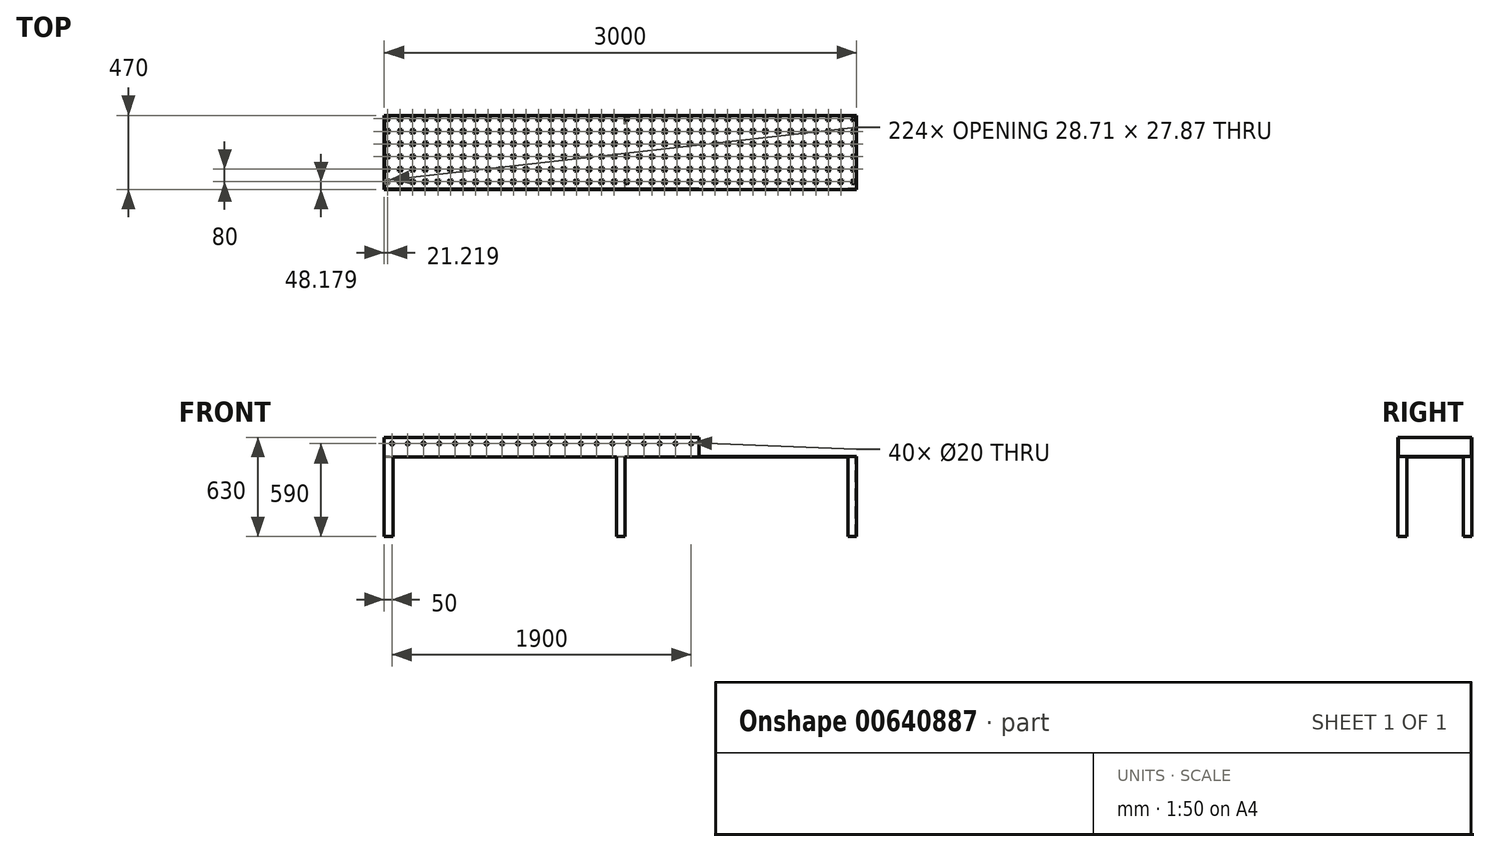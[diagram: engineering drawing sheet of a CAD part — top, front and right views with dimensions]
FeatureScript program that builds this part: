
annotation { "Feature Type Name" : "Feature", "Feature Type Description" : "" }
export const myFeature = defineFeature(function(context is Context, id is Id, definition is map)
    precondition{}
    {
        {
            var Q0;
            Q0=qCreatedBy(makeId("Top.planeOp"),FACE);
            var sketch = newSketch(context, id + "F0", { "sketchPlane" : qUnion([Q0])});
            skLineSegment(sketch, "E0", {"start": v(0, 849.7) * mm, "end": v(0, -834.12) * mm, "construction": true});
            skLineSegment(sketch, "E1", {"start": v(-852.3, 0) * mm, "end": v(888.69, 0) * mm, "construction": true});
            skLineSegment(sketch, "E2.bottom", {"start": v(-1500, 235) * mm, "end": v(1500, 235) * mm});
            skLineSegment(sketch, "E2.top", {"start": v(-1500, -235) * mm, "end": v(1500, -235) * mm});
            skLineSegment(sketch, "E2.left", {"start": v(-1500, 235) * mm, "end": v(-1500, -235) * mm});
            skLineSegment(sketch, "E2.right", {"start": v(1500, 235) * mm, "end": v(1500, -235) * mm});
            skSolve(sketch);
        }
        {
            var Q0;
            Q0 = qSketchRegion(id + "F0", true);
            extrude(context, id + "F1", {"entities" : qUnion([Q0]), "depth" : 125 * mm, "offsetDistance" : 25.4 * mm});
        }
        {
            var Q0;
            Q0=makeQuery(id+"F1.opExtrude","CAP_FACE",FACE,{"disambiguationData":[OSD([sQuery(id+"F0.wireOp",EDGE,"E2.bottom"),sQuery(id+"F0.wireOp",EDGE,"E2.top"),sQuery(id+"F0.wireOp",EDGE,"E2.left"),sQuery(id+"F0.wireOp",EDGE,"E2.right")])],"isStart":false});
            shell(context, id + "F2", {"entities" : qUnion([Q0]), "thickness" : 2.54 * mm});
        }
        {
            var Q0;
            Q0=makeQuery(id+"F1.opExtrude","SWEPT_FACE",FACE,{"disambiguationData":[OSD([sQuery(id+"F0.wireOp",EDGE,"E2.top")])]});
            var sketch = newSketch(context, id + "F3", { "sketchPlane" : qUnion([Q0])});
            skLineSegment(sketch, "E3", {"start": v(-1500, 85) * mm, "end": v(1500, 85) * mm, "construction": true});
            skCircle(sketch, "E4", {"center": v(-1450, 85) * mm, "radius": 10 * mm});
            skCircle(sketch, "E5.1.0.0", {"center": v(-1350, 85) * mm, "radius": 10 * mm});
            skCircle(sketch, "E5.2.0.0", {"center": v(-1250, 85) * mm, "radius": 10 * mm});
            skCircle(sketch, "E5.3.0.0", {"center": v(-1150, 85) * mm, "radius": 10 * mm});
            skCircle(sketch, "E5.4.0.0", {"center": v(-1050, 85) * mm, "radius": 10 * mm});
            skCircle(sketch, "E5.5.0.0", {"center": v(-950, 85) * mm, "radius": 10 * mm});
            skCircle(sketch, "E5.6.0.0", {"center": v(-850, 85) * mm, "radius": 10 * mm});
            skCircle(sketch, "E5.7.0.0", {"center": v(-750, 85) * mm, "radius": 10 * mm});
            skCircle(sketch, "E5.8.0.0", {"center": v(-650, 85) * mm, "radius": 10 * mm});
            skCircle(sketch, "E5.9.0.0", {"center": v(-550, 85) * mm, "radius": 10 * mm});
            skCircle(sketch, "E5.10.0.0", {"center": v(-450, 85) * mm, "radius": 10 * mm});
            skCircle(sketch, "E5.11.0.0", {"center": v(-350, 85) * mm, "radius": 10 * mm});
            skCircle(sketch, "E5.12.0.0", {"center": v(-250, 85) * mm, "radius": 10 * mm});
            skCircle(sketch, "E5.13.0.0", {"center": v(-150, 85) * mm, "radius": 10 * mm});
            skCircle(sketch, "E5.14.0.0", {"center": v(-50, 85) * mm, "radius": 10 * mm});
            skCircle(sketch, "E5.15.0.0", {"center": v(50, 85) * mm, "radius": 10 * mm});
            skCircle(sketch, "E5.16.0.0", {"center": v(150, 85) * mm, "radius": 10 * mm});
            skCircle(sketch, "E5.17.0.0", {"center": v(250, 85) * mm, "radius": 10 * mm});
            skCircle(sketch, "E5.18.0.0", {"center": v(350, 85) * mm, "radius": 10 * mm});
            skCircle(sketch, "E5.19.0.0", {"center": v(450, 85) * mm, "radius": 10 * mm});
            skLineSegment(sketch, "E5.direction1", {"start": v(-1450, 85) * mm, "end": v(-1350, 85) * mm, "construction": true});
            skSolve(sketch);
        }
        {
            var Q0;
            Q0 = qSketchRegion(id + "F3", true);
            var Q1;
            Q1=makeQuery(id+"F1.opExtrude","SWEPT_FACE",FACE,{"disambiguationData":[OSD([sQuery(id+"F0.wireOp",EDGE,"E2.bottom")])]});
            extrude(context, id + "F4", {"entities" : qUnion([Q0]), "operationType" : NewBodyOperationType.REMOVE, "endBound" : BoundingType.UP_TO_SURFACE, "oppositeDirection" : true, "depth" : 25.4 * mm, "endBoundEntityFace" : qUnion([Q1]), "offsetDistance" : 25.4 * mm});
        }
        {
            var Q0;
            Q0=makeQuery(id+"F1.opExtrude","CAP_FACE",FACE,{"disambiguationData":[OSD([sQuery(id+"F0.wireOp",EDGE,"E2.bottom"),sQuery(id+"F0.wireOp",EDGE,"E2.top"),sQuery(id+"F0.wireOp",EDGE,"E2.left"),sQuery(id+"F0.wireOp",EDGE,"E2.right")])],"isStart":true});
            var sketch = newSketch(context, id + "F5", { "sketchPlane" : qUnion([Q0])});
            skLineSegment(sketch, "E6", {"start": v(-1500, 235) * mm, "end": v(-1500, 180) * mm});
            skLineSegment(sketch, "E7", {"start": v(-1500, 180) * mm, "end": v(-1495, 180) * mm});
            skLineSegment(sketch, "E8", {"start": v(-1495, 180) * mm, "end": v(-1495, 230) * mm});
            skLineSegment(sketch, "E9", {"start": v(-1495, 230) * mm, "end": v(-1445, 230) * mm});
            skLineSegment(sketch, "E10", {"start": v(-1445, 230) * mm, "end": v(-1445, 235) * mm});
            skLineSegment(sketch, "E11", {"start": v(-1445, 235) * mm, "end": v(-1500, 235) * mm});
            skLineSegment(sketch, "E12", {"start": v(-1500, -235) * mm, "end": v(-1500, -180) * mm});
            skLineSegment(sketch, "E13", {"start": v(-1500, -180) * mm, "end": v(-1495, -180) * mm});
            skLineSegment(sketch, "E14", {"start": v(-1495, -180) * mm, "end": v(-1495, -230) * mm});
            skLineSegment(sketch, "E15", {"start": v(-1495, -230) * mm, "end": v(-1445, -230) * mm});
            skLineSegment(sketch, "E16", {"start": v(-1445, -230) * mm, "end": v(-1445, -235) * mm});
            skLineSegment(sketch, "E17", {"start": v(-1445, -235) * mm, "end": v(-1500, -235) * mm});
            skLineSegment(sketch, "E18", {"start": v(0, 235) * mm, "end": v(0, -263.12) * mm, "construction": true});
            skLineSegment(sketch, "E19", {"start": v(-25, 235) * mm, "end": v(30, 235) * mm});
            skLineSegment(sketch, "E20", {"start": v(30, 235) * mm, "end": v(30, 180) * mm});
            skLineSegment(sketch, "E21", {"start": v(30, 180) * mm, "end": v(25, 180) * mm});
            skLineSegment(sketch, "E22", {"start": v(25, 180) * mm, "end": v(25, 230) * mm});
            skLineSegment(sketch, "E23", {"start": v(25, 230) * mm, "end": v(-25, 230) * mm});
            skLineSegment(sketch, "E24", {"start": v(-25, 230) * mm, "end": v(-25, 235) * mm});
            skLineSegment(sketch, "E25", {"start": v(-25, -235) * mm, "end": v(30, -235) * mm});
            skLineSegment(sketch, "E26", {"start": v(30, -235) * mm, "end": v(30, -180) * mm});
            skLineSegment(sketch, "E27", {"start": v(30, -180) * mm, "end": v(25, -180) * mm});
            skLineSegment(sketch, "E28", {"start": v(25, -180) * mm, "end": v(25, -230) * mm});
            skLineSegment(sketch, "E29", {"start": v(25, -230) * mm, "end": v(-25, -230) * mm});
            skLineSegment(sketch, "E30", {"start": v(-25, -230) * mm, "end": v(-25, -235) * mm});
            skLineSegment(sketch, "E31", {"start": v(1445, 235) * mm, "end": v(1500, 235) * mm});
            skLineSegment(sketch, "E32", {"start": v(1500, 235) * mm, "end": v(1500, 180) * mm});
            skLineSegment(sketch, "E33", {"start": v(1500, 180) * mm, "end": v(1495, 180) * mm});
            skLineSegment(sketch, "E34", {"start": v(1495, 180) * mm, "end": v(1495, 230) * mm});
            skLineSegment(sketch, "E35", {"start": v(1495, 230) * mm, "end": v(1445, 230) * mm});
            skLineSegment(sketch, "E36", {"start": v(1445, 230) * mm, "end": v(1445, 235) * mm});
            skLineSegment(sketch, "E37", {"start": v(1500, -180) * mm, "end": v(1500, -235) * mm});
            skLineSegment(sketch, "E38", {"start": v(1500, -235) * mm, "end": v(1445, -235) * mm});
            skLineSegment(sketch, "E39", {"start": v(1445, -235) * mm, "end": v(1445, -230) * mm});
            skLineSegment(sketch, "E40", {"start": v(1445, -230) * mm, "end": v(1495, -230) * mm});
            skLineSegment(sketch, "E41", {"start": v(1495, -230) * mm, "end": v(1495, -180) * mm});
            skLineSegment(sketch, "E42", {"start": v(1495, -180) * mm, "end": v(1500, -180) * mm});
            skSolve(sketch);
        }
        {
            var Q0;
            Q0 = qSketchRegion(id + "F5", true);
            extrude(context, id + "F6", {"entities" : qUnion([Q0]), "operationType" : NewBodyOperationType.ADD, "depth" : 505 * mm, "offsetDistance" : 25.4 * mm});
        }
        {
            var Q0;
            Q0=makeQuery(id+"F6.boolean.opBoolean","MERGE",FACE,{"derivedFrom":[makeQuery(id+"F1.opExtrude","SWEPT_FACE",FACE,{"disambiguationData":[OSD([sQuery(id+"F0.wireOp",EDGE,"E2.right")])]}),makeQuery(id+"F6.opExtrude","SWEPT_FACE",FACE,{"disambiguationData":[OSD([sQuery(id+"F5.wireOp",EDGE,"E32")])]}),makeQuery(id+"F6.opExtrude","SWEPT_FACE",FACE,{"disambiguationData":[OSD([sQuery(id+"F5.wireOp",EDGE,"E37")])]})]});
            var sketch = newSketch(context, id + "F7", { "sketchPlane" : qUnion([Q0])});
            skLineSegment(sketch, "E43.bottom", {"start": v(-235, 125) * mm, "end": v(235, 125) * mm});
            skLineSegment(sketch, "E43.left", {"start": v(-235, 125) * mm, "end": v(-235, 2.54) * mm});
            skLineSegment(sketch, "E43.right", {"start": v(235, 125) * mm, "end": v(235, 2.54) * mm});
            skLineSegment(sketch, "E44", {"start": v(-235, 2.54) * mm, "end": v(235, 2.54) * mm});
            skSolve(sketch);
        }
        {
            var Q0;
            Q0 = qSketchRegion(id + "F7", true);
            extrude(context, id + "F8", {"entities" : qUnion([Q0]), "operationType" : NewBodyOperationType.REMOVE, "oppositeDirection" : true, "depth" : 1000 * mm, "offsetDistance" : 25.4 * mm});
        }
        {
            var Q0;
            Q0=makeQuery(id+"F8.boolean.opBoolean","MERGE",FACE,{"derivedFrom":[makeQuery(id+"F2.opShell","OFFSET_FACE",FACE,{"disambiguationData":[OSD([sQuery(id+"F0.wireOp",EDGE,"E2.bottom"),sQuery(id+"F0.wireOp",EDGE,"E2.top"),sQuery(id+"F0.wireOp",EDGE,"E2.left"),sQuery(id+"F0.wireOp",EDGE,"E2.right")])]}),makeQuery(id+"F8.opExtrude","SWEPT_FACE",FACE,{"disambiguationData":[OSD([sQuery(id+"F7.wireOp",EDGE,"E44")])]})]});
            var sketch = newSketch(context, id + "F9", { "sketchPlane" : qUnion([Q0])});
            skCircle(sketch, "E45.cCircle", {"center": v(-1478.78, 213.18) * mm, "radius": 12.7 * mm, "construction": true});
            skLineSegment(sketch, "E45.0", {"start": v(-1464.43, 210.17) * mm, "end": v(-1474.2, 199.25) * mm});
            skLineSegment(sketch, "E45.1", {"start": v(-1474.2, 199.25) * mm, "end": v(-1488.56, 202.25) * mm});
            skLineSegment(sketch, "E45.2", {"start": v(-1488.56, 202.25) * mm, "end": v(-1493.14, 216.18) * mm});
            skLineSegment(sketch, "E45.3", {"start": v(-1493.14, 216.18) * mm, "end": v(-1483.36, 227.11) * mm});
            skLineSegment(sketch, "E45.4", {"start": v(-1483.36, 227.11) * mm, "end": v(-1469, 224.1) * mm});
            skLineSegment(sketch, "E45.5", {"start": v(-1469, 224.1) * mm, "end": v(-1464.43, 210.17) * mm});
            skPoint(sketch, "E45.0.midPoint", {"position": v(-1469.32, 204.71) * mm});
            skLineSegment(sketch, "E46.0.1.0", {"start": v(-1474.2, 119.25) * mm, "end": v(-1488.56, 122.25) * mm});
            skLineSegment(sketch, "E46.0.1.1", {"start": v(-1464.43, 130.17) * mm, "end": v(-1474.2, 119.25) * mm});
            skLineSegment(sketch, "E46.0.1.2", {"start": v(-1469, 144.1) * mm, "end": v(-1464.43, 130.17) * mm});
            skLineSegment(sketch, "E46.0.1.3", {"start": v(-1483.36, 147.11) * mm, "end": v(-1469, 144.1) * mm});
            skLineSegment(sketch, "E46.0.1.4", {"start": v(-1493.14, 136.18) * mm, "end": v(-1483.36, 147.11) * mm});
            skLineSegment(sketch, "E46.0.1.5", {"start": v(-1488.56, 122.25) * mm, "end": v(-1493.14, 136.18) * mm});
            skLineSegment(sketch, "E46.0.2.0", {"start": v(-1474.2, 39.25) * mm, "end": v(-1488.56, 42.25) * mm});
            skLineSegment(sketch, "E46.0.2.1", {"start": v(-1464.43, 50.17) * mm, "end": v(-1474.2, 39.25) * mm});
            skLineSegment(sketch, "E46.0.2.2", {"start": v(-1469, 64.1) * mm, "end": v(-1464.43, 50.17) * mm});
            skLineSegment(sketch, "E46.0.2.3", {"start": v(-1483.36, 67.11) * mm, "end": v(-1469, 64.1) * mm});
            skLineSegment(sketch, "E46.0.2.4", {"start": v(-1493.14, 56.18) * mm, "end": v(-1483.36, 67.11) * mm});
            skLineSegment(sketch, "E46.0.2.5", {"start": v(-1488.56, 42.25) * mm, "end": v(-1493.14, 56.18) * mm});
            skLineSegment(sketch, "E46.0.3.0", {"start": v(-1474.2, -40.75) * mm, "end": v(-1488.56, -37.75) * mm});
            skLineSegment(sketch, "E46.0.3.1", {"start": v(-1464.43, -29.83) * mm, "end": v(-1474.2, -40.75) * mm});
            skLineSegment(sketch, "E46.0.3.2", {"start": v(-1469, -15.9) * mm, "end": v(-1464.43, -29.83) * mm});
            skLineSegment(sketch, "E46.0.3.3", {"start": v(-1483.36, -12.89) * mm, "end": v(-1469, -15.9) * mm});
            skLineSegment(sketch, "E46.0.3.4", {"start": v(-1493.14, -23.82) * mm, "end": v(-1483.36, -12.89) * mm});
            skLineSegment(sketch, "E46.0.3.5", {"start": v(-1488.56, -37.75) * mm, "end": v(-1493.14, -23.82) * mm});
            skLineSegment(sketch, "E46.0.4.0", {"start": v(-1474.2, -120.75) * mm, "end": v(-1488.56, -117.75) * mm});
            skLineSegment(sketch, "E46.0.4.1", {"start": v(-1464.43, -109.83) * mm, "end": v(-1474.2, -120.75) * mm});
            skLineSegment(sketch, "E46.0.4.2", {"start": v(-1469, -95.9) * mm, "end": v(-1464.43, -109.83) * mm});
            skLineSegment(sketch, "E46.0.4.3", {"start": v(-1483.36, -92.89) * mm, "end": v(-1469, -95.9) * mm});
            skLineSegment(sketch, "E46.0.4.4", {"start": v(-1493.14, -103.82) * mm, "end": v(-1483.36, -92.89) * mm});
            skLineSegment(sketch, "E46.0.4.5", {"start": v(-1488.56, -117.75) * mm, "end": v(-1493.14, -103.82) * mm});
            skLineSegment(sketch, "E46.0.5.0", {"start": v(-1474.2, -200.75) * mm, "end": v(-1488.56, -197.75) * mm});
            skLineSegment(sketch, "E46.0.5.1", {"start": v(-1464.43, -189.83) * mm, "end": v(-1474.2, -200.75) * mm});
            skLineSegment(sketch, "E46.0.5.2", {"start": v(-1469, -175.9) * mm, "end": v(-1464.43, -189.83) * mm});
            skLineSegment(sketch, "E46.0.5.3", {"start": v(-1483.36, -172.89) * mm, "end": v(-1469, -175.9) * mm});
            skLineSegment(sketch, "E46.0.5.4", {"start": v(-1493.14, -183.82) * mm, "end": v(-1483.36, -172.89) * mm});
            skLineSegment(sketch, "E46.0.5.5", {"start": v(-1488.56, -197.75) * mm, "end": v(-1493.14, -183.82) * mm});
            skLineSegment(sketch, "E46.1.0.0", {"start": v(-1394.2, 199.25) * mm, "end": v(-1408.56, 202.25) * mm});
            skLineSegment(sketch, "E46.1.0.1", {"start": v(-1384.43, 210.17) * mm, "end": v(-1394.2, 199.25) * mm});
            skLineSegment(sketch, "E46.1.0.2", {"start": v(-1389, 224.1) * mm, "end": v(-1384.43, 210.17) * mm});
            skLineSegment(sketch, "E46.1.0.3", {"start": v(-1403.36, 227.11) * mm, "end": v(-1389, 224.1) * mm});
            skLineSegment(sketch, "E46.1.0.4", {"start": v(-1413.14, 216.18) * mm, "end": v(-1403.36, 227.11) * mm});
            skLineSegment(sketch, "E46.1.0.5", {"start": v(-1408.56, 202.25) * mm, "end": v(-1413.14, 216.18) * mm});
            skLineSegment(sketch, "E46.1.1.0", {"start": v(-1394.2, 119.25) * mm, "end": v(-1408.56, 122.25) * mm});
            skLineSegment(sketch, "E46.1.1.1", {"start": v(-1384.43, 130.17) * mm, "end": v(-1394.2, 119.25) * mm});
            skLineSegment(sketch, "E46.1.1.2", {"start": v(-1389, 144.1) * mm, "end": v(-1384.43, 130.17) * mm});
            skLineSegment(sketch, "E46.1.1.3", {"start": v(-1403.36, 147.11) * mm, "end": v(-1389, 144.1) * mm});
            skLineSegment(sketch, "E46.1.1.4", {"start": v(-1413.14, 136.18) * mm, "end": v(-1403.36, 147.11) * mm});
            skLineSegment(sketch, "E46.1.1.5", {"start": v(-1408.56, 122.25) * mm, "end": v(-1413.14, 136.18) * mm});
            skLineSegment(sketch, "E46.1.2.0", {"start": v(-1394.2, 39.25) * mm, "end": v(-1408.56, 42.25) * mm});
            skLineSegment(sketch, "E46.1.2.1", {"start": v(-1384.43, 50.17) * mm, "end": v(-1394.2, 39.25) * mm});
            skLineSegment(sketch, "E46.1.2.2", {"start": v(-1389, 64.1) * mm, "end": v(-1384.43, 50.17) * mm});
            skLineSegment(sketch, "E46.1.2.3", {"start": v(-1403.36, 67.11) * mm, "end": v(-1389, 64.1) * mm});
            skLineSegment(sketch, "E46.1.2.4", {"start": v(-1413.14, 56.18) * mm, "end": v(-1403.36, 67.11) * mm});
            skLineSegment(sketch, "E46.1.2.5", {"start": v(-1408.56, 42.25) * mm, "end": v(-1413.14, 56.18) * mm});
            skLineSegment(sketch, "E46.1.3.0", {"start": v(-1394.2, -40.75) * mm, "end": v(-1408.56, -37.75) * mm});
            skLineSegment(sketch, "E46.1.3.1", {"start": v(-1384.43, -29.83) * mm, "end": v(-1394.2, -40.75) * mm});
            skLineSegment(sketch, "E46.1.3.2", {"start": v(-1389, -15.9) * mm, "end": v(-1384.43, -29.83) * mm});
            skLineSegment(sketch, "E46.1.3.3", {"start": v(-1403.36, -12.89) * mm, "end": v(-1389, -15.9) * mm});
            skLineSegment(sketch, "E46.1.3.4", {"start": v(-1413.14, -23.82) * mm, "end": v(-1403.36, -12.89) * mm});
            skLineSegment(sketch, "E46.1.3.5", {"start": v(-1408.56, -37.75) * mm, "end": v(-1413.14, -23.82) * mm});
            skLineSegment(sketch, "E46.1.4.0", {"start": v(-1394.2, -120.75) * mm, "end": v(-1408.56, -117.75) * mm});
            skLineSegment(sketch, "E46.1.4.1", {"start": v(-1384.43, -109.83) * mm, "end": v(-1394.2, -120.75) * mm});
            skLineSegment(sketch, "E46.1.4.2", {"start": v(-1389, -95.9) * mm, "end": v(-1384.43, -109.83) * mm});
            skLineSegment(sketch, "E46.1.4.3", {"start": v(-1403.36, -92.89) * mm, "end": v(-1389, -95.9) * mm});
            skLineSegment(sketch, "E46.1.4.4", {"start": v(-1413.14, -103.82) * mm, "end": v(-1403.36, -92.89) * mm});
            skLineSegment(sketch, "E46.1.4.5", {"start": v(-1408.56, -117.75) * mm, "end": v(-1413.14, -103.82) * mm});
            skLineSegment(sketch, "E46.1.5.0", {"start": v(-1394.2, -200.75) * mm, "end": v(-1408.56, -197.75) * mm});
            skLineSegment(sketch, "E46.1.5.1", {"start": v(-1384.43, -189.83) * mm, "end": v(-1394.2, -200.75) * mm});
            skLineSegment(sketch, "E46.1.5.2", {"start": v(-1389, -175.9) * mm, "end": v(-1384.43, -189.83) * mm});
            skLineSegment(sketch, "E46.1.5.3", {"start": v(-1403.36, -172.89) * mm, "end": v(-1389, -175.9) * mm});
            skLineSegment(sketch, "E46.1.5.4", {"start": v(-1413.14, -183.82) * mm, "end": v(-1403.36, -172.89) * mm});
            skLineSegment(sketch, "E46.1.5.5", {"start": v(-1408.56, -197.75) * mm, "end": v(-1413.14, -183.82) * mm});
            skLineSegment(sketch, "E46.2.0.0", {"start": v(-1314.2, 199.25) * mm, "end": v(-1328.56, 202.25) * mm});
            skLineSegment(sketch, "E46.2.0.1", {"start": v(-1304.43, 210.17) * mm, "end": v(-1314.2, 199.25) * mm});
            skLineSegment(sketch, "E46.2.0.2", {"start": v(-1309, 224.1) * mm, "end": v(-1304.43, 210.17) * mm});
            skLineSegment(sketch, "E46.2.0.3", {"start": v(-1323.36, 227.11) * mm, "end": v(-1309, 224.1) * mm});
            skLineSegment(sketch, "E46.2.0.4", {"start": v(-1333.14, 216.18) * mm, "end": v(-1323.36, 227.11) * mm});
            skLineSegment(sketch, "E46.2.0.5", {"start": v(-1328.56, 202.25) * mm, "end": v(-1333.14, 216.18) * mm});
            skLineSegment(sketch, "E46.2.1.0", {"start": v(-1314.2, 119.25) * mm, "end": v(-1328.56, 122.25) * mm});
            skLineSegment(sketch, "E46.2.1.1", {"start": v(-1304.43, 130.17) * mm, "end": v(-1314.2, 119.25) * mm});
            skLineSegment(sketch, "E46.2.1.2", {"start": v(-1309, 144.1) * mm, "end": v(-1304.43, 130.17) * mm});
            skLineSegment(sketch, "E46.2.1.3", {"start": v(-1323.36, 147.11) * mm, "end": v(-1309, 144.1) * mm});
            skLineSegment(sketch, "E46.2.1.4", {"start": v(-1333.14, 136.18) * mm, "end": v(-1323.36, 147.11) * mm});
            skLineSegment(sketch, "E46.2.1.5", {"start": v(-1328.56, 122.25) * mm, "end": v(-1333.14, 136.18) * mm});
            skLineSegment(sketch, "E46.2.2.0", {"start": v(-1314.2, 39.25) * mm, "end": v(-1328.56, 42.25) * mm});
            skLineSegment(sketch, "E46.2.2.1", {"start": v(-1304.43, 50.17) * mm, "end": v(-1314.2, 39.25) * mm});
            skLineSegment(sketch, "E46.2.2.2", {"start": v(-1309, 64.1) * mm, "end": v(-1304.43, 50.17) * mm});
            skLineSegment(sketch, "E46.2.2.3", {"start": v(-1323.36, 67.11) * mm, "end": v(-1309, 64.1) * mm});
            skLineSegment(sketch, "E46.2.2.4", {"start": v(-1333.14, 56.18) * mm, "end": v(-1323.36, 67.11) * mm});
            skLineSegment(sketch, "E46.2.2.5", {"start": v(-1328.56, 42.25) * mm, "end": v(-1333.14, 56.18) * mm});
            skLineSegment(sketch, "E46.2.3.0", {"start": v(-1314.2, -40.75) * mm, "end": v(-1328.56, -37.75) * mm});
            skLineSegment(sketch, "E46.2.3.1", {"start": v(-1304.43, -29.83) * mm, "end": v(-1314.2, -40.75) * mm});
            skLineSegment(sketch, "E46.2.3.2", {"start": v(-1309, -15.9) * mm, "end": v(-1304.43, -29.83) * mm});
            skLineSegment(sketch, "E46.2.3.3", {"start": v(-1323.36, -12.89) * mm, "end": v(-1309, -15.9) * mm});
            skLineSegment(sketch, "E46.2.3.4", {"start": v(-1333.14, -23.82) * mm, "end": v(-1323.36, -12.89) * mm});
            skLineSegment(sketch, "E46.2.3.5", {"start": v(-1328.56, -37.75) * mm, "end": v(-1333.14, -23.82) * mm});
            skLineSegment(sketch, "E46.2.4.0", {"start": v(-1314.2, -120.75) * mm, "end": v(-1328.56, -117.75) * mm});
            skLineSegment(sketch, "E46.2.4.1", {"start": v(-1304.43, -109.83) * mm, "end": v(-1314.2, -120.75) * mm});
            skLineSegment(sketch, "E46.2.4.2", {"start": v(-1309, -95.9) * mm, "end": v(-1304.43, -109.83) * mm});
            skLineSegment(sketch, "E46.2.4.3", {"start": v(-1323.36, -92.89) * mm, "end": v(-1309, -95.9) * mm});
            skLineSegment(sketch, "E46.2.4.4", {"start": v(-1333.14, -103.82) * mm, "end": v(-1323.36, -92.89) * mm});
            skLineSegment(sketch, "E46.2.4.5", {"start": v(-1328.56, -117.75) * mm, "end": v(-1333.14, -103.82) * mm});
            skLineSegment(sketch, "E46.2.5.0", {"start": v(-1314.2, -200.75) * mm, "end": v(-1328.56, -197.75) * mm});
            skLineSegment(sketch, "E46.2.5.1", {"start": v(-1304.43, -189.83) * mm, "end": v(-1314.2, -200.75) * mm});
            skLineSegment(sketch, "E46.2.5.2", {"start": v(-1309, -175.9) * mm, "end": v(-1304.43, -189.83) * mm});
            skLineSegment(sketch, "E46.2.5.3", {"start": v(-1323.36, -172.89) * mm, "end": v(-1309, -175.9) * mm});
            skLineSegment(sketch, "E46.2.5.4", {"start": v(-1333.14, -183.82) * mm, "end": v(-1323.36, -172.89) * mm});
            skLineSegment(sketch, "E46.2.5.5", {"start": v(-1328.56, -197.75) * mm, "end": v(-1333.14, -183.82) * mm});
            skLineSegment(sketch, "E46.3.0.0", {"start": v(-1234.2, 199.25) * mm, "end": v(-1248.56, 202.25) * mm});
            skLineSegment(sketch, "E46.3.0.1", {"start": v(-1224.43, 210.17) * mm, "end": v(-1234.2, 199.25) * mm});
            skLineSegment(sketch, "E46.3.0.2", {"start": v(-1229, 224.1) * mm, "end": v(-1224.43, 210.17) * mm});
            skLineSegment(sketch, "E46.3.0.3", {"start": v(-1243.36, 227.11) * mm, "end": v(-1229, 224.1) * mm});
            skLineSegment(sketch, "E46.3.0.4", {"start": v(-1253.14, 216.18) * mm, "end": v(-1243.36, 227.11) * mm});
            skLineSegment(sketch, "E46.3.0.5", {"start": v(-1248.56, 202.25) * mm, "end": v(-1253.14, 216.18) * mm});
            skLineSegment(sketch, "E46.3.1.0", {"start": v(-1234.2, 119.25) * mm, "end": v(-1248.56, 122.25) * mm});
            skLineSegment(sketch, "E46.3.1.1", {"start": v(-1224.43, 130.17) * mm, "end": v(-1234.2, 119.25) * mm});
            skLineSegment(sketch, "E46.3.1.2", {"start": v(-1229, 144.1) * mm, "end": v(-1224.43, 130.17) * mm});
            skLineSegment(sketch, "E46.3.1.3", {"start": v(-1243.36, 147.11) * mm, "end": v(-1229, 144.1) * mm});
            skLineSegment(sketch, "E46.3.1.4", {"start": v(-1253.14, 136.18) * mm, "end": v(-1243.36, 147.11) * mm});
            skLineSegment(sketch, "E46.3.1.5", {"start": v(-1248.56, 122.25) * mm, "end": v(-1253.14, 136.18) * mm});
            skLineSegment(sketch, "E46.3.2.0", {"start": v(-1234.2, 39.25) * mm, "end": v(-1248.56, 42.25) * mm});
            skLineSegment(sketch, "E46.3.2.1", {"start": v(-1224.43, 50.17) * mm, "end": v(-1234.2, 39.25) * mm});
            skLineSegment(sketch, "E46.3.2.2", {"start": v(-1229, 64.1) * mm, "end": v(-1224.43, 50.17) * mm});
            skLineSegment(sketch, "E46.3.2.3", {"start": v(-1243.36, 67.11) * mm, "end": v(-1229, 64.1) * mm});
            skLineSegment(sketch, "E46.3.2.4", {"start": v(-1253.14, 56.18) * mm, "end": v(-1243.36, 67.11) * mm});
            skLineSegment(sketch, "E46.3.2.5", {"start": v(-1248.56, 42.25) * mm, "end": v(-1253.14, 56.18) * mm});
            skLineSegment(sketch, "E46.3.3.0", {"start": v(-1234.2, -40.75) * mm, "end": v(-1248.56, -37.75) * mm});
            skLineSegment(sketch, "E46.3.3.1", {"start": v(-1224.43, -29.83) * mm, "end": v(-1234.2, -40.75) * mm});
            skLineSegment(sketch, "E46.3.3.2", {"start": v(-1229, -15.9) * mm, "end": v(-1224.43, -29.83) * mm});
            skLineSegment(sketch, "E46.3.3.3", {"start": v(-1243.36, -12.89) * mm, "end": v(-1229, -15.9) * mm});
            skLineSegment(sketch, "E46.3.3.4", {"start": v(-1253.14, -23.82) * mm, "end": v(-1243.36, -12.89) * mm});
            skLineSegment(sketch, "E46.3.3.5", {"start": v(-1248.56, -37.75) * mm, "end": v(-1253.14, -23.82) * mm});
            skLineSegment(sketch, "E46.3.4.0", {"start": v(-1234.2, -120.75) * mm, "end": v(-1248.56, -117.75) * mm});
            skLineSegment(sketch, "E46.3.4.1", {"start": v(-1224.43, -109.83) * mm, "end": v(-1234.2, -120.75) * mm});
            skLineSegment(sketch, "E46.3.4.2", {"start": v(-1229, -95.9) * mm, "end": v(-1224.43, -109.83) * mm});
            skLineSegment(sketch, "E46.3.4.3", {"start": v(-1243.36, -92.89) * mm, "end": v(-1229, -95.9) * mm});
            skLineSegment(sketch, "E46.3.4.4", {"start": v(-1253.14, -103.82) * mm, "end": v(-1243.36, -92.89) * mm});
            skLineSegment(sketch, "E46.3.4.5", {"start": v(-1248.56, -117.75) * mm, "end": v(-1253.14, -103.82) * mm});
            skLineSegment(sketch, "E46.3.5.0", {"start": v(-1234.2, -200.75) * mm, "end": v(-1248.56, -197.75) * mm});
            skLineSegment(sketch, "E46.3.5.1", {"start": v(-1224.43, -189.83) * mm, "end": v(-1234.2, -200.75) * mm});
            skLineSegment(sketch, "E46.3.5.2", {"start": v(-1229, -175.9) * mm, "end": v(-1224.43, -189.83) * mm});
            skLineSegment(sketch, "E46.3.5.3", {"start": v(-1243.36, -172.89) * mm, "end": v(-1229, -175.9) * mm});
            skLineSegment(sketch, "E46.3.5.4", {"start": v(-1253.14, -183.82) * mm, "end": v(-1243.36, -172.89) * mm});
            skLineSegment(sketch, "E46.3.5.5", {"start": v(-1248.56, -197.75) * mm, "end": v(-1253.14, -183.82) * mm});
            skLineSegment(sketch, "E46.4.0.0", {"start": v(-1154.2, 199.25) * mm, "end": v(-1168.56, 202.25) * mm});
            skLineSegment(sketch, "E46.4.0.1", {"start": v(-1144.43, 210.17) * mm, "end": v(-1154.2, 199.25) * mm});
            skLineSegment(sketch, "E46.4.0.2", {"start": v(-1149, 224.1) * mm, "end": v(-1144.43, 210.17) * mm});
            skLineSegment(sketch, "E46.4.0.3", {"start": v(-1163.36, 227.11) * mm, "end": v(-1149, 224.1) * mm});
            skLineSegment(sketch, "E46.4.0.4", {"start": v(-1173.14, 216.18) * mm, "end": v(-1163.36, 227.11) * mm});
            skLineSegment(sketch, "E46.4.0.5", {"start": v(-1168.56, 202.25) * mm, "end": v(-1173.14, 216.18) * mm});
            skLineSegment(sketch, "E46.4.1.0", {"start": v(-1154.2, 119.25) * mm, "end": v(-1168.56, 122.25) * mm});
            skLineSegment(sketch, "E46.4.1.1", {"start": v(-1144.43, 130.17) * mm, "end": v(-1154.2, 119.25) * mm});
            skLineSegment(sketch, "E46.4.1.2", {"start": v(-1149, 144.1) * mm, "end": v(-1144.43, 130.17) * mm});
            skLineSegment(sketch, "E46.4.1.3", {"start": v(-1163.36, 147.11) * mm, "end": v(-1149, 144.1) * mm});
            skLineSegment(sketch, "E46.4.1.4", {"start": v(-1173.14, 136.18) * mm, "end": v(-1163.36, 147.11) * mm});
            skLineSegment(sketch, "E46.4.1.5", {"start": v(-1168.56, 122.25) * mm, "end": v(-1173.14, 136.18) * mm});
            skLineSegment(sketch, "E46.4.2.0", {"start": v(-1154.2, 39.25) * mm, "end": v(-1168.56, 42.25) * mm});
            skLineSegment(sketch, "E46.4.2.1", {"start": v(-1144.43, 50.17) * mm, "end": v(-1154.2, 39.25) * mm});
            skLineSegment(sketch, "E46.4.2.2", {"start": v(-1149, 64.1) * mm, "end": v(-1144.43, 50.17) * mm});
            skLineSegment(sketch, "E46.4.2.3", {"start": v(-1163.36, 67.11) * mm, "end": v(-1149, 64.1) * mm});
            skLineSegment(sketch, "E46.4.2.4", {"start": v(-1173.14, 56.18) * mm, "end": v(-1163.36, 67.11) * mm});
            skLineSegment(sketch, "E46.4.2.5", {"start": v(-1168.56, 42.25) * mm, "end": v(-1173.14, 56.18) * mm});
            skLineSegment(sketch, "E46.4.3.0", {"start": v(-1154.2, -40.75) * mm, "end": v(-1168.56, -37.75) * mm});
            skLineSegment(sketch, "E46.4.3.1", {"start": v(-1144.43, -29.83) * mm, "end": v(-1154.2, -40.75) * mm});
            skLineSegment(sketch, "E46.4.3.2", {"start": v(-1149, -15.9) * mm, "end": v(-1144.43, -29.83) * mm});
            skLineSegment(sketch, "E46.4.3.3", {"start": v(-1163.36, -12.89) * mm, "end": v(-1149, -15.9) * mm});
            skLineSegment(sketch, "E46.4.3.4", {"start": v(-1173.14, -23.82) * mm, "end": v(-1163.36, -12.89) * mm});
            skLineSegment(sketch, "E46.4.3.5", {"start": v(-1168.56, -37.75) * mm, "end": v(-1173.14, -23.82) * mm});
            skLineSegment(sketch, "E46.4.4.0", {"start": v(-1154.2, -120.75) * mm, "end": v(-1168.56, -117.75) * mm});
            skLineSegment(sketch, "E46.4.4.1", {"start": v(-1144.43, -109.83) * mm, "end": v(-1154.2, -120.75) * mm});
            skLineSegment(sketch, "E46.4.4.2", {"start": v(-1149, -95.9) * mm, "end": v(-1144.43, -109.83) * mm});
            skLineSegment(sketch, "E46.4.4.3", {"start": v(-1163.36, -92.89) * mm, "end": v(-1149, -95.9) * mm});
            skLineSegment(sketch, "E46.4.4.4", {"start": v(-1173.14, -103.82) * mm, "end": v(-1163.36, -92.89) * mm});
            skLineSegment(sketch, "E46.4.4.5", {"start": v(-1168.56, -117.75) * mm, "end": v(-1173.14, -103.82) * mm});
            skLineSegment(sketch, "E46.4.5.0", {"start": v(-1154.2, -200.75) * mm, "end": v(-1168.56, -197.75) * mm});
            skLineSegment(sketch, "E46.4.5.1", {"start": v(-1144.43, -189.83) * mm, "end": v(-1154.2, -200.75) * mm});
            skLineSegment(sketch, "E46.4.5.2", {"start": v(-1149, -175.9) * mm, "end": v(-1144.43, -189.83) * mm});
            skLineSegment(sketch, "E46.4.5.3", {"start": v(-1163.36, -172.89) * mm, "end": v(-1149, -175.9) * mm});
            skLineSegment(sketch, "E46.4.5.4", {"start": v(-1173.14, -183.82) * mm, "end": v(-1163.36, -172.89) * mm});
            skLineSegment(sketch, "E46.4.5.5", {"start": v(-1168.56, -197.75) * mm, "end": v(-1173.14, -183.82) * mm});
            skLineSegment(sketch, "E46.5.0.0", {"start": v(-1074.2, 199.25) * mm, "end": v(-1088.56, 202.25) * mm});
            skLineSegment(sketch, "E46.5.0.1", {"start": v(-1064.43, 210.17) * mm, "end": v(-1074.2, 199.25) * mm});
            skLineSegment(sketch, "E46.5.0.2", {"start": v(-1069, 224.1) * mm, "end": v(-1064.43, 210.17) * mm});
            skLineSegment(sketch, "E46.5.0.3", {"start": v(-1083.36, 227.11) * mm, "end": v(-1069, 224.1) * mm});
            skLineSegment(sketch, "E46.5.0.4", {"start": v(-1093.14, 216.18) * mm, "end": v(-1083.36, 227.11) * mm});
            skLineSegment(sketch, "E46.5.0.5", {"start": v(-1088.56, 202.25) * mm, "end": v(-1093.14, 216.18) * mm});
            skLineSegment(sketch, "E46.5.1.0", {"start": v(-1074.2, 119.25) * mm, "end": v(-1088.56, 122.25) * mm});
            skLineSegment(sketch, "E46.5.1.1", {"start": v(-1064.43, 130.17) * mm, "end": v(-1074.2, 119.25) * mm});
            skLineSegment(sketch, "E46.5.1.2", {"start": v(-1069, 144.1) * mm, "end": v(-1064.43, 130.17) * mm});
            skLineSegment(sketch, "E46.5.1.3", {"start": v(-1083.36, 147.11) * mm, "end": v(-1069, 144.1) * mm});
            skLineSegment(sketch, "E46.5.1.4", {"start": v(-1093.14, 136.18) * mm, "end": v(-1083.36, 147.11) * mm});
            skLineSegment(sketch, "E46.5.1.5", {"start": v(-1088.56, 122.25) * mm, "end": v(-1093.14, 136.18) * mm});
            skLineSegment(sketch, "E46.5.2.0", {"start": v(-1074.2, 39.25) * mm, "end": v(-1088.56, 42.25) * mm});
            skLineSegment(sketch, "E46.5.2.1", {"start": v(-1064.43, 50.17) * mm, "end": v(-1074.2, 39.25) * mm});
            skLineSegment(sketch, "E46.5.2.2", {"start": v(-1069, 64.1) * mm, "end": v(-1064.43, 50.17) * mm});
            skLineSegment(sketch, "E46.5.2.3", {"start": v(-1083.36, 67.11) * mm, "end": v(-1069, 64.1) * mm});
            skLineSegment(sketch, "E46.5.2.4", {"start": v(-1093.14, 56.18) * mm, "end": v(-1083.36, 67.11) * mm});
            skLineSegment(sketch, "E46.5.2.5", {"start": v(-1088.56, 42.25) * mm, "end": v(-1093.14, 56.18) * mm});
            skLineSegment(sketch, "E46.5.3.0", {"start": v(-1074.2, -40.75) * mm, "end": v(-1088.56, -37.75) * mm});
            skLineSegment(sketch, "E46.5.3.1", {"start": v(-1064.43, -29.83) * mm, "end": v(-1074.2, -40.75) * mm});
            skLineSegment(sketch, "E46.5.3.2", {"start": v(-1069, -15.9) * mm, "end": v(-1064.43, -29.83) * mm});
            skLineSegment(sketch, "E46.5.3.3", {"start": v(-1083.36, -12.89) * mm, "end": v(-1069, -15.9) * mm});
            skLineSegment(sketch, "E46.5.3.4", {"start": v(-1093.14, -23.82) * mm, "end": v(-1083.36, -12.89) * mm});
            skLineSegment(sketch, "E46.5.3.5", {"start": v(-1088.56, -37.75) * mm, "end": v(-1093.14, -23.82) * mm});
            skLineSegment(sketch, "E46.5.4.0", {"start": v(-1074.2, -120.75) * mm, "end": v(-1088.56, -117.75) * mm});
            skLineSegment(sketch, "E46.5.4.1", {"start": v(-1064.43, -109.83) * mm, "end": v(-1074.2, -120.75) * mm});
            skLineSegment(sketch, "E46.5.4.2", {"start": v(-1069, -95.9) * mm, "end": v(-1064.43, -109.83) * mm});
            skLineSegment(sketch, "E46.5.4.3", {"start": v(-1083.36, -92.89) * mm, "end": v(-1069, -95.9) * mm});
            skLineSegment(sketch, "E46.5.4.4", {"start": v(-1093.14, -103.82) * mm, "end": v(-1083.36, -92.89) * mm});
            skLineSegment(sketch, "E46.5.4.5", {"start": v(-1088.56, -117.75) * mm, "end": v(-1093.14, -103.82) * mm});
            skLineSegment(sketch, "E46.5.5.0", {"start": v(-1074.2, -200.75) * mm, "end": v(-1088.56, -197.75) * mm});
            skLineSegment(sketch, "E46.5.5.1", {"start": v(-1064.43, -189.83) * mm, "end": v(-1074.2, -200.75) * mm});
            skLineSegment(sketch, "E46.5.5.2", {"start": v(-1069, -175.9) * mm, "end": v(-1064.43, -189.83) * mm});
            skLineSegment(sketch, "E46.5.5.3", {"start": v(-1083.36, -172.89) * mm, "end": v(-1069, -175.9) * mm});
            skLineSegment(sketch, "E46.5.5.4", {"start": v(-1093.14, -183.82) * mm, "end": v(-1083.36, -172.89) * mm});
            skLineSegment(sketch, "E46.5.5.5", {"start": v(-1088.56, -197.75) * mm, "end": v(-1093.14, -183.82) * mm});
            skLineSegment(sketch, "E46.6.0.0", {"start": v(-994.2, 199.25) * mm, "end": v(-1008.56, 202.25) * mm});
            skLineSegment(sketch, "E46.6.0.1", {"start": v(-984.43, 210.17) * mm, "end": v(-994.2, 199.25) * mm});
            skLineSegment(sketch, "E46.6.0.2", {"start": v(-989, 224.1) * mm, "end": v(-984.43, 210.17) * mm});
            skLineSegment(sketch, "E46.6.0.3", {"start": v(-1003.36, 227.11) * mm, "end": v(-989, 224.1) * mm});
            skLineSegment(sketch, "E46.6.0.4", {"start": v(-1013.14, 216.18) * mm, "end": v(-1003.36, 227.11) * mm});
            skLineSegment(sketch, "E46.6.0.5", {"start": v(-1008.56, 202.25) * mm, "end": v(-1013.14, 216.18) * mm});
            skLineSegment(sketch, "E46.6.1.0", {"start": v(-994.2, 119.25) * mm, "end": v(-1008.56, 122.25) * mm});
            skLineSegment(sketch, "E46.6.1.1", {"start": v(-984.43, 130.17) * mm, "end": v(-994.2, 119.25) * mm});
            skLineSegment(sketch, "E46.6.1.2", {"start": v(-989, 144.1) * mm, "end": v(-984.43, 130.17) * mm});
            skLineSegment(sketch, "E46.6.1.3", {"start": v(-1003.36, 147.11) * mm, "end": v(-989, 144.1) * mm});
            skLineSegment(sketch, "E46.6.1.4", {"start": v(-1013.14, 136.18) * mm, "end": v(-1003.36, 147.11) * mm});
            skLineSegment(sketch, "E46.6.1.5", {"start": v(-1008.56, 122.25) * mm, "end": v(-1013.14, 136.18) * mm});
            skLineSegment(sketch, "E46.6.2.0", {"start": v(-994.2, 39.25) * mm, "end": v(-1008.56, 42.25) * mm});
            skLineSegment(sketch, "E46.6.2.1", {"start": v(-984.43, 50.17) * mm, "end": v(-994.2, 39.25) * mm});
            skLineSegment(sketch, "E46.6.2.2", {"start": v(-989, 64.1) * mm, "end": v(-984.43, 50.17) * mm});
            skLineSegment(sketch, "E46.6.2.3", {"start": v(-1003.36, 67.11) * mm, "end": v(-989, 64.1) * mm});
            skLineSegment(sketch, "E46.6.2.4", {"start": v(-1013.14, 56.18) * mm, "end": v(-1003.36, 67.11) * mm});
            skLineSegment(sketch, "E46.6.2.5", {"start": v(-1008.56, 42.25) * mm, "end": v(-1013.14, 56.18) * mm});
            skLineSegment(sketch, "E46.6.3.0", {"start": v(-994.2, -40.75) * mm, "end": v(-1008.56, -37.75) * mm});
            skLineSegment(sketch, "E46.6.3.1", {"start": v(-984.43, -29.83) * mm, "end": v(-994.2, -40.75) * mm});
            skLineSegment(sketch, "E46.6.3.2", {"start": v(-989, -15.9) * mm, "end": v(-984.43, -29.83) * mm});
            skLineSegment(sketch, "E46.6.3.3", {"start": v(-1003.36, -12.89) * mm, "end": v(-989, -15.9) * mm});
            skLineSegment(sketch, "E46.6.3.4", {"start": v(-1013.14, -23.82) * mm, "end": v(-1003.36, -12.89) * mm});
            skLineSegment(sketch, "E46.6.3.5", {"start": v(-1008.56, -37.75) * mm, "end": v(-1013.14, -23.82) * mm});
            skLineSegment(sketch, "E46.6.4.0", {"start": v(-994.2, -120.75) * mm, "end": v(-1008.56, -117.75) * mm});
            skLineSegment(sketch, "E46.6.4.1", {"start": v(-984.43, -109.83) * mm, "end": v(-994.2, -120.75) * mm});
            skLineSegment(sketch, "E46.6.4.2", {"start": v(-989, -95.9) * mm, "end": v(-984.43, -109.83) * mm});
            skLineSegment(sketch, "E46.6.4.3", {"start": v(-1003.36, -92.89) * mm, "end": v(-989, -95.9) * mm});
            skLineSegment(sketch, "E46.6.4.4", {"start": v(-1013.14, -103.82) * mm, "end": v(-1003.36, -92.89) * mm});
            skLineSegment(sketch, "E46.6.4.5", {"start": v(-1008.56, -117.75) * mm, "end": v(-1013.14, -103.82) * mm});
            skLineSegment(sketch, "E46.6.5.0", {"start": v(-994.2, -200.75) * mm, "end": v(-1008.56, -197.75) * mm});
            skLineSegment(sketch, "E46.6.5.1", {"start": v(-984.43, -189.83) * mm, "end": v(-994.2, -200.75) * mm});
            skLineSegment(sketch, "E46.6.5.2", {"start": v(-989, -175.9) * mm, "end": v(-984.43, -189.83) * mm});
            skLineSegment(sketch, "E46.6.5.3", {"start": v(-1003.36, -172.89) * mm, "end": v(-989, -175.9) * mm});
            skLineSegment(sketch, "E46.6.5.4", {"start": v(-1013.14, -183.82) * mm, "end": v(-1003.36, -172.89) * mm});
            skLineSegment(sketch, "E46.6.5.5", {"start": v(-1008.56, -197.75) * mm, "end": v(-1013.14, -183.82) * mm});
            skLineSegment(sketch, "E46.7.0.0", {"start": v(-914.2, 199.25) * mm, "end": v(-928.56, 202.25) * mm});
            skLineSegment(sketch, "E46.7.0.1", {"start": v(-904.43, 210.17) * mm, "end": v(-914.2, 199.25) * mm});
            skLineSegment(sketch, "E46.7.0.2", {"start": v(-909, 224.1) * mm, "end": v(-904.43, 210.17) * mm});
            skLineSegment(sketch, "E46.7.0.3", {"start": v(-923.36, 227.11) * mm, "end": v(-909, 224.1) * mm});
            skLineSegment(sketch, "E46.7.0.4", {"start": v(-933.14, 216.18) * mm, "end": v(-923.36, 227.11) * mm});
            skLineSegment(sketch, "E46.7.0.5", {"start": v(-928.56, 202.25) * mm, "end": v(-933.14, 216.18) * mm});
            skLineSegment(sketch, "E46.7.1.0", {"start": v(-914.2, 119.25) * mm, "end": v(-928.56, 122.25) * mm});
            skLineSegment(sketch, "E46.7.1.1", {"start": v(-904.43, 130.17) * mm, "end": v(-914.2, 119.25) * mm});
            skLineSegment(sketch, "E46.7.1.2", {"start": v(-909, 144.1) * mm, "end": v(-904.43, 130.17) * mm});
            skLineSegment(sketch, "E46.7.1.3", {"start": v(-923.36, 147.11) * mm, "end": v(-909, 144.1) * mm});
            skLineSegment(sketch, "E46.7.1.4", {"start": v(-933.14, 136.18) * mm, "end": v(-923.36, 147.11) * mm});
            skLineSegment(sketch, "E46.7.1.5", {"start": v(-928.56, 122.25) * mm, "end": v(-933.14, 136.18) * mm});
            skLineSegment(sketch, "E46.7.2.0", {"start": v(-914.2, 39.25) * mm, "end": v(-928.56, 42.25) * mm});
            skLineSegment(sketch, "E46.7.2.1", {"start": v(-904.43, 50.17) * mm, "end": v(-914.2, 39.25) * mm});
            skLineSegment(sketch, "E46.7.2.2", {"start": v(-909, 64.1) * mm, "end": v(-904.43, 50.17) * mm});
            skLineSegment(sketch, "E46.7.2.3", {"start": v(-923.36, 67.11) * mm, "end": v(-909, 64.1) * mm});
            skLineSegment(sketch, "E46.7.2.4", {"start": v(-933.14, 56.18) * mm, "end": v(-923.36, 67.11) * mm});
            skLineSegment(sketch, "E46.7.2.5", {"start": v(-928.56, 42.25) * mm, "end": v(-933.14, 56.18) * mm});
            skLineSegment(sketch, "E46.7.3.0", {"start": v(-914.2, -40.75) * mm, "end": v(-928.56, -37.75) * mm});
            skLineSegment(sketch, "E46.7.3.1", {"start": v(-904.43, -29.83) * mm, "end": v(-914.2, -40.75) * mm});
            skLineSegment(sketch, "E46.7.3.2", {"start": v(-909, -15.9) * mm, "end": v(-904.43, -29.83) * mm});
            skLineSegment(sketch, "E46.7.3.3", {"start": v(-923.36, -12.89) * mm, "end": v(-909, -15.9) * mm});
            skLineSegment(sketch, "E46.7.3.4", {"start": v(-933.14, -23.82) * mm, "end": v(-923.36, -12.89) * mm});
            skLineSegment(sketch, "E46.7.3.5", {"start": v(-928.56, -37.75) * mm, "end": v(-933.14, -23.82) * mm});
            skLineSegment(sketch, "E46.7.4.0", {"start": v(-914.2, -120.75) * mm, "end": v(-928.56, -117.75) * mm});
            skLineSegment(sketch, "E46.7.4.1", {"start": v(-904.43, -109.83) * mm, "end": v(-914.2, -120.75) * mm});
            skLineSegment(sketch, "E46.7.4.2", {"start": v(-909, -95.9) * mm, "end": v(-904.43, -109.83) * mm});
            skLineSegment(sketch, "E46.7.4.3", {"start": v(-923.36, -92.89) * mm, "end": v(-909, -95.9) * mm});
            skLineSegment(sketch, "E46.7.4.4", {"start": v(-933.14, -103.82) * mm, "end": v(-923.36, -92.89) * mm});
            skLineSegment(sketch, "E46.7.4.5", {"start": v(-928.56, -117.75) * mm, "end": v(-933.14, -103.82) * mm});
            skLineSegment(sketch, "E46.7.5.0", {"start": v(-914.2, -200.75) * mm, "end": v(-928.56, -197.75) * mm});
            skLineSegment(sketch, "E46.7.5.1", {"start": v(-904.43, -189.83) * mm, "end": v(-914.2, -200.75) * mm});
            skLineSegment(sketch, "E46.7.5.2", {"start": v(-909, -175.9) * mm, "end": v(-904.43, -189.83) * mm});
            skLineSegment(sketch, "E46.7.5.3", {"start": v(-923.36, -172.89) * mm, "end": v(-909, -175.9) * mm});
            skLineSegment(sketch, "E46.7.5.4", {"start": v(-933.14, -183.82) * mm, "end": v(-923.36, -172.89) * mm});
            skLineSegment(sketch, "E46.7.5.5", {"start": v(-928.56, -197.75) * mm, "end": v(-933.14, -183.82) * mm});
            skLineSegment(sketch, "E46.8.0.0", {"start": v(-834.2, 199.25) * mm, "end": v(-848.56, 202.25) * mm});
            skLineSegment(sketch, "E46.8.0.1", {"start": v(-824.43, 210.17) * mm, "end": v(-834.2, 199.25) * mm});
            skLineSegment(sketch, "E46.8.0.2", {"start": v(-829, 224.1) * mm, "end": v(-824.43, 210.17) * mm});
            skLineSegment(sketch, "E46.8.0.3", {"start": v(-843.36, 227.11) * mm, "end": v(-829, 224.1) * mm});
            skLineSegment(sketch, "E46.8.0.4", {"start": v(-853.14, 216.18) * mm, "end": v(-843.36, 227.11) * mm});
            skLineSegment(sketch, "E46.8.0.5", {"start": v(-848.56, 202.25) * mm, "end": v(-853.14, 216.18) * mm});
            skLineSegment(sketch, "E46.8.1.0", {"start": v(-834.2, 119.25) * mm, "end": v(-848.56, 122.25) * mm});
            skLineSegment(sketch, "E46.8.1.1", {"start": v(-824.43, 130.17) * mm, "end": v(-834.2, 119.25) * mm});
            skLineSegment(sketch, "E46.8.1.2", {"start": v(-829, 144.1) * mm, "end": v(-824.43, 130.17) * mm});
            skLineSegment(sketch, "E46.8.1.3", {"start": v(-843.36, 147.11) * mm, "end": v(-829, 144.1) * mm});
            skLineSegment(sketch, "E46.8.1.4", {"start": v(-853.14, 136.18) * mm, "end": v(-843.36, 147.11) * mm});
            skLineSegment(sketch, "E46.8.1.5", {"start": v(-848.56, 122.25) * mm, "end": v(-853.14, 136.18) * mm});
            skLineSegment(sketch, "E46.8.2.0", {"start": v(-834.2, 39.25) * mm, "end": v(-848.56, 42.25) * mm});
            skLineSegment(sketch, "E46.8.2.1", {"start": v(-824.43, 50.17) * mm, "end": v(-834.2, 39.25) * mm});
            skLineSegment(sketch, "E46.8.2.2", {"start": v(-829, 64.1) * mm, "end": v(-824.43, 50.17) * mm});
            skLineSegment(sketch, "E46.8.2.3", {"start": v(-843.36, 67.11) * mm, "end": v(-829, 64.1) * mm});
            skLineSegment(sketch, "E46.8.2.4", {"start": v(-853.14, 56.18) * mm, "end": v(-843.36, 67.11) * mm});
            skLineSegment(sketch, "E46.8.2.5", {"start": v(-848.56, 42.25) * mm, "end": v(-853.14, 56.18) * mm});
            skLineSegment(sketch, "E46.8.3.0", {"start": v(-834.2, -40.75) * mm, "end": v(-848.56, -37.75) * mm});
            skLineSegment(sketch, "E46.8.3.1", {"start": v(-824.43, -29.83) * mm, "end": v(-834.2, -40.75) * mm});
            skLineSegment(sketch, "E46.8.3.2", {"start": v(-829, -15.9) * mm, "end": v(-824.43, -29.83) * mm});
            skLineSegment(sketch, "E46.8.3.3", {"start": v(-843.36, -12.89) * mm, "end": v(-829, -15.9) * mm});
            skLineSegment(sketch, "E46.8.3.4", {"start": v(-853.14, -23.82) * mm, "end": v(-843.36, -12.89) * mm});
            skLineSegment(sketch, "E46.8.3.5", {"start": v(-848.56, -37.75) * mm, "end": v(-853.14, -23.82) * mm});
            skLineSegment(sketch, "E46.8.4.0", {"start": v(-834.2, -120.75) * mm, "end": v(-848.56, -117.75) * mm});
            skLineSegment(sketch, "E46.8.4.1", {"start": v(-824.43, -109.83) * mm, "end": v(-834.2, -120.75) * mm});
            skLineSegment(sketch, "E46.8.4.2", {"start": v(-829, -95.9) * mm, "end": v(-824.43, -109.83) * mm});
            skLineSegment(sketch, "E46.8.4.3", {"start": v(-843.36, -92.89) * mm, "end": v(-829, -95.9) * mm});
            skLineSegment(sketch, "E46.8.4.4", {"start": v(-853.14, -103.82) * mm, "end": v(-843.36, -92.89) * mm});
            skLineSegment(sketch, "E46.8.4.5", {"start": v(-848.56, -117.75) * mm, "end": v(-853.14, -103.82) * mm});
            skLineSegment(sketch, "E46.8.5.0", {"start": v(-834.2, -200.75) * mm, "end": v(-848.56, -197.75) * mm});
            skLineSegment(sketch, "E46.8.5.1", {"start": v(-824.43, -189.83) * mm, "end": v(-834.2, -200.75) * mm});
            skLineSegment(sketch, "E46.8.5.2", {"start": v(-829, -175.9) * mm, "end": v(-824.43, -189.83) * mm});
            skLineSegment(sketch, "E46.8.5.3", {"start": v(-843.36, -172.89) * mm, "end": v(-829, -175.9) * mm});
            skLineSegment(sketch, "E46.8.5.4", {"start": v(-853.14, -183.82) * mm, "end": v(-843.36, -172.89) * mm});
            skLineSegment(sketch, "E46.8.5.5", {"start": v(-848.56, -197.75) * mm, "end": v(-853.14, -183.82) * mm});
            skLineSegment(sketch, "E46.9.0.0", {"start": v(-754.2, 199.25) * mm, "end": v(-768.56, 202.25) * mm});
            skLineSegment(sketch, "E46.9.0.1", {"start": v(-744.43, 210.17) * mm, "end": v(-754.2, 199.25) * mm});
            skLineSegment(sketch, "E46.9.0.2", {"start": v(-749, 224.1) * mm, "end": v(-744.43, 210.17) * mm});
            skLineSegment(sketch, "E46.9.0.3", {"start": v(-763.36, 227.11) * mm, "end": v(-749, 224.1) * mm});
            skLineSegment(sketch, "E46.9.0.4", {"start": v(-773.14, 216.18) * mm, "end": v(-763.36, 227.11) * mm});
            skLineSegment(sketch, "E46.9.0.5", {"start": v(-768.56, 202.25) * mm, "end": v(-773.14, 216.18) * mm});
            skLineSegment(sketch, "E46.9.1.0", {"start": v(-754.2, 119.25) * mm, "end": v(-768.56, 122.25) * mm});
            skLineSegment(sketch, "E46.9.1.1", {"start": v(-744.43, 130.17) * mm, "end": v(-754.2, 119.25) * mm});
            skLineSegment(sketch, "E46.9.1.2", {"start": v(-749, 144.1) * mm, "end": v(-744.43, 130.17) * mm});
            skLineSegment(sketch, "E46.9.1.3", {"start": v(-763.36, 147.11) * mm, "end": v(-749, 144.1) * mm});
            skLineSegment(sketch, "E46.9.1.4", {"start": v(-773.14, 136.18) * mm, "end": v(-763.36, 147.11) * mm});
            skLineSegment(sketch, "E46.9.1.5", {"start": v(-768.56, 122.25) * mm, "end": v(-773.14, 136.18) * mm});
            skLineSegment(sketch, "E46.9.2.0", {"start": v(-754.2, 39.25) * mm, "end": v(-768.56, 42.25) * mm});
            skLineSegment(sketch, "E46.9.2.1", {"start": v(-744.43, 50.17) * mm, "end": v(-754.2, 39.25) * mm});
            skLineSegment(sketch, "E46.9.2.2", {"start": v(-749, 64.1) * mm, "end": v(-744.43, 50.17) * mm});
            skLineSegment(sketch, "E46.9.2.3", {"start": v(-763.36, 67.11) * mm, "end": v(-749, 64.1) * mm});
            skLineSegment(sketch, "E46.9.2.4", {"start": v(-773.14, 56.18) * mm, "end": v(-763.36, 67.11) * mm});
            skLineSegment(sketch, "E46.9.2.5", {"start": v(-768.56, 42.25) * mm, "end": v(-773.14, 56.18) * mm});
            skLineSegment(sketch, "E46.9.3.0", {"start": v(-754.2, -40.75) * mm, "end": v(-768.56, -37.75) * mm});
            skLineSegment(sketch, "E46.9.3.1", {"start": v(-744.43, -29.83) * mm, "end": v(-754.2, -40.75) * mm});
            skLineSegment(sketch, "E46.9.3.2", {"start": v(-749, -15.9) * mm, "end": v(-744.43, -29.83) * mm});
            skLineSegment(sketch, "E46.9.3.3", {"start": v(-763.36, -12.89) * mm, "end": v(-749, -15.9) * mm});
            skLineSegment(sketch, "E46.9.3.4", {"start": v(-773.14, -23.82) * mm, "end": v(-763.36, -12.89) * mm});
            skLineSegment(sketch, "E46.9.3.5", {"start": v(-768.56, -37.75) * mm, "end": v(-773.14, -23.82) * mm});
            skLineSegment(sketch, "E46.9.4.0", {"start": v(-754.2, -120.75) * mm, "end": v(-768.56, -117.75) * mm});
            skLineSegment(sketch, "E46.9.4.1", {"start": v(-744.43, -109.83) * mm, "end": v(-754.2, -120.75) * mm});
            skLineSegment(sketch, "E46.9.4.2", {"start": v(-749, -95.9) * mm, "end": v(-744.43, -109.83) * mm});
            skLineSegment(sketch, "E46.9.4.3", {"start": v(-763.36, -92.89) * mm, "end": v(-749, -95.9) * mm});
            skLineSegment(sketch, "E46.9.4.4", {"start": v(-773.14, -103.82) * mm, "end": v(-763.36, -92.89) * mm});
            skLineSegment(sketch, "E46.9.4.5", {"start": v(-768.56, -117.75) * mm, "end": v(-773.14, -103.82) * mm});
            skLineSegment(sketch, "E46.9.5.0", {"start": v(-754.2, -200.75) * mm, "end": v(-768.56, -197.75) * mm});
            skLineSegment(sketch, "E46.9.5.1", {"start": v(-744.43, -189.83) * mm, "end": v(-754.2, -200.75) * mm});
            skLineSegment(sketch, "E46.9.5.2", {"start": v(-749, -175.9) * mm, "end": v(-744.43, -189.83) * mm});
            skLineSegment(sketch, "E46.9.5.3", {"start": v(-763.36, -172.89) * mm, "end": v(-749, -175.9) * mm});
            skLineSegment(sketch, "E46.9.5.4", {"start": v(-773.14, -183.82) * mm, "end": v(-763.36, -172.89) * mm});
            skLineSegment(sketch, "E46.9.5.5", {"start": v(-768.56, -197.75) * mm, "end": v(-773.14, -183.82) * mm});
            skLineSegment(sketch, "E46.10.0.0", {"start": v(-674.2, 199.25) * mm, "end": v(-688.56, 202.25) * mm});
            skLineSegment(sketch, "E46.10.0.1", {"start": v(-664.43, 210.17) * mm, "end": v(-674.2, 199.25) * mm});
            skLineSegment(sketch, "E46.10.0.2", {"start": v(-669, 224.1) * mm, "end": v(-664.43, 210.17) * mm});
            skLineSegment(sketch, "E46.10.0.3", {"start": v(-683.36, 227.11) * mm, "end": v(-669, 224.1) * mm});
            skLineSegment(sketch, "E46.10.0.4", {"start": v(-693.14, 216.18) * mm, "end": v(-683.36, 227.11) * mm});
            skLineSegment(sketch, "E46.10.0.5", {"start": v(-688.56, 202.25) * mm, "end": v(-693.14, 216.18) * mm});
            skLineSegment(sketch, "E46.10.1.0", {"start": v(-674.2, 119.25) * mm, "end": v(-688.56, 122.25) * mm});
            skLineSegment(sketch, "E46.10.1.1", {"start": v(-664.43, 130.17) * mm, "end": v(-674.2, 119.25) * mm});
            skLineSegment(sketch, "E46.10.1.2", {"start": v(-669, 144.1) * mm, "end": v(-664.43, 130.17) * mm});
            skLineSegment(sketch, "E46.10.1.3", {"start": v(-683.36, 147.11) * mm, "end": v(-669, 144.1) * mm});
            skLineSegment(sketch, "E46.10.1.4", {"start": v(-693.14, 136.18) * mm, "end": v(-683.36, 147.11) * mm});
            skLineSegment(sketch, "E46.10.1.5", {"start": v(-688.56, 122.25) * mm, "end": v(-693.14, 136.18) * mm});
            skLineSegment(sketch, "E46.10.2.0", {"start": v(-674.2, 39.25) * mm, "end": v(-688.56, 42.25) * mm});
            skLineSegment(sketch, "E46.10.2.1", {"start": v(-664.43, 50.17) * mm, "end": v(-674.2, 39.25) * mm});
            skLineSegment(sketch, "E46.10.2.2", {"start": v(-669, 64.1) * mm, "end": v(-664.43, 50.17) * mm});
            skLineSegment(sketch, "E46.10.2.3", {"start": v(-683.36, 67.11) * mm, "end": v(-669, 64.1) * mm});
            skLineSegment(sketch, "E46.10.2.4", {"start": v(-693.14, 56.18) * mm, "end": v(-683.36, 67.11) * mm});
            skLineSegment(sketch, "E46.10.2.5", {"start": v(-688.56, 42.25) * mm, "end": v(-693.14, 56.18) * mm});
            skLineSegment(sketch, "E46.10.3.0", {"start": v(-674.2, -40.75) * mm, "end": v(-688.56, -37.75) * mm});
            skLineSegment(sketch, "E46.10.3.1", {"start": v(-664.43, -29.83) * mm, "end": v(-674.2, -40.75) * mm});
            skLineSegment(sketch, "E46.10.3.2", {"start": v(-669, -15.9) * mm, "end": v(-664.43, -29.83) * mm});
            skLineSegment(sketch, "E46.10.3.3", {"start": v(-683.36, -12.89) * mm, "end": v(-669, -15.9) * mm});
            skLineSegment(sketch, "E46.10.3.4", {"start": v(-693.14, -23.82) * mm, "end": v(-683.36, -12.89) * mm});
            skLineSegment(sketch, "E46.10.3.5", {"start": v(-688.56, -37.75) * mm, "end": v(-693.14, -23.82) * mm});
            skLineSegment(sketch, "E46.10.4.0", {"start": v(-674.2, -120.75) * mm, "end": v(-688.56, -117.75) * mm});
            skLineSegment(sketch, "E46.10.4.1", {"start": v(-664.43, -109.83) * mm, "end": v(-674.2, -120.75) * mm});
            skLineSegment(sketch, "E46.10.4.2", {"start": v(-669, -95.9) * mm, "end": v(-664.43, -109.83) * mm});
            skLineSegment(sketch, "E46.10.4.3", {"start": v(-683.36, -92.89) * mm, "end": v(-669, -95.9) * mm});
            skLineSegment(sketch, "E46.10.4.4", {"start": v(-693.14, -103.82) * mm, "end": v(-683.36, -92.89) * mm});
            skLineSegment(sketch, "E46.10.4.5", {"start": v(-688.56, -117.75) * mm, "end": v(-693.14, -103.82) * mm});
            skLineSegment(sketch, "E46.10.5.0", {"start": v(-674.2, -200.75) * mm, "end": v(-688.56, -197.75) * mm});
            skLineSegment(sketch, "E46.10.5.1", {"start": v(-664.43, -189.83) * mm, "end": v(-674.2, -200.75) * mm});
            skLineSegment(sketch, "E46.10.5.2", {"start": v(-669, -175.9) * mm, "end": v(-664.43, -189.83) * mm});
            skLineSegment(sketch, "E46.10.5.3", {"start": v(-683.36, -172.89) * mm, "end": v(-669, -175.9) * mm});
            skLineSegment(sketch, "E46.10.5.4", {"start": v(-693.14, -183.82) * mm, "end": v(-683.36, -172.89) * mm});
            skLineSegment(sketch, "E46.10.5.5", {"start": v(-688.56, -197.75) * mm, "end": v(-693.14, -183.82) * mm});
            skLineSegment(sketch, "E46.11.0.0", {"start": v(-594.2, 199.25) * mm, "end": v(-608.56, 202.25) * mm});
            skLineSegment(sketch, "E46.11.0.1", {"start": v(-584.43, 210.17) * mm, "end": v(-594.2, 199.25) * mm});
            skLineSegment(sketch, "E46.11.0.2", {"start": v(-589, 224.1) * mm, "end": v(-584.43, 210.17) * mm});
            skLineSegment(sketch, "E46.11.0.3", {"start": v(-603.36, 227.11) * mm, "end": v(-589, 224.1) * mm});
            skLineSegment(sketch, "E46.11.0.4", {"start": v(-613.14, 216.18) * mm, "end": v(-603.36, 227.11) * mm});
            skLineSegment(sketch, "E46.11.0.5", {"start": v(-608.56, 202.25) * mm, "end": v(-613.14, 216.18) * mm});
            skLineSegment(sketch, "E46.11.1.0", {"start": v(-594.2, 119.25) * mm, "end": v(-608.56, 122.25) * mm});
            skLineSegment(sketch, "E46.11.1.1", {"start": v(-584.43, 130.17) * mm, "end": v(-594.2, 119.25) * mm});
            skLineSegment(sketch, "E46.11.1.2", {"start": v(-589, 144.1) * mm, "end": v(-584.43, 130.17) * mm});
            skLineSegment(sketch, "E46.11.1.3", {"start": v(-603.36, 147.11) * mm, "end": v(-589, 144.1) * mm});
            skLineSegment(sketch, "E46.11.1.4", {"start": v(-613.14, 136.18) * mm, "end": v(-603.36, 147.11) * mm});
            skLineSegment(sketch, "E46.11.1.5", {"start": v(-608.56, 122.25) * mm, "end": v(-613.14, 136.18) * mm});
            skLineSegment(sketch, "E46.11.2.0", {"start": v(-594.2, 39.25) * mm, "end": v(-608.56, 42.25) * mm});
            skLineSegment(sketch, "E46.11.2.1", {"start": v(-584.43, 50.17) * mm, "end": v(-594.2, 39.25) * mm});
            skLineSegment(sketch, "E46.11.2.2", {"start": v(-589, 64.1) * mm, "end": v(-584.43, 50.17) * mm});
            skLineSegment(sketch, "E46.11.2.3", {"start": v(-603.36, 67.11) * mm, "end": v(-589, 64.1) * mm});
            skLineSegment(sketch, "E46.11.2.4", {"start": v(-613.14, 56.18) * mm, "end": v(-603.36, 67.11) * mm});
            skLineSegment(sketch, "E46.11.2.5", {"start": v(-608.56, 42.25) * mm, "end": v(-613.14, 56.18) * mm});
            skLineSegment(sketch, "E46.11.3.0", {"start": v(-594.2, -40.75) * mm, "end": v(-608.56, -37.75) * mm});
            skLineSegment(sketch, "E46.11.3.1", {"start": v(-584.43, -29.83) * mm, "end": v(-594.2, -40.75) * mm});
            skLineSegment(sketch, "E46.11.3.2", {"start": v(-589, -15.9) * mm, "end": v(-584.43, -29.83) * mm});
            skLineSegment(sketch, "E46.11.3.3", {"start": v(-603.36, -12.89) * mm, "end": v(-589, -15.9) * mm});
            skLineSegment(sketch, "E46.11.3.4", {"start": v(-613.14, -23.82) * mm, "end": v(-603.36, -12.89) * mm});
            skLineSegment(sketch, "E46.11.3.5", {"start": v(-608.56, -37.75) * mm, "end": v(-613.14, -23.82) * mm});
            skLineSegment(sketch, "E46.11.4.0", {"start": v(-594.2, -120.75) * mm, "end": v(-608.56, -117.75) * mm});
            skLineSegment(sketch, "E46.11.4.1", {"start": v(-584.43, -109.83) * mm, "end": v(-594.2, -120.75) * mm});
            skLineSegment(sketch, "E46.11.4.2", {"start": v(-589, -95.9) * mm, "end": v(-584.43, -109.83) * mm});
            skLineSegment(sketch, "E46.11.4.3", {"start": v(-603.36, -92.89) * mm, "end": v(-589, -95.9) * mm});
            skLineSegment(sketch, "E46.11.4.4", {"start": v(-613.14, -103.82) * mm, "end": v(-603.36, -92.89) * mm});
            skLineSegment(sketch, "E46.11.4.5", {"start": v(-608.56, -117.75) * mm, "end": v(-613.14, -103.82) * mm});
            skLineSegment(sketch, "E46.11.5.0", {"start": v(-594.2, -200.75) * mm, "end": v(-608.56, -197.75) * mm});
            skLineSegment(sketch, "E46.11.5.1", {"start": v(-584.43, -189.83) * mm, "end": v(-594.2, -200.75) * mm});
            skLineSegment(sketch, "E46.11.5.2", {"start": v(-589, -175.9) * mm, "end": v(-584.43, -189.83) * mm});
            skLineSegment(sketch, "E46.11.5.3", {"start": v(-603.36, -172.89) * mm, "end": v(-589, -175.9) * mm});
            skLineSegment(sketch, "E46.11.5.4", {"start": v(-613.14, -183.82) * mm, "end": v(-603.36, -172.89) * mm});
            skLineSegment(sketch, "E46.11.5.5", {"start": v(-608.56, -197.75) * mm, "end": v(-613.14, -183.82) * mm});
            skLineSegment(sketch, "E46.12.0.0", {"start": v(-514.2, 199.25) * mm, "end": v(-528.56, 202.25) * mm});
            skLineSegment(sketch, "E46.12.0.1", {"start": v(-504.43, 210.17) * mm, "end": v(-514.2, 199.25) * mm});
            skLineSegment(sketch, "E46.12.0.2", {"start": v(-509, 224.1) * mm, "end": v(-504.43, 210.17) * mm});
            skLineSegment(sketch, "E46.12.0.3", {"start": v(-523.36, 227.11) * mm, "end": v(-509, 224.1) * mm});
            skLineSegment(sketch, "E46.12.0.4", {"start": v(-533.14, 216.18) * mm, "end": v(-523.36, 227.11) * mm});
            skLineSegment(sketch, "E46.12.0.5", {"start": v(-528.56, 202.25) * mm, "end": v(-533.14, 216.18) * mm});
            skLineSegment(sketch, "E46.12.1.0", {"start": v(-514.2, 119.25) * mm, "end": v(-528.56, 122.25) * mm});
            skLineSegment(sketch, "E46.12.1.1", {"start": v(-504.43, 130.17) * mm, "end": v(-514.2, 119.25) * mm});
            skLineSegment(sketch, "E46.12.1.2", {"start": v(-509, 144.1) * mm, "end": v(-504.43, 130.17) * mm});
            skLineSegment(sketch, "E46.12.1.3", {"start": v(-523.36, 147.11) * mm, "end": v(-509, 144.1) * mm});
            skLineSegment(sketch, "E46.12.1.4", {"start": v(-533.14, 136.18) * mm, "end": v(-523.36, 147.11) * mm});
            skLineSegment(sketch, "E46.12.1.5", {"start": v(-528.56, 122.25) * mm, "end": v(-533.14, 136.18) * mm});
            skLineSegment(sketch, "E46.12.2.0", {"start": v(-514.2, 39.25) * mm, "end": v(-528.56, 42.25) * mm});
            skLineSegment(sketch, "E46.12.2.1", {"start": v(-504.43, 50.17) * mm, "end": v(-514.2, 39.25) * mm});
            skLineSegment(sketch, "E46.12.2.2", {"start": v(-509, 64.1) * mm, "end": v(-504.43, 50.17) * mm});
            skLineSegment(sketch, "E46.12.2.3", {"start": v(-523.36, 67.11) * mm, "end": v(-509, 64.1) * mm});
            skLineSegment(sketch, "E46.12.2.4", {"start": v(-533.14, 56.18) * mm, "end": v(-523.36, 67.11) * mm});
            skLineSegment(sketch, "E46.12.2.5", {"start": v(-528.56, 42.25) * mm, "end": v(-533.14, 56.18) * mm});
            skLineSegment(sketch, "E46.12.3.0", {"start": v(-514.2, -40.75) * mm, "end": v(-528.56, -37.75) * mm});
            skLineSegment(sketch, "E46.12.3.1", {"start": v(-504.43, -29.83) * mm, "end": v(-514.2, -40.75) * mm});
            skLineSegment(sketch, "E46.12.3.2", {"start": v(-509, -15.9) * mm, "end": v(-504.43, -29.83) * mm});
            skLineSegment(sketch, "E46.12.3.3", {"start": v(-523.36, -12.89) * mm, "end": v(-509, -15.9) * mm});
            skLineSegment(sketch, "E46.12.3.4", {"start": v(-533.14, -23.82) * mm, "end": v(-523.36, -12.89) * mm});
            skLineSegment(sketch, "E46.12.3.5", {"start": v(-528.56, -37.75) * mm, "end": v(-533.14, -23.82) * mm});
            skLineSegment(sketch, "E46.12.4.0", {"start": v(-514.2, -120.75) * mm, "end": v(-528.56, -117.75) * mm});
            skLineSegment(sketch, "E46.12.4.1", {"start": v(-504.43, -109.83) * mm, "end": v(-514.2, -120.75) * mm});
            skLineSegment(sketch, "E46.12.4.2", {"start": v(-509, -95.9) * mm, "end": v(-504.43, -109.83) * mm});
            skLineSegment(sketch, "E46.12.4.3", {"start": v(-523.36, -92.89) * mm, "end": v(-509, -95.9) * mm});
            skLineSegment(sketch, "E46.12.4.4", {"start": v(-533.14, -103.82) * mm, "end": v(-523.36, -92.89) * mm});
            skLineSegment(sketch, "E46.12.4.5", {"start": v(-528.56, -117.75) * mm, "end": v(-533.14, -103.82) * mm});
            skLineSegment(sketch, "E46.12.5.0", {"start": v(-514.2, -200.75) * mm, "end": v(-528.56, -197.75) * mm});
            skLineSegment(sketch, "E46.12.5.1", {"start": v(-504.43, -189.83) * mm, "end": v(-514.2, -200.75) * mm});
            skLineSegment(sketch, "E46.12.5.2", {"start": v(-509, -175.9) * mm, "end": v(-504.43, -189.83) * mm});
            skLineSegment(sketch, "E46.12.5.3", {"start": v(-523.36, -172.89) * mm, "end": v(-509, -175.9) * mm});
            skLineSegment(sketch, "E46.12.5.4", {"start": v(-533.14, -183.82) * mm, "end": v(-523.36, -172.89) * mm});
            skLineSegment(sketch, "E46.12.5.5", {"start": v(-528.56, -197.75) * mm, "end": v(-533.14, -183.82) * mm});
            skLineSegment(sketch, "E46.13.0.0", {"start": v(-434.2, 199.25) * mm, "end": v(-448.56, 202.25) * mm});
            skLineSegment(sketch, "E46.13.0.1", {"start": v(-424.43, 210.17) * mm, "end": v(-434.2, 199.25) * mm});
            skLineSegment(sketch, "E46.13.0.2", {"start": v(-429, 224.1) * mm, "end": v(-424.43, 210.17) * mm});
            skLineSegment(sketch, "E46.13.0.3", {"start": v(-443.36, 227.11) * mm, "end": v(-429, 224.1) * mm});
            skLineSegment(sketch, "E46.13.0.4", {"start": v(-453.14, 216.18) * mm, "end": v(-443.36, 227.11) * mm});
            skLineSegment(sketch, "E46.13.0.5", {"start": v(-448.56, 202.25) * mm, "end": v(-453.14, 216.18) * mm});
            skLineSegment(sketch, "E46.13.1.0", {"start": v(-434.2, 119.25) * mm, "end": v(-448.56, 122.25) * mm});
            skLineSegment(sketch, "E46.13.1.1", {"start": v(-424.43, 130.17) * mm, "end": v(-434.2, 119.25) * mm});
            skLineSegment(sketch, "E46.13.1.2", {"start": v(-429, 144.1) * mm, "end": v(-424.43, 130.17) * mm});
            skLineSegment(sketch, "E46.13.1.3", {"start": v(-443.36, 147.11) * mm, "end": v(-429, 144.1) * mm});
            skLineSegment(sketch, "E46.13.1.4", {"start": v(-453.14, 136.18) * mm, "end": v(-443.36, 147.11) * mm});
            skLineSegment(sketch, "E46.13.1.5", {"start": v(-448.56, 122.25) * mm, "end": v(-453.14, 136.18) * mm});
            skLineSegment(sketch, "E46.13.2.0", {"start": v(-434.2, 39.25) * mm, "end": v(-448.56, 42.25) * mm});
            skLineSegment(sketch, "E46.13.2.1", {"start": v(-424.43, 50.17) * mm, "end": v(-434.2, 39.25) * mm});
            skLineSegment(sketch, "E46.13.2.2", {"start": v(-429, 64.1) * mm, "end": v(-424.43, 50.17) * mm});
            skLineSegment(sketch, "E46.13.2.3", {"start": v(-443.36, 67.11) * mm, "end": v(-429, 64.1) * mm});
            skLineSegment(sketch, "E46.13.2.4", {"start": v(-453.14, 56.18) * mm, "end": v(-443.36, 67.11) * mm});
            skLineSegment(sketch, "E46.13.2.5", {"start": v(-448.56, 42.25) * mm, "end": v(-453.14, 56.18) * mm});
            skLineSegment(sketch, "E46.13.3.0", {"start": v(-434.2, -40.75) * mm, "end": v(-448.56, -37.75) * mm});
            skLineSegment(sketch, "E46.13.3.1", {"start": v(-424.43, -29.83) * mm, "end": v(-434.2, -40.75) * mm});
            skLineSegment(sketch, "E46.13.3.2", {"start": v(-429, -15.9) * mm, "end": v(-424.43, -29.83) * mm});
            skLineSegment(sketch, "E46.13.3.3", {"start": v(-443.36, -12.89) * mm, "end": v(-429, -15.9) * mm});
            skLineSegment(sketch, "E46.13.3.4", {"start": v(-453.14, -23.82) * mm, "end": v(-443.36, -12.89) * mm});
            skLineSegment(sketch, "E46.13.3.5", {"start": v(-448.56, -37.75) * mm, "end": v(-453.14, -23.82) * mm});
            skLineSegment(sketch, "E46.13.4.0", {"start": v(-434.2, -120.75) * mm, "end": v(-448.56, -117.75) * mm});
            skLineSegment(sketch, "E46.13.4.1", {"start": v(-424.43, -109.83) * mm, "end": v(-434.2, -120.75) * mm});
            skLineSegment(sketch, "E46.13.4.2", {"start": v(-429, -95.9) * mm, "end": v(-424.43, -109.83) * mm});
            skLineSegment(sketch, "E46.13.4.3", {"start": v(-443.36, -92.89) * mm, "end": v(-429, -95.9) * mm});
            skLineSegment(sketch, "E46.13.4.4", {"start": v(-453.14, -103.82) * mm, "end": v(-443.36, -92.89) * mm});
            skLineSegment(sketch, "E46.13.4.5", {"start": v(-448.56, -117.75) * mm, "end": v(-453.14, -103.82) * mm});
            skLineSegment(sketch, "E46.13.5.0", {"start": v(-434.2, -200.75) * mm, "end": v(-448.56, -197.75) * mm});
            skLineSegment(sketch, "E46.13.5.1", {"start": v(-424.43, -189.83) * mm, "end": v(-434.2, -200.75) * mm});
            skLineSegment(sketch, "E46.13.5.2", {"start": v(-429, -175.9) * mm, "end": v(-424.43, -189.83) * mm});
            skLineSegment(sketch, "E46.13.5.3", {"start": v(-443.36, -172.89) * mm, "end": v(-429, -175.9) * mm});
            skLineSegment(sketch, "E46.13.5.4", {"start": v(-453.14, -183.82) * mm, "end": v(-443.36, -172.89) * mm});
            skLineSegment(sketch, "E46.13.5.5", {"start": v(-448.56, -197.75) * mm, "end": v(-453.14, -183.82) * mm});
            skLineSegment(sketch, "E46.14.0.0", {"start": v(-354.2, 199.25) * mm, "end": v(-368.56, 202.25) * mm});
            skLineSegment(sketch, "E46.14.0.1", {"start": v(-344.43, 210.17) * mm, "end": v(-354.2, 199.25) * mm});
            skLineSegment(sketch, "E46.14.0.2", {"start": v(-349, 224.1) * mm, "end": v(-344.43, 210.17) * mm});
            skLineSegment(sketch, "E46.14.0.3", {"start": v(-363.36, 227.11) * mm, "end": v(-349, 224.1) * mm});
            skLineSegment(sketch, "E46.14.0.4", {"start": v(-373.14, 216.18) * mm, "end": v(-363.36, 227.11) * mm});
            skLineSegment(sketch, "E46.14.0.5", {"start": v(-368.56, 202.25) * mm, "end": v(-373.14, 216.18) * mm});
            skLineSegment(sketch, "E46.14.1.0", {"start": v(-354.2, 119.25) * mm, "end": v(-368.56, 122.25) * mm});
            skLineSegment(sketch, "E46.14.1.1", {"start": v(-344.43, 130.17) * mm, "end": v(-354.2, 119.25) * mm});
            skLineSegment(sketch, "E46.14.1.2", {"start": v(-349, 144.1) * mm, "end": v(-344.43, 130.17) * mm});
            skLineSegment(sketch, "E46.14.1.3", {"start": v(-363.36, 147.11) * mm, "end": v(-349, 144.1) * mm});
            skLineSegment(sketch, "E46.14.1.4", {"start": v(-373.14, 136.18) * mm, "end": v(-363.36, 147.11) * mm});
            skLineSegment(sketch, "E46.14.1.5", {"start": v(-368.56, 122.25) * mm, "end": v(-373.14, 136.18) * mm});
            skLineSegment(sketch, "E46.14.2.0", {"start": v(-354.2, 39.25) * mm, "end": v(-368.56, 42.25) * mm});
            skLineSegment(sketch, "E46.14.2.1", {"start": v(-344.43, 50.17) * mm, "end": v(-354.2, 39.25) * mm});
            skLineSegment(sketch, "E46.14.2.2", {"start": v(-349, 64.1) * mm, "end": v(-344.43, 50.17) * mm});
            skLineSegment(sketch, "E46.14.2.3", {"start": v(-363.36, 67.11) * mm, "end": v(-349, 64.1) * mm});
            skLineSegment(sketch, "E46.14.2.4", {"start": v(-373.14, 56.18) * mm, "end": v(-363.36, 67.11) * mm});
            skLineSegment(sketch, "E46.14.2.5", {"start": v(-368.56, 42.25) * mm, "end": v(-373.14, 56.18) * mm});
            skLineSegment(sketch, "E46.14.3.0", {"start": v(-354.2, -40.75) * mm, "end": v(-368.56, -37.75) * mm});
            skLineSegment(sketch, "E46.14.3.1", {"start": v(-344.43, -29.83) * mm, "end": v(-354.2, -40.75) * mm});
            skLineSegment(sketch, "E46.14.3.2", {"start": v(-349, -15.9) * mm, "end": v(-344.43, -29.83) * mm});
            skLineSegment(sketch, "E46.14.3.3", {"start": v(-363.36, -12.89) * mm, "end": v(-349, -15.9) * mm});
            skLineSegment(sketch, "E46.14.3.4", {"start": v(-373.14, -23.82) * mm, "end": v(-363.36, -12.89) * mm});
            skLineSegment(sketch, "E46.14.3.5", {"start": v(-368.56, -37.75) * mm, "end": v(-373.14, -23.82) * mm});
            skLineSegment(sketch, "E46.14.4.0", {"start": v(-354.2, -120.75) * mm, "end": v(-368.56, -117.75) * mm});
            skLineSegment(sketch, "E46.14.4.1", {"start": v(-344.43, -109.83) * mm, "end": v(-354.2, -120.75) * mm});
            skLineSegment(sketch, "E46.14.4.2", {"start": v(-349, -95.9) * mm, "end": v(-344.43, -109.83) * mm});
            skLineSegment(sketch, "E46.14.4.3", {"start": v(-363.36, -92.89) * mm, "end": v(-349, -95.9) * mm});
            skLineSegment(sketch, "E46.14.4.4", {"start": v(-373.14, -103.82) * mm, "end": v(-363.36, -92.89) * mm});
            skLineSegment(sketch, "E46.14.4.5", {"start": v(-368.56, -117.75) * mm, "end": v(-373.14, -103.82) * mm});
            skLineSegment(sketch, "E46.14.5.0", {"start": v(-354.2, -200.75) * mm, "end": v(-368.56, -197.75) * mm});
            skLineSegment(sketch, "E46.14.5.1", {"start": v(-344.43, -189.83) * mm, "end": v(-354.2, -200.75) * mm});
            skLineSegment(sketch, "E46.14.5.2", {"start": v(-349, -175.9) * mm, "end": v(-344.43, -189.83) * mm});
            skLineSegment(sketch, "E46.14.5.3", {"start": v(-363.36, -172.89) * mm, "end": v(-349, -175.9) * mm});
            skLineSegment(sketch, "E46.14.5.4", {"start": v(-373.14, -183.82) * mm, "end": v(-363.36, -172.89) * mm});
            skLineSegment(sketch, "E46.14.5.5", {"start": v(-368.56, -197.75) * mm, "end": v(-373.14, -183.82) * mm});
            skLineSegment(sketch, "E46.15.0.0", {"start": v(-274.2, 199.25) * mm, "end": v(-288.56, 202.25) * mm});
            skLineSegment(sketch, "E46.15.0.1", {"start": v(-264.43, 210.17) * mm, "end": v(-274.2, 199.25) * mm});
            skLineSegment(sketch, "E46.15.0.2", {"start": v(-269, 224.1) * mm, "end": v(-264.43, 210.17) * mm});
            skLineSegment(sketch, "E46.15.0.3", {"start": v(-283.36, 227.11) * mm, "end": v(-269, 224.1) * mm});
            skLineSegment(sketch, "E46.15.0.4", {"start": v(-293.14, 216.18) * mm, "end": v(-283.36, 227.11) * mm});
            skLineSegment(sketch, "E46.15.0.5", {"start": v(-288.56, 202.25) * mm, "end": v(-293.14, 216.18) * mm});
            skLineSegment(sketch, "E46.15.1.0", {"start": v(-274.2, 119.25) * mm, "end": v(-288.56, 122.25) * mm});
            skLineSegment(sketch, "E46.15.1.1", {"start": v(-264.43, 130.17) * mm, "end": v(-274.2, 119.25) * mm});
            skLineSegment(sketch, "E46.15.1.2", {"start": v(-269, 144.1) * mm, "end": v(-264.43, 130.17) * mm});
            skLineSegment(sketch, "E46.15.1.3", {"start": v(-283.36, 147.11) * mm, "end": v(-269, 144.1) * mm});
            skLineSegment(sketch, "E46.15.1.4", {"start": v(-293.14, 136.18) * mm, "end": v(-283.36, 147.11) * mm});
            skLineSegment(sketch, "E46.15.1.5", {"start": v(-288.56, 122.25) * mm, "end": v(-293.14, 136.18) * mm});
            skLineSegment(sketch, "E46.15.2.0", {"start": v(-274.2, 39.25) * mm, "end": v(-288.56, 42.25) * mm});
            skLineSegment(sketch, "E46.15.2.1", {"start": v(-264.43, 50.17) * mm, "end": v(-274.2, 39.25) * mm});
            skLineSegment(sketch, "E46.15.2.2", {"start": v(-269, 64.1) * mm, "end": v(-264.43, 50.17) * mm});
            skLineSegment(sketch, "E46.15.2.3", {"start": v(-283.36, 67.11) * mm, "end": v(-269, 64.1) * mm});
            skLineSegment(sketch, "E46.15.2.4", {"start": v(-293.14, 56.18) * mm, "end": v(-283.36, 67.11) * mm});
            skLineSegment(sketch, "E46.15.2.5", {"start": v(-288.56, 42.25) * mm, "end": v(-293.14, 56.18) * mm});
            skLineSegment(sketch, "E46.15.3.0", {"start": v(-274.2, -40.75) * mm, "end": v(-288.56, -37.75) * mm});
            skLineSegment(sketch, "E46.15.3.1", {"start": v(-264.43, -29.83) * mm, "end": v(-274.2, -40.75) * mm});
            skLineSegment(sketch, "E46.15.3.2", {"start": v(-269, -15.9) * mm, "end": v(-264.43, -29.83) * mm});
            skLineSegment(sketch, "E46.15.3.3", {"start": v(-283.36, -12.89) * mm, "end": v(-269, -15.9) * mm});
            skLineSegment(sketch, "E46.15.3.4", {"start": v(-293.14, -23.82) * mm, "end": v(-283.36, -12.89) * mm});
            skLineSegment(sketch, "E46.15.3.5", {"start": v(-288.56, -37.75) * mm, "end": v(-293.14, -23.82) * mm});
            skLineSegment(sketch, "E46.15.4.0", {"start": v(-274.2, -120.75) * mm, "end": v(-288.56, -117.75) * mm});
            skLineSegment(sketch, "E46.15.4.1", {"start": v(-264.43, -109.83) * mm, "end": v(-274.2, -120.75) * mm});
            skLineSegment(sketch, "E46.15.4.2", {"start": v(-269, -95.9) * mm, "end": v(-264.43, -109.83) * mm});
            skLineSegment(sketch, "E46.15.4.3", {"start": v(-283.36, -92.89) * mm, "end": v(-269, -95.9) * mm});
            skLineSegment(sketch, "E46.15.4.4", {"start": v(-293.14, -103.82) * mm, "end": v(-283.36, -92.89) * mm});
            skLineSegment(sketch, "E46.15.4.5", {"start": v(-288.56, -117.75) * mm, "end": v(-293.14, -103.82) * mm});
            skLineSegment(sketch, "E46.15.5.0", {"start": v(-274.2, -200.75) * mm, "end": v(-288.56, -197.75) * mm});
            skLineSegment(sketch, "E46.15.5.1", {"start": v(-264.43, -189.83) * mm, "end": v(-274.2, -200.75) * mm});
            skLineSegment(sketch, "E46.15.5.2", {"start": v(-269, -175.9) * mm, "end": v(-264.43, -189.83) * mm});
            skLineSegment(sketch, "E46.15.5.3", {"start": v(-283.36, -172.89) * mm, "end": v(-269, -175.9) * mm});
            skLineSegment(sketch, "E46.15.5.4", {"start": v(-293.14, -183.82) * mm, "end": v(-283.36, -172.89) * mm});
            skLineSegment(sketch, "E46.15.5.5", {"start": v(-288.56, -197.75) * mm, "end": v(-293.14, -183.82) * mm});
            skLineSegment(sketch, "E46.16.0.0", {"start": v(-194.2, 199.25) * mm, "end": v(-208.56, 202.25) * mm});
            skLineSegment(sketch, "E46.16.0.1", {"start": v(-184.43, 210.17) * mm, "end": v(-194.2, 199.25) * mm});
            skLineSegment(sketch, "E46.16.0.2", {"start": v(-189, 224.1) * mm, "end": v(-184.43, 210.17) * mm});
            skLineSegment(sketch, "E46.16.0.3", {"start": v(-203.36, 227.11) * mm, "end": v(-189, 224.1) * mm});
            skLineSegment(sketch, "E46.16.0.4", {"start": v(-213.14, 216.18) * mm, "end": v(-203.36, 227.11) * mm});
            skLineSegment(sketch, "E46.16.0.5", {"start": v(-208.56, 202.25) * mm, "end": v(-213.14, 216.18) * mm});
            skLineSegment(sketch, "E46.16.1.0", {"start": v(-194.2, 119.25) * mm, "end": v(-208.56, 122.25) * mm});
            skLineSegment(sketch, "E46.16.1.1", {"start": v(-184.43, 130.17) * mm, "end": v(-194.2, 119.25) * mm});
            skLineSegment(sketch, "E46.16.1.2", {"start": v(-189, 144.1) * mm, "end": v(-184.43, 130.17) * mm});
            skLineSegment(sketch, "E46.16.1.3", {"start": v(-203.36, 147.11) * mm, "end": v(-189, 144.1) * mm});
            skLineSegment(sketch, "E46.16.1.4", {"start": v(-213.14, 136.18) * mm, "end": v(-203.36, 147.11) * mm});
            skLineSegment(sketch, "E46.16.1.5", {"start": v(-208.56, 122.25) * mm, "end": v(-213.14, 136.18) * mm});
            skLineSegment(sketch, "E46.16.2.0", {"start": v(-194.2, 39.25) * mm, "end": v(-208.56, 42.25) * mm});
            skLineSegment(sketch, "E46.16.2.1", {"start": v(-184.43, 50.17) * mm, "end": v(-194.2, 39.25) * mm});
            skLineSegment(sketch, "E46.16.2.2", {"start": v(-189, 64.1) * mm, "end": v(-184.43, 50.17) * mm});
            skLineSegment(sketch, "E46.16.2.3", {"start": v(-203.36, 67.11) * mm, "end": v(-189, 64.1) * mm});
            skLineSegment(sketch, "E46.16.2.4", {"start": v(-213.14, 56.18) * mm, "end": v(-203.36, 67.11) * mm});
            skLineSegment(sketch, "E46.16.2.5", {"start": v(-208.56, 42.25) * mm, "end": v(-213.14, 56.18) * mm});
            skLineSegment(sketch, "E46.16.3.0", {"start": v(-194.2, -40.75) * mm, "end": v(-208.56, -37.75) * mm});
            skLineSegment(sketch, "E46.16.3.1", {"start": v(-184.43, -29.83) * mm, "end": v(-194.2, -40.75) * mm});
            skLineSegment(sketch, "E46.16.3.2", {"start": v(-189, -15.9) * mm, "end": v(-184.43, -29.83) * mm});
            skLineSegment(sketch, "E46.16.3.3", {"start": v(-203.36, -12.89) * mm, "end": v(-189, -15.9) * mm});
            skLineSegment(sketch, "E46.16.3.4", {"start": v(-213.14, -23.82) * mm, "end": v(-203.36, -12.89) * mm});
            skLineSegment(sketch, "E46.16.3.5", {"start": v(-208.56, -37.75) * mm, "end": v(-213.14, -23.82) * mm});
            skLineSegment(sketch, "E46.16.4.0", {"start": v(-194.2, -120.75) * mm, "end": v(-208.56, -117.75) * mm});
            skLineSegment(sketch, "E46.16.4.1", {"start": v(-184.43, -109.83) * mm, "end": v(-194.2, -120.75) * mm});
            skLineSegment(sketch, "E46.16.4.2", {"start": v(-189, -95.9) * mm, "end": v(-184.43, -109.83) * mm});
            skLineSegment(sketch, "E46.16.4.3", {"start": v(-203.36, -92.89) * mm, "end": v(-189, -95.9) * mm});
            skLineSegment(sketch, "E46.16.4.4", {"start": v(-213.14, -103.82) * mm, "end": v(-203.36, -92.89) * mm});
            skLineSegment(sketch, "E46.16.4.5", {"start": v(-208.56, -117.75) * mm, "end": v(-213.14, -103.82) * mm});
            skLineSegment(sketch, "E46.16.5.0", {"start": v(-194.2, -200.75) * mm, "end": v(-208.56, -197.75) * mm});
            skLineSegment(sketch, "E46.16.5.1", {"start": v(-184.43, -189.83) * mm, "end": v(-194.2, -200.75) * mm});
            skLineSegment(sketch, "E46.16.5.2", {"start": v(-189, -175.9) * mm, "end": v(-184.43, -189.83) * mm});
            skLineSegment(sketch, "E46.16.5.3", {"start": v(-203.36, -172.89) * mm, "end": v(-189, -175.9) * mm});
            skLineSegment(sketch, "E46.16.5.4", {"start": v(-213.14, -183.82) * mm, "end": v(-203.36, -172.89) * mm});
            skLineSegment(sketch, "E46.16.5.5", {"start": v(-208.56, -197.75) * mm, "end": v(-213.14, -183.82) * mm});
            skLineSegment(sketch, "E46.17.0.0", {"start": v(-114.2, 199.25) * mm, "end": v(-128.56, 202.25) * mm});
            skLineSegment(sketch, "E46.17.0.1", {"start": v(-104.43, 210.17) * mm, "end": v(-114.2, 199.25) * mm});
            skLineSegment(sketch, "E46.17.0.2", {"start": v(-109, 224.1) * mm, "end": v(-104.43, 210.17) * mm});
            skLineSegment(sketch, "E46.17.0.3", {"start": v(-123.36, 227.11) * mm, "end": v(-109, 224.1) * mm});
            skLineSegment(sketch, "E46.17.0.4", {"start": v(-133.14, 216.18) * mm, "end": v(-123.36, 227.11) * mm});
            skLineSegment(sketch, "E46.17.0.5", {"start": v(-128.56, 202.25) * mm, "end": v(-133.14, 216.18) * mm});
            skLineSegment(sketch, "E46.17.1.0", {"start": v(-114.2, 119.25) * mm, "end": v(-128.56, 122.25) * mm});
            skLineSegment(sketch, "E46.17.1.1", {"start": v(-104.43, 130.17) * mm, "end": v(-114.2, 119.25) * mm});
            skLineSegment(sketch, "E46.17.1.2", {"start": v(-109, 144.1) * mm, "end": v(-104.43, 130.17) * mm});
            skLineSegment(sketch, "E46.17.1.3", {"start": v(-123.36, 147.11) * mm, "end": v(-109, 144.1) * mm});
            skLineSegment(sketch, "E46.17.1.4", {"start": v(-133.14, 136.18) * mm, "end": v(-123.36, 147.11) * mm});
            skLineSegment(sketch, "E46.17.1.5", {"start": v(-128.56, 122.25) * mm, "end": v(-133.14, 136.18) * mm});
            skLineSegment(sketch, "E46.17.2.0", {"start": v(-114.2, 39.25) * mm, "end": v(-128.56, 42.25) * mm});
            skLineSegment(sketch, "E46.17.2.1", {"start": v(-104.43, 50.17) * mm, "end": v(-114.2, 39.25) * mm});
            skLineSegment(sketch, "E46.17.2.2", {"start": v(-109, 64.1) * mm, "end": v(-104.43, 50.17) * mm});
            skLineSegment(sketch, "E46.17.2.3", {"start": v(-123.36, 67.11) * mm, "end": v(-109, 64.1) * mm});
            skLineSegment(sketch, "E46.17.2.4", {"start": v(-133.14, 56.18) * mm, "end": v(-123.36, 67.11) * mm});
            skLineSegment(sketch, "E46.17.2.5", {"start": v(-128.56, 42.25) * mm, "end": v(-133.14, 56.18) * mm});
            skLineSegment(sketch, "E46.17.3.0", {"start": v(-114.2, -40.75) * mm, "end": v(-128.56, -37.75) * mm});
            skLineSegment(sketch, "E46.17.3.1", {"start": v(-104.43, -29.83) * mm, "end": v(-114.2, -40.75) * mm});
            skLineSegment(sketch, "E46.17.3.2", {"start": v(-109, -15.9) * mm, "end": v(-104.43, -29.83) * mm});
            skLineSegment(sketch, "E46.17.3.3", {"start": v(-123.36, -12.89) * mm, "end": v(-109, -15.9) * mm});
            skLineSegment(sketch, "E46.17.3.4", {"start": v(-133.14, -23.82) * mm, "end": v(-123.36, -12.89) * mm});
            skLineSegment(sketch, "E46.17.3.5", {"start": v(-128.56, -37.75) * mm, "end": v(-133.14, -23.82) * mm});
            skLineSegment(sketch, "E46.17.4.0", {"start": v(-114.2, -120.75) * mm, "end": v(-128.56, -117.75) * mm});
            skLineSegment(sketch, "E46.17.4.1", {"start": v(-104.43, -109.83) * mm, "end": v(-114.2, -120.75) * mm});
            skLineSegment(sketch, "E46.17.4.2", {"start": v(-109, -95.9) * mm, "end": v(-104.43, -109.83) * mm});
            skLineSegment(sketch, "E46.17.4.3", {"start": v(-123.36, -92.89) * mm, "end": v(-109, -95.9) * mm});
            skLineSegment(sketch, "E46.17.4.4", {"start": v(-133.14, -103.82) * mm, "end": v(-123.36, -92.89) * mm});
            skLineSegment(sketch, "E46.17.4.5", {"start": v(-128.56, -117.75) * mm, "end": v(-133.14, -103.82) * mm});
            skLineSegment(sketch, "E46.17.5.0", {"start": v(-114.2, -200.75) * mm, "end": v(-128.56, -197.75) * mm});
            skLineSegment(sketch, "E46.17.5.1", {"start": v(-104.43, -189.83) * mm, "end": v(-114.2, -200.75) * mm});
            skLineSegment(sketch, "E46.17.5.2", {"start": v(-109, -175.9) * mm, "end": v(-104.43, -189.83) * mm});
            skLineSegment(sketch, "E46.17.5.3", {"start": v(-123.36, -172.89) * mm, "end": v(-109, -175.9) * mm});
            skLineSegment(sketch, "E46.17.5.4", {"start": v(-133.14, -183.82) * mm, "end": v(-123.36, -172.89) * mm});
            skLineSegment(sketch, "E46.17.5.5", {"start": v(-128.56, -197.75) * mm, "end": v(-133.14, -183.82) * mm});
            skLineSegment(sketch, "E46.18.0.0", {"start": v(-34.2, 199.25) * mm, "end": v(-48.56, 202.25) * mm});
            skLineSegment(sketch, "E46.18.0.1", {"start": v(-24.43, 210.17) * mm, "end": v(-34.2, 199.25) * mm});
            skLineSegment(sketch, "E46.18.0.2", {"start": v(-29, 224.1) * mm, "end": v(-24.43, 210.17) * mm});
            skLineSegment(sketch, "E46.18.0.3", {"start": v(-43.36, 227.11) * mm, "end": v(-29, 224.1) * mm});
            skLineSegment(sketch, "E46.18.0.4", {"start": v(-53.14, 216.18) * mm, "end": v(-43.36, 227.11) * mm});
            skLineSegment(sketch, "E46.18.0.5", {"start": v(-48.56, 202.25) * mm, "end": v(-53.14, 216.18) * mm});
            skLineSegment(sketch, "E46.18.1.0", {"start": v(-34.2, 119.25) * mm, "end": v(-48.56, 122.25) * mm});
            skLineSegment(sketch, "E46.18.1.1", {"start": v(-24.43, 130.17) * mm, "end": v(-34.2, 119.25) * mm});
            skLineSegment(sketch, "E46.18.1.2", {"start": v(-29, 144.1) * mm, "end": v(-24.43, 130.17) * mm});
            skLineSegment(sketch, "E46.18.1.3", {"start": v(-43.36, 147.11) * mm, "end": v(-29, 144.1) * mm});
            skLineSegment(sketch, "E46.18.1.4", {"start": v(-53.14, 136.18) * mm, "end": v(-43.36, 147.11) * mm});
            skLineSegment(sketch, "E46.18.1.5", {"start": v(-48.56, 122.25) * mm, "end": v(-53.14, 136.18) * mm});
            skLineSegment(sketch, "E46.18.2.0", {"start": v(-34.2, 39.25) * mm, "end": v(-48.56, 42.25) * mm});
            skLineSegment(sketch, "E46.18.2.1", {"start": v(-24.43, 50.17) * mm, "end": v(-34.2, 39.25) * mm});
            skLineSegment(sketch, "E46.18.2.2", {"start": v(-29, 64.1) * mm, "end": v(-24.43, 50.17) * mm});
            skLineSegment(sketch, "E46.18.2.3", {"start": v(-43.36, 67.11) * mm, "end": v(-29, 64.1) * mm});
            skLineSegment(sketch, "E46.18.2.4", {"start": v(-53.14, 56.18) * mm, "end": v(-43.36, 67.11) * mm});
            skLineSegment(sketch, "E46.18.2.5", {"start": v(-48.56, 42.25) * mm, "end": v(-53.14, 56.18) * mm});
            skLineSegment(sketch, "E46.18.3.0", {"start": v(-34.2, -40.75) * mm, "end": v(-48.56, -37.75) * mm});
            skLineSegment(sketch, "E46.18.3.1", {"start": v(-24.43, -29.83) * mm, "end": v(-34.2, -40.75) * mm});
            skLineSegment(sketch, "E46.18.3.2", {"start": v(-29, -15.9) * mm, "end": v(-24.43, -29.83) * mm});
            skLineSegment(sketch, "E46.18.3.3", {"start": v(-43.36, -12.89) * mm, "end": v(-29, -15.9) * mm});
            skLineSegment(sketch, "E46.18.3.4", {"start": v(-53.14, -23.82) * mm, "end": v(-43.36, -12.89) * mm});
            skLineSegment(sketch, "E46.18.3.5", {"start": v(-48.56, -37.75) * mm, "end": v(-53.14, -23.82) * mm});
            skLineSegment(sketch, "E46.18.4.0", {"start": v(-34.2, -120.75) * mm, "end": v(-48.56, -117.75) * mm});
            skLineSegment(sketch, "E46.18.4.1", {"start": v(-24.43, -109.83) * mm, "end": v(-34.2, -120.75) * mm});
            skLineSegment(sketch, "E46.18.4.2", {"start": v(-29, -95.9) * mm, "end": v(-24.43, -109.83) * mm});
            skLineSegment(sketch, "E46.18.4.3", {"start": v(-43.36, -92.89) * mm, "end": v(-29, -95.9) * mm});
            skLineSegment(sketch, "E46.18.4.4", {"start": v(-53.14, -103.82) * mm, "end": v(-43.36, -92.89) * mm});
            skLineSegment(sketch, "E46.18.4.5", {"start": v(-48.56, -117.75) * mm, "end": v(-53.14, -103.82) * mm});
            skLineSegment(sketch, "E46.18.5.0", {"start": v(-34.2, -200.75) * mm, "end": v(-48.56, -197.75) * mm});
            skLineSegment(sketch, "E46.18.5.1", {"start": v(-24.43, -189.83) * mm, "end": v(-34.2, -200.75) * mm});
            skLineSegment(sketch, "E46.18.5.2", {"start": v(-29, -175.9) * mm, "end": v(-24.43, -189.83) * mm});
            skLineSegment(sketch, "E46.18.5.3", {"start": v(-43.36, -172.89) * mm, "end": v(-29, -175.9) * mm});
            skLineSegment(sketch, "E46.18.5.4", {"start": v(-53.14, -183.82) * mm, "end": v(-43.36, -172.89) * mm});
            skLineSegment(sketch, "E46.18.5.5", {"start": v(-48.56, -197.75) * mm, "end": v(-53.14, -183.82) * mm});
            skLineSegment(sketch, "E46.19.0.0", {"start": v(45.8, 199.25) * mm, "end": v(31.44, 202.25) * mm});
            skLineSegment(sketch, "E46.19.0.1", {"start": v(55.57, 210.17) * mm, "end": v(45.8, 199.25) * mm});
            skLineSegment(sketch, "E46.19.0.2", {"start": v(51, 224.1) * mm, "end": v(55.57, 210.17) * mm});
            skLineSegment(sketch, "E46.19.0.3", {"start": v(36.64, 227.11) * mm, "end": v(51, 224.1) * mm});
            skLineSegment(sketch, "E46.19.0.4", {"start": v(26.86, 216.18) * mm, "end": v(36.64, 227.11) * mm});
            skLineSegment(sketch, "E46.19.0.5", {"start": v(31.44, 202.25) * mm, "end": v(26.86, 216.18) * mm});
            skLineSegment(sketch, "E46.19.1.0", {"start": v(45.8, 119.25) * mm, "end": v(31.44, 122.25) * mm});
            skLineSegment(sketch, "E46.19.1.1", {"start": v(55.57, 130.17) * mm, "end": v(45.8, 119.25) * mm});
            skLineSegment(sketch, "E46.19.1.2", {"start": v(51, 144.1) * mm, "end": v(55.57, 130.17) * mm});
            skLineSegment(sketch, "E46.19.1.3", {"start": v(36.64, 147.11) * mm, "end": v(51, 144.1) * mm});
            skLineSegment(sketch, "E46.19.1.4", {"start": v(26.86, 136.18) * mm, "end": v(36.64, 147.11) * mm});
            skLineSegment(sketch, "E46.19.1.5", {"start": v(31.44, 122.25) * mm, "end": v(26.86, 136.18) * mm});
            skLineSegment(sketch, "E46.19.2.0", {"start": v(45.8, 39.25) * mm, "end": v(31.44, 42.25) * mm});
            skLineSegment(sketch, "E46.19.2.1", {"start": v(55.57, 50.17) * mm, "end": v(45.8, 39.25) * mm});
            skLineSegment(sketch, "E46.19.2.2", {"start": v(51, 64.1) * mm, "end": v(55.57, 50.17) * mm});
            skLineSegment(sketch, "E46.19.2.3", {"start": v(36.64, 67.11) * mm, "end": v(51, 64.1) * mm});
            skLineSegment(sketch, "E46.19.2.4", {"start": v(26.86, 56.18) * mm, "end": v(36.64, 67.11) * mm});
            skLineSegment(sketch, "E46.19.2.5", {"start": v(31.44, 42.25) * mm, "end": v(26.86, 56.18) * mm});
            skLineSegment(sketch, "E46.19.3.0", {"start": v(45.8, -40.75) * mm, "end": v(31.44, -37.75) * mm});
            skLineSegment(sketch, "E46.19.3.1", {"start": v(55.57, -29.83) * mm, "end": v(45.8, -40.75) * mm});
            skLineSegment(sketch, "E46.19.3.2", {"start": v(51, -15.9) * mm, "end": v(55.57, -29.83) * mm});
            skLineSegment(sketch, "E46.19.3.3", {"start": v(36.64, -12.89) * mm, "end": v(51, -15.9) * mm});
            skLineSegment(sketch, "E46.19.3.4", {"start": v(26.86, -23.82) * mm, "end": v(36.64, -12.89) * mm});
            skLineSegment(sketch, "E46.19.3.5", {"start": v(31.44, -37.75) * mm, "end": v(26.86, -23.82) * mm});
            skLineSegment(sketch, "E46.19.4.0", {"start": v(45.8, -120.75) * mm, "end": v(31.44, -117.75) * mm});
            skLineSegment(sketch, "E46.19.4.1", {"start": v(55.57, -109.83) * mm, "end": v(45.8, -120.75) * mm});
            skLineSegment(sketch, "E46.19.4.2", {"start": v(51, -95.9) * mm, "end": v(55.57, -109.83) * mm});
            skLineSegment(sketch, "E46.19.4.3", {"start": v(36.64, -92.89) * mm, "end": v(51, -95.9) * mm});
            skLineSegment(sketch, "E46.19.4.4", {"start": v(26.86, -103.82) * mm, "end": v(36.64, -92.89) * mm});
            skLineSegment(sketch, "E46.19.4.5", {"start": v(31.44, -117.75) * mm, "end": v(26.86, -103.82) * mm});
            skLineSegment(sketch, "E46.19.5.0", {"start": v(45.8, -200.75) * mm, "end": v(31.44, -197.75) * mm});
            skLineSegment(sketch, "E46.19.5.1", {"start": v(55.57, -189.83) * mm, "end": v(45.8, -200.75) * mm});
            skLineSegment(sketch, "E46.19.5.2", {"start": v(51, -175.9) * mm, "end": v(55.57, -189.83) * mm});
            skLineSegment(sketch, "E46.19.5.3", {"start": v(36.64, -172.89) * mm, "end": v(51, -175.9) * mm});
            skLineSegment(sketch, "E46.19.5.4", {"start": v(26.86, -183.82) * mm, "end": v(36.64, -172.89) * mm});
            skLineSegment(sketch, "E46.19.5.5", {"start": v(31.44, -197.75) * mm, "end": v(26.86, -183.82) * mm});
            skLineSegment(sketch, "E46.20.0.0", {"start": v(125.8, 199.25) * mm, "end": v(111.44, 202.25) * mm});
            skLineSegment(sketch, "E46.20.0.1", {"start": v(135.57, 210.17) * mm, "end": v(125.8, 199.25) * mm});
            skLineSegment(sketch, "E46.20.0.2", {"start": v(131, 224.1) * mm, "end": v(135.57, 210.17) * mm});
            skLineSegment(sketch, "E46.20.0.3", {"start": v(116.64, 227.11) * mm, "end": v(131, 224.1) * mm});
            skLineSegment(sketch, "E46.20.0.4", {"start": v(106.86, 216.18) * mm, "end": v(116.64, 227.11) * mm});
            skLineSegment(sketch, "E46.20.0.5", {"start": v(111.44, 202.25) * mm, "end": v(106.86, 216.18) * mm});
            skLineSegment(sketch, "E46.20.1.0", {"start": v(125.8, 119.25) * mm, "end": v(111.44, 122.25) * mm});
            skLineSegment(sketch, "E46.20.1.1", {"start": v(135.57, 130.17) * mm, "end": v(125.8, 119.25) * mm});
            skLineSegment(sketch, "E46.20.1.2", {"start": v(131, 144.1) * mm, "end": v(135.57, 130.17) * mm});
            skLineSegment(sketch, "E46.20.1.3", {"start": v(116.64, 147.11) * mm, "end": v(131, 144.1) * mm});
            skLineSegment(sketch, "E46.20.1.4", {"start": v(106.86, 136.18) * mm, "end": v(116.64, 147.11) * mm});
            skLineSegment(sketch, "E46.20.1.5", {"start": v(111.44, 122.25) * mm, "end": v(106.86, 136.18) * mm});
            skLineSegment(sketch, "E46.20.2.0", {"start": v(125.8, 39.25) * mm, "end": v(111.44, 42.25) * mm});
            skLineSegment(sketch, "E46.20.2.1", {"start": v(135.57, 50.17) * mm, "end": v(125.8, 39.25) * mm});
            skLineSegment(sketch, "E46.20.2.2", {"start": v(131, 64.1) * mm, "end": v(135.57, 50.17) * mm});
            skLineSegment(sketch, "E46.20.2.3", {"start": v(116.64, 67.11) * mm, "end": v(131, 64.1) * mm});
            skLineSegment(sketch, "E46.20.2.4", {"start": v(106.86, 56.18) * mm, "end": v(116.64, 67.11) * mm});
            skLineSegment(sketch, "E46.20.2.5", {"start": v(111.44, 42.25) * mm, "end": v(106.86, 56.18) * mm});
            skLineSegment(sketch, "E46.20.3.0", {"start": v(125.8, -40.75) * mm, "end": v(111.44, -37.75) * mm});
            skLineSegment(sketch, "E46.20.3.1", {"start": v(135.57, -29.83) * mm, "end": v(125.8, -40.75) * mm});
            skLineSegment(sketch, "E46.20.3.2", {"start": v(131, -15.9) * mm, "end": v(135.57, -29.83) * mm});
            skLineSegment(sketch, "E46.20.3.3", {"start": v(116.64, -12.89) * mm, "end": v(131, -15.9) * mm});
            skLineSegment(sketch, "E46.20.3.4", {"start": v(106.86, -23.82) * mm, "end": v(116.64, -12.89) * mm});
            skLineSegment(sketch, "E46.20.3.5", {"start": v(111.44, -37.75) * mm, "end": v(106.86, -23.82) * mm});
            skLineSegment(sketch, "E46.20.4.0", {"start": v(125.8, -120.75) * mm, "end": v(111.44, -117.75) * mm});
            skLineSegment(sketch, "E46.20.4.1", {"start": v(135.57, -109.83) * mm, "end": v(125.8, -120.75) * mm});
            skLineSegment(sketch, "E46.20.4.2", {"start": v(131, -95.9) * mm, "end": v(135.57, -109.83) * mm});
            skLineSegment(sketch, "E46.20.4.3", {"start": v(116.64, -92.89) * mm, "end": v(131, -95.9) * mm});
            skLineSegment(sketch, "E46.20.4.4", {"start": v(106.86, -103.82) * mm, "end": v(116.64, -92.89) * mm});
            skLineSegment(sketch, "E46.20.4.5", {"start": v(111.44, -117.75) * mm, "end": v(106.86, -103.82) * mm});
            skLineSegment(sketch, "E46.20.5.0", {"start": v(125.8, -200.75) * mm, "end": v(111.44, -197.75) * mm});
            skLineSegment(sketch, "E46.20.5.1", {"start": v(135.57, -189.83) * mm, "end": v(125.8, -200.75) * mm});
            skLineSegment(sketch, "E46.20.5.2", {"start": v(131, -175.9) * mm, "end": v(135.57, -189.83) * mm});
            skLineSegment(sketch, "E46.20.5.3", {"start": v(116.64, -172.89) * mm, "end": v(131, -175.9) * mm});
            skLineSegment(sketch, "E46.20.5.4", {"start": v(106.86, -183.82) * mm, "end": v(116.64, -172.89) * mm});
            skLineSegment(sketch, "E46.20.5.5", {"start": v(111.44, -197.75) * mm, "end": v(106.86, -183.82) * mm});
            skLineSegment(sketch, "E46.21.0.0", {"start": v(205.8, 199.25) * mm, "end": v(191.44, 202.25) * mm});
            skLineSegment(sketch, "E46.21.0.1", {"start": v(215.57, 210.17) * mm, "end": v(205.8, 199.25) * mm});
            skLineSegment(sketch, "E46.21.0.2", {"start": v(211, 224.1) * mm, "end": v(215.57, 210.17) * mm});
            skLineSegment(sketch, "E46.21.0.3", {"start": v(196.64, 227.11) * mm, "end": v(211, 224.1) * mm});
            skLineSegment(sketch, "E46.21.0.4", {"start": v(186.86, 216.18) * mm, "end": v(196.64, 227.11) * mm});
            skLineSegment(sketch, "E46.21.0.5", {"start": v(191.44, 202.25) * mm, "end": v(186.86, 216.18) * mm});
            skLineSegment(sketch, "E46.21.1.0", {"start": v(205.8, 119.25) * mm, "end": v(191.44, 122.25) * mm});
            skLineSegment(sketch, "E46.21.1.1", {"start": v(215.57, 130.17) * mm, "end": v(205.8, 119.25) * mm});
            skLineSegment(sketch, "E46.21.1.2", {"start": v(211, 144.1) * mm, "end": v(215.57, 130.17) * mm});
            skLineSegment(sketch, "E46.21.1.3", {"start": v(196.64, 147.11) * mm, "end": v(211, 144.1) * mm});
            skLineSegment(sketch, "E46.21.1.4", {"start": v(186.86, 136.18) * mm, "end": v(196.64, 147.11) * mm});
            skLineSegment(sketch, "E46.21.1.5", {"start": v(191.44, 122.25) * mm, "end": v(186.86, 136.18) * mm});
            skLineSegment(sketch, "E46.21.2.0", {"start": v(205.8, 39.25) * mm, "end": v(191.44, 42.25) * mm});
            skLineSegment(sketch, "E46.21.2.1", {"start": v(215.57, 50.17) * mm, "end": v(205.8, 39.25) * mm});
            skLineSegment(sketch, "E46.21.2.2", {"start": v(211, 64.1) * mm, "end": v(215.57, 50.17) * mm});
            skLineSegment(sketch, "E46.21.2.3", {"start": v(196.64, 67.11) * mm, "end": v(211, 64.1) * mm});
            skLineSegment(sketch, "E46.21.2.4", {"start": v(186.86, 56.18) * mm, "end": v(196.64, 67.11) * mm});
            skLineSegment(sketch, "E46.21.2.5", {"start": v(191.44, 42.25) * mm, "end": v(186.86, 56.18) * mm});
            skLineSegment(sketch, "E46.21.3.0", {"start": v(205.8, -40.75) * mm, "end": v(191.44, -37.75) * mm});
            skLineSegment(sketch, "E46.21.3.1", {"start": v(215.57, -29.83) * mm, "end": v(205.8, -40.75) * mm});
            skLineSegment(sketch, "E46.21.3.2", {"start": v(211, -15.9) * mm, "end": v(215.57, -29.83) * mm});
            skLineSegment(sketch, "E46.21.3.3", {"start": v(196.64, -12.89) * mm, "end": v(211, -15.9) * mm});
            skLineSegment(sketch, "E46.21.3.4", {"start": v(186.86, -23.82) * mm, "end": v(196.64, -12.89) * mm});
            skLineSegment(sketch, "E46.21.3.5", {"start": v(191.44, -37.75) * mm, "end": v(186.86, -23.82) * mm});
            skLineSegment(sketch, "E46.21.4.0", {"start": v(205.8, -120.75) * mm, "end": v(191.44, -117.75) * mm});
            skLineSegment(sketch, "E46.21.4.1", {"start": v(215.57, -109.83) * mm, "end": v(205.8, -120.75) * mm});
            skLineSegment(sketch, "E46.21.4.2", {"start": v(211, -95.9) * mm, "end": v(215.57, -109.83) * mm});
            skLineSegment(sketch, "E46.21.4.3", {"start": v(196.64, -92.89) * mm, "end": v(211, -95.9) * mm});
            skLineSegment(sketch, "E46.21.4.4", {"start": v(186.86, -103.82) * mm, "end": v(196.64, -92.89) * mm});
            skLineSegment(sketch, "E46.21.4.5", {"start": v(191.44, -117.75) * mm, "end": v(186.86, -103.82) * mm});
            skLineSegment(sketch, "E46.21.5.0", {"start": v(205.8, -200.75) * mm, "end": v(191.44, -197.75) * mm});
            skLineSegment(sketch, "E46.21.5.1", {"start": v(215.57, -189.83) * mm, "end": v(205.8, -200.75) * mm});
            skLineSegment(sketch, "E46.21.5.2", {"start": v(211, -175.9) * mm, "end": v(215.57, -189.83) * mm});
            skLineSegment(sketch, "E46.21.5.3", {"start": v(196.64, -172.89) * mm, "end": v(211, -175.9) * mm});
            skLineSegment(sketch, "E46.21.5.4", {"start": v(186.86, -183.82) * mm, "end": v(196.64, -172.89) * mm});
            skLineSegment(sketch, "E46.21.5.5", {"start": v(191.44, -197.75) * mm, "end": v(186.86, -183.82) * mm});
            skLineSegment(sketch, "E46.22.0.0", {"start": v(285.8, 199.25) * mm, "end": v(271.44, 202.25) * mm});
            skLineSegment(sketch, "E46.22.0.1", {"start": v(295.57, 210.17) * mm, "end": v(285.8, 199.25) * mm});
            skLineSegment(sketch, "E46.22.0.2", {"start": v(291, 224.1) * mm, "end": v(295.57, 210.17) * mm});
            skLineSegment(sketch, "E46.22.0.3", {"start": v(276.64, 227.11) * mm, "end": v(291, 224.1) * mm});
            skLineSegment(sketch, "E46.22.0.4", {"start": v(266.86, 216.18) * mm, "end": v(276.64, 227.11) * mm});
            skLineSegment(sketch, "E46.22.0.5", {"start": v(271.44, 202.25) * mm, "end": v(266.86, 216.18) * mm});
            skLineSegment(sketch, "E46.22.1.0", {"start": v(285.8, 119.25) * mm, "end": v(271.44, 122.25) * mm});
            skLineSegment(sketch, "E46.22.1.1", {"start": v(295.57, 130.17) * mm, "end": v(285.8, 119.25) * mm});
            skLineSegment(sketch, "E46.22.1.2", {"start": v(291, 144.1) * mm, "end": v(295.57, 130.17) * mm});
            skLineSegment(sketch, "E46.22.1.3", {"start": v(276.64, 147.11) * mm, "end": v(291, 144.1) * mm});
            skLineSegment(sketch, "E46.22.1.4", {"start": v(266.86, 136.18) * mm, "end": v(276.64, 147.11) * mm});
            skLineSegment(sketch, "E46.22.1.5", {"start": v(271.44, 122.25) * mm, "end": v(266.86, 136.18) * mm});
            skLineSegment(sketch, "E46.22.2.0", {"start": v(285.8, 39.25) * mm, "end": v(271.44, 42.25) * mm});
            skLineSegment(sketch, "E46.22.2.1", {"start": v(295.57, 50.17) * mm, "end": v(285.8, 39.25) * mm});
            skLineSegment(sketch, "E46.22.2.2", {"start": v(291, 64.1) * mm, "end": v(295.57, 50.17) * mm});
            skLineSegment(sketch, "E46.22.2.3", {"start": v(276.64, 67.11) * mm, "end": v(291, 64.1) * mm});
            skLineSegment(sketch, "E46.22.2.4", {"start": v(266.86, 56.18) * mm, "end": v(276.64, 67.11) * mm});
            skLineSegment(sketch, "E46.22.2.5", {"start": v(271.44, 42.25) * mm, "end": v(266.86, 56.18) * mm});
            skLineSegment(sketch, "E46.22.3.0", {"start": v(285.8, -40.75) * mm, "end": v(271.44, -37.75) * mm});
            skLineSegment(sketch, "E46.22.3.1", {"start": v(295.57, -29.83) * mm, "end": v(285.8, -40.75) * mm});
            skLineSegment(sketch, "E46.22.3.2", {"start": v(291, -15.9) * mm, "end": v(295.57, -29.83) * mm});
            skLineSegment(sketch, "E46.22.3.3", {"start": v(276.64, -12.89) * mm, "end": v(291, -15.9) * mm});
            skLineSegment(sketch, "E46.22.3.4", {"start": v(266.86, -23.82) * mm, "end": v(276.64, -12.89) * mm});
            skLineSegment(sketch, "E46.22.3.5", {"start": v(271.44, -37.75) * mm, "end": v(266.86, -23.82) * mm});
            skLineSegment(sketch, "E46.22.4.0", {"start": v(285.8, -120.75) * mm, "end": v(271.44, -117.75) * mm});
            skLineSegment(sketch, "E46.22.4.1", {"start": v(295.57, -109.83) * mm, "end": v(285.8, -120.75) * mm});
            skLineSegment(sketch, "E46.22.4.2", {"start": v(291, -95.9) * mm, "end": v(295.57, -109.83) * mm});
            skLineSegment(sketch, "E46.22.4.3", {"start": v(276.64, -92.89) * mm, "end": v(291, -95.9) * mm});
            skLineSegment(sketch, "E46.22.4.4", {"start": v(266.86, -103.82) * mm, "end": v(276.64, -92.89) * mm});
            skLineSegment(sketch, "E46.22.4.5", {"start": v(271.44, -117.75) * mm, "end": v(266.86, -103.82) * mm});
            skLineSegment(sketch, "E46.22.5.0", {"start": v(285.8, -200.75) * mm, "end": v(271.44, -197.75) * mm});
            skLineSegment(sketch, "E46.22.5.1", {"start": v(295.57, -189.83) * mm, "end": v(285.8, -200.75) * mm});
            skLineSegment(sketch, "E46.22.5.2", {"start": v(291, -175.9) * mm, "end": v(295.57, -189.83) * mm});
            skLineSegment(sketch, "E46.22.5.3", {"start": v(276.64, -172.89) * mm, "end": v(291, -175.9) * mm});
            skLineSegment(sketch, "E46.22.5.4", {"start": v(266.86, -183.82) * mm, "end": v(276.64, -172.89) * mm});
            skLineSegment(sketch, "E46.22.5.5", {"start": v(271.44, -197.75) * mm, "end": v(266.86, -183.82) * mm});
            skLineSegment(sketch, "E46.23.0.0", {"start": v(365.8, 199.25) * mm, "end": v(351.44, 202.25) * mm});
            skLineSegment(sketch, "E46.23.0.1", {"start": v(375.57, 210.17) * mm, "end": v(365.8, 199.25) * mm});
            skLineSegment(sketch, "E46.23.0.2", {"start": v(371, 224.1) * mm, "end": v(375.57, 210.17) * mm});
            skLineSegment(sketch, "E46.23.0.3", {"start": v(356.64, 227.11) * mm, "end": v(371, 224.1) * mm});
            skLineSegment(sketch, "E46.23.0.4", {"start": v(346.86, 216.18) * mm, "end": v(356.64, 227.11) * mm});
            skLineSegment(sketch, "E46.23.0.5", {"start": v(351.44, 202.25) * mm, "end": v(346.86, 216.18) * mm});
            skLineSegment(sketch, "E46.23.1.0", {"start": v(365.8, 119.25) * mm, "end": v(351.44, 122.25) * mm});
            skLineSegment(sketch, "E46.23.1.1", {"start": v(375.57, 130.17) * mm, "end": v(365.8, 119.25) * mm});
            skLineSegment(sketch, "E46.23.1.2", {"start": v(371, 144.1) * mm, "end": v(375.57, 130.17) * mm});
            skLineSegment(sketch, "E46.23.1.3", {"start": v(356.64, 147.11) * mm, "end": v(371, 144.1) * mm});
            skLineSegment(sketch, "E46.23.1.4", {"start": v(346.86, 136.18) * mm, "end": v(356.64, 147.11) * mm});
            skLineSegment(sketch, "E46.23.1.5", {"start": v(351.44, 122.25) * mm, "end": v(346.86, 136.18) * mm});
            skLineSegment(sketch, "E46.23.2.0", {"start": v(365.8, 39.25) * mm, "end": v(351.44, 42.25) * mm});
            skLineSegment(sketch, "E46.23.2.1", {"start": v(375.57, 50.17) * mm, "end": v(365.8, 39.25) * mm});
            skLineSegment(sketch, "E46.23.2.2", {"start": v(371, 64.1) * mm, "end": v(375.57, 50.17) * mm});
            skLineSegment(sketch, "E46.23.2.3", {"start": v(356.64, 67.11) * mm, "end": v(371, 64.1) * mm});
            skLineSegment(sketch, "E46.23.2.4", {"start": v(346.86, 56.18) * mm, "end": v(356.64, 67.11) * mm});
            skLineSegment(sketch, "E46.23.2.5", {"start": v(351.44, 42.25) * mm, "end": v(346.86, 56.18) * mm});
            skLineSegment(sketch, "E46.23.3.0", {"start": v(365.8, -40.75) * mm, "end": v(351.44, -37.75) * mm});
            skLineSegment(sketch, "E46.23.3.1", {"start": v(375.57, -29.83) * mm, "end": v(365.8, -40.75) * mm});
            skLineSegment(sketch, "E46.23.3.2", {"start": v(371, -15.9) * mm, "end": v(375.57, -29.83) * mm});
            skLineSegment(sketch, "E46.23.3.3", {"start": v(356.64, -12.89) * mm, "end": v(371, -15.9) * mm});
            skLineSegment(sketch, "E46.23.3.4", {"start": v(346.86, -23.82) * mm, "end": v(356.64, -12.89) * mm});
            skLineSegment(sketch, "E46.23.3.5", {"start": v(351.44, -37.75) * mm, "end": v(346.86, -23.82) * mm});
            skLineSegment(sketch, "E46.23.4.0", {"start": v(365.8, -120.75) * mm, "end": v(351.44, -117.75) * mm});
            skLineSegment(sketch, "E46.23.4.1", {"start": v(375.57, -109.83) * mm, "end": v(365.8, -120.75) * mm});
            skLineSegment(sketch, "E46.23.4.2", {"start": v(371, -95.9) * mm, "end": v(375.57, -109.83) * mm});
            skLineSegment(sketch, "E46.23.4.3", {"start": v(356.64, -92.89) * mm, "end": v(371, -95.9) * mm});
            skLineSegment(sketch, "E46.23.4.4", {"start": v(346.86, -103.82) * mm, "end": v(356.64, -92.89) * mm});
            skLineSegment(sketch, "E46.23.4.5", {"start": v(351.44, -117.75) * mm, "end": v(346.86, -103.82) * mm});
            skLineSegment(sketch, "E46.23.5.0", {"start": v(365.8, -200.75) * mm, "end": v(351.44, -197.75) * mm});
            skLineSegment(sketch, "E46.23.5.1", {"start": v(375.57, -189.83) * mm, "end": v(365.8, -200.75) * mm});
            skLineSegment(sketch, "E46.23.5.2", {"start": v(371, -175.9) * mm, "end": v(375.57, -189.83) * mm});
            skLineSegment(sketch, "E46.23.5.3", {"start": v(356.64, -172.89) * mm, "end": v(371, -175.9) * mm});
            skLineSegment(sketch, "E46.23.5.4", {"start": v(346.86, -183.82) * mm, "end": v(356.64, -172.89) * mm});
            skLineSegment(sketch, "E46.23.5.5", {"start": v(351.44, -197.75) * mm, "end": v(346.86, -183.82) * mm});
            skLineSegment(sketch, "E46.24.0.0", {"start": v(445.8, 199.25) * mm, "end": v(431.44, 202.25) * mm});
            skLineSegment(sketch, "E46.24.0.1", {"start": v(455.57, 210.17) * mm, "end": v(445.8, 199.25) * mm});
            skLineSegment(sketch, "E46.24.0.2", {"start": v(451, 224.1) * mm, "end": v(455.57, 210.17) * mm});
            skLineSegment(sketch, "E46.24.0.3", {"start": v(436.64, 227.11) * mm, "end": v(451, 224.1) * mm});
            skLineSegment(sketch, "E46.24.0.4", {"start": v(426.86, 216.18) * mm, "end": v(436.64, 227.11) * mm});
            skLineSegment(sketch, "E46.24.0.5", {"start": v(431.44, 202.25) * mm, "end": v(426.86, 216.18) * mm});
            skLineSegment(sketch, "E46.24.1.0", {"start": v(445.8, 119.25) * mm, "end": v(431.44, 122.25) * mm});
            skLineSegment(sketch, "E46.24.1.1", {"start": v(455.57, 130.17) * mm, "end": v(445.8, 119.25) * mm});
            skLineSegment(sketch, "E46.24.1.2", {"start": v(451, 144.1) * mm, "end": v(455.57, 130.17) * mm});
            skLineSegment(sketch, "E46.24.1.3", {"start": v(436.64, 147.11) * mm, "end": v(451, 144.1) * mm});
            skLineSegment(sketch, "E46.24.1.4", {"start": v(426.86, 136.18) * mm, "end": v(436.64, 147.11) * mm});
            skLineSegment(sketch, "E46.24.1.5", {"start": v(431.44, 122.25) * mm, "end": v(426.86, 136.18) * mm});
            skLineSegment(sketch, "E46.24.2.0", {"start": v(445.8, 39.25) * mm, "end": v(431.44, 42.25) * mm});
            skLineSegment(sketch, "E46.24.2.1", {"start": v(455.57, 50.17) * mm, "end": v(445.8, 39.25) * mm});
            skLineSegment(sketch, "E46.24.2.2", {"start": v(451, 64.1) * mm, "end": v(455.57, 50.17) * mm});
            skLineSegment(sketch, "E46.24.2.3", {"start": v(436.64, 67.11) * mm, "end": v(451, 64.1) * mm});
            skLineSegment(sketch, "E46.24.2.4", {"start": v(426.86, 56.18) * mm, "end": v(436.64, 67.11) * mm});
            skLineSegment(sketch, "E46.24.2.5", {"start": v(431.44, 42.25) * mm, "end": v(426.86, 56.18) * mm});
            skLineSegment(sketch, "E46.24.3.0", {"start": v(445.8, -40.75) * mm, "end": v(431.44, -37.75) * mm});
            skLineSegment(sketch, "E46.24.3.1", {"start": v(455.57, -29.83) * mm, "end": v(445.8, -40.75) * mm});
            skLineSegment(sketch, "E46.24.3.2", {"start": v(451, -15.9) * mm, "end": v(455.57, -29.83) * mm});
            skLineSegment(sketch, "E46.24.3.3", {"start": v(436.64, -12.89) * mm, "end": v(451, -15.9) * mm});
            skLineSegment(sketch, "E46.24.3.4", {"start": v(426.86, -23.82) * mm, "end": v(436.64, -12.89) * mm});
            skLineSegment(sketch, "E46.24.3.5", {"start": v(431.44, -37.75) * mm, "end": v(426.86, -23.82) * mm});
            skLineSegment(sketch, "E46.24.4.0", {"start": v(445.8, -120.75) * mm, "end": v(431.44, -117.75) * mm});
            skLineSegment(sketch, "E46.24.4.1", {"start": v(455.57, -109.83) * mm, "end": v(445.8, -120.75) * mm});
            skLineSegment(sketch, "E46.24.4.2", {"start": v(451, -95.9) * mm, "end": v(455.57, -109.83) * mm});
            skLineSegment(sketch, "E46.24.4.3", {"start": v(436.64, -92.89) * mm, "end": v(451, -95.9) * mm});
            skLineSegment(sketch, "E46.24.4.4", {"start": v(426.86, -103.82) * mm, "end": v(436.64, -92.89) * mm});
            skLineSegment(sketch, "E46.24.4.5", {"start": v(431.44, -117.75) * mm, "end": v(426.86, -103.82) * mm});
            skLineSegment(sketch, "E46.24.5.0", {"start": v(445.8, -200.75) * mm, "end": v(431.44, -197.75) * mm});
            skLineSegment(sketch, "E46.24.5.1", {"start": v(455.57, -189.83) * mm, "end": v(445.8, -200.75) * mm});
            skLineSegment(sketch, "E46.24.5.2", {"start": v(451, -175.9) * mm, "end": v(455.57, -189.83) * mm});
            skLineSegment(sketch, "E46.24.5.3", {"start": v(436.64, -172.89) * mm, "end": v(451, -175.9) * mm});
            skLineSegment(sketch, "E46.24.5.4", {"start": v(426.86, -183.82) * mm, "end": v(436.64, -172.89) * mm});
            skLineSegment(sketch, "E46.24.5.5", {"start": v(431.44, -197.75) * mm, "end": v(426.86, -183.82) * mm});
            skLineSegment(sketch, "E46.25.0.0", {"start": v(525.8, 199.25) * mm, "end": v(511.44, 202.25) * mm});
            skLineSegment(sketch, "E46.25.0.1", {"start": v(535.57, 210.17) * mm, "end": v(525.8, 199.25) * mm});
            skLineSegment(sketch, "E46.25.0.2", {"start": v(531, 224.1) * mm, "end": v(535.57, 210.17) * mm});
            skLineSegment(sketch, "E46.25.0.3", {"start": v(516.64, 227.11) * mm, "end": v(531, 224.1) * mm});
            skLineSegment(sketch, "E46.25.0.4", {"start": v(506.86, 216.18) * mm, "end": v(516.64, 227.11) * mm});
            skLineSegment(sketch, "E46.25.0.5", {"start": v(511.44, 202.25) * mm, "end": v(506.86, 216.18) * mm});
            skLineSegment(sketch, "E46.25.1.0", {"start": v(525.8, 119.25) * mm, "end": v(511.44, 122.25) * mm});
            skLineSegment(sketch, "E46.25.1.1", {"start": v(535.57, 130.17) * mm, "end": v(525.8, 119.25) * mm});
            skLineSegment(sketch, "E46.25.1.2", {"start": v(531, 144.1) * mm, "end": v(535.57, 130.17) * mm});
            skLineSegment(sketch, "E46.25.1.3", {"start": v(516.64, 147.11) * mm, "end": v(531, 144.1) * mm});
            skLineSegment(sketch, "E46.25.1.4", {"start": v(506.86, 136.18) * mm, "end": v(516.64, 147.11) * mm});
            skLineSegment(sketch, "E46.25.1.5", {"start": v(511.44, 122.25) * mm, "end": v(506.86, 136.18) * mm});
            skLineSegment(sketch, "E46.25.2.0", {"start": v(525.8, 39.25) * mm, "end": v(511.44, 42.25) * mm});
            skLineSegment(sketch, "E46.25.2.1", {"start": v(535.57, 50.17) * mm, "end": v(525.8, 39.25) * mm});
            skLineSegment(sketch, "E46.25.2.2", {"start": v(531, 64.1) * mm, "end": v(535.57, 50.17) * mm});
            skLineSegment(sketch, "E46.25.2.3", {"start": v(516.64, 67.11) * mm, "end": v(531, 64.1) * mm});
            skLineSegment(sketch, "E46.25.2.4", {"start": v(506.86, 56.18) * mm, "end": v(516.64, 67.11) * mm});
            skLineSegment(sketch, "E46.25.2.5", {"start": v(511.44, 42.25) * mm, "end": v(506.86, 56.18) * mm});
            skLineSegment(sketch, "E46.25.3.0", {"start": v(525.8, -40.75) * mm, "end": v(511.44, -37.75) * mm});
            skLineSegment(sketch, "E46.25.3.1", {"start": v(535.57, -29.83) * mm, "end": v(525.8, -40.75) * mm});
            skLineSegment(sketch, "E46.25.3.2", {"start": v(531, -15.9) * mm, "end": v(535.57, -29.83) * mm});
            skLineSegment(sketch, "E46.25.3.3", {"start": v(516.64, -12.89) * mm, "end": v(531, -15.9) * mm});
            skLineSegment(sketch, "E46.25.3.4", {"start": v(506.86, -23.82) * mm, "end": v(516.64, -12.89) * mm});
            skLineSegment(sketch, "E46.25.3.5", {"start": v(511.44, -37.75) * mm, "end": v(506.86, -23.82) * mm});
            skLineSegment(sketch, "E46.25.4.0", {"start": v(525.8, -120.75) * mm, "end": v(511.44, -117.75) * mm});
            skLineSegment(sketch, "E46.25.4.1", {"start": v(535.57, -109.83) * mm, "end": v(525.8, -120.75) * mm});
            skLineSegment(sketch, "E46.25.4.2", {"start": v(531, -95.9) * mm, "end": v(535.57, -109.83) * mm});
            skLineSegment(sketch, "E46.25.4.3", {"start": v(516.64, -92.89) * mm, "end": v(531, -95.9) * mm});
            skLineSegment(sketch, "E46.25.4.4", {"start": v(506.86, -103.82) * mm, "end": v(516.64, -92.89) * mm});
            skLineSegment(sketch, "E46.25.4.5", {"start": v(511.44, -117.75) * mm, "end": v(506.86, -103.82) * mm});
            skLineSegment(sketch, "E46.25.5.0", {"start": v(525.8, -200.75) * mm, "end": v(511.44, -197.75) * mm});
            skLineSegment(sketch, "E46.25.5.1", {"start": v(535.57, -189.83) * mm, "end": v(525.8, -200.75) * mm});
            skLineSegment(sketch, "E46.25.5.2", {"start": v(531, -175.9) * mm, "end": v(535.57, -189.83) * mm});
            skLineSegment(sketch, "E46.25.5.3", {"start": v(516.64, -172.89) * mm, "end": v(531, -175.9) * mm});
            skLineSegment(sketch, "E46.25.5.4", {"start": v(506.86, -183.82) * mm, "end": v(516.64, -172.89) * mm});
            skLineSegment(sketch, "E46.25.5.5", {"start": v(511.44, -197.75) * mm, "end": v(506.86, -183.82) * mm});
            skLineSegment(sketch, "E46.26.0.0", {"start": v(605.8, 199.25) * mm, "end": v(591.44, 202.25) * mm});
            skLineSegment(sketch, "E46.26.0.1", {"start": v(615.57, 210.17) * mm, "end": v(605.8, 199.25) * mm});
            skLineSegment(sketch, "E46.26.0.2", {"start": v(611, 224.1) * mm, "end": v(615.57, 210.17) * mm});
            skLineSegment(sketch, "E46.26.0.3", {"start": v(596.64, 227.11) * mm, "end": v(611, 224.1) * mm});
            skLineSegment(sketch, "E46.26.0.4", {"start": v(586.86, 216.18) * mm, "end": v(596.64, 227.11) * mm});
            skLineSegment(sketch, "E46.26.0.5", {"start": v(591.44, 202.25) * mm, "end": v(586.86, 216.18) * mm});
            skLineSegment(sketch, "E46.26.1.0", {"start": v(605.8, 119.25) * mm, "end": v(591.44, 122.25) * mm});
            skLineSegment(sketch, "E46.26.1.1", {"start": v(615.57, 130.17) * mm, "end": v(605.8, 119.25) * mm});
            skLineSegment(sketch, "E46.26.1.2", {"start": v(611, 144.1) * mm, "end": v(615.57, 130.17) * mm});
            skLineSegment(sketch, "E46.26.1.3", {"start": v(596.64, 147.11) * mm, "end": v(611, 144.1) * mm});
            skLineSegment(sketch, "E46.26.1.4", {"start": v(586.86, 136.18) * mm, "end": v(596.64, 147.11) * mm});
            skLineSegment(sketch, "E46.26.1.5", {"start": v(591.44, 122.25) * mm, "end": v(586.86, 136.18) * mm});
            skLineSegment(sketch, "E46.26.2.0", {"start": v(605.8, 39.25) * mm, "end": v(591.44, 42.25) * mm});
            skLineSegment(sketch, "E46.26.2.1", {"start": v(615.57, 50.17) * mm, "end": v(605.8, 39.25) * mm});
            skLineSegment(sketch, "E46.26.2.2", {"start": v(611, 64.1) * mm, "end": v(615.57, 50.17) * mm});
            skLineSegment(sketch, "E46.26.2.3", {"start": v(596.64, 67.11) * mm, "end": v(611, 64.1) * mm});
            skLineSegment(sketch, "E46.26.2.4", {"start": v(586.86, 56.18) * mm, "end": v(596.64, 67.11) * mm});
            skLineSegment(sketch, "E46.26.2.5", {"start": v(591.44, 42.25) * mm, "end": v(586.86, 56.18) * mm});
            skLineSegment(sketch, "E46.26.3.0", {"start": v(605.8, -40.75) * mm, "end": v(591.44, -37.75) * mm});
            skLineSegment(sketch, "E46.26.3.1", {"start": v(615.57, -29.83) * mm, "end": v(605.8, -40.75) * mm});
            skLineSegment(sketch, "E46.26.3.2", {"start": v(611, -15.9) * mm, "end": v(615.57, -29.83) * mm});
            skLineSegment(sketch, "E46.26.3.3", {"start": v(596.64, -12.89) * mm, "end": v(611, -15.9) * mm});
            skLineSegment(sketch, "E46.26.3.4", {"start": v(586.86, -23.82) * mm, "end": v(596.64, -12.89) * mm});
            skLineSegment(sketch, "E46.26.3.5", {"start": v(591.44, -37.75) * mm, "end": v(586.86, -23.82) * mm});
            skLineSegment(sketch, "E46.26.4.0", {"start": v(605.8, -120.75) * mm, "end": v(591.44, -117.75) * mm});
            skLineSegment(sketch, "E46.26.4.1", {"start": v(615.57, -109.83) * mm, "end": v(605.8, -120.75) * mm});
            skLineSegment(sketch, "E46.26.4.2", {"start": v(611, -95.9) * mm, "end": v(615.57, -109.83) * mm});
            skLineSegment(sketch, "E46.26.4.3", {"start": v(596.64, -92.89) * mm, "end": v(611, -95.9) * mm});
            skLineSegment(sketch, "E46.26.4.4", {"start": v(586.86, -103.82) * mm, "end": v(596.64, -92.89) * mm});
            skLineSegment(sketch, "E46.26.4.5", {"start": v(591.44, -117.75) * mm, "end": v(586.86, -103.82) * mm});
            skLineSegment(sketch, "E46.26.5.0", {"start": v(605.8, -200.75) * mm, "end": v(591.44, -197.75) * mm});
            skLineSegment(sketch, "E46.26.5.1", {"start": v(615.57, -189.83) * mm, "end": v(605.8, -200.75) * mm});
            skLineSegment(sketch, "E46.26.5.2", {"start": v(611, -175.9) * mm, "end": v(615.57, -189.83) * mm});
            skLineSegment(sketch, "E46.26.5.3", {"start": v(596.64, -172.89) * mm, "end": v(611, -175.9) * mm});
            skLineSegment(sketch, "E46.26.5.4", {"start": v(586.86, -183.82) * mm, "end": v(596.64, -172.89) * mm});
            skLineSegment(sketch, "E46.26.5.5", {"start": v(591.44, -197.75) * mm, "end": v(586.86, -183.82) * mm});
            skLineSegment(sketch, "E46.27.0.0", {"start": v(685.8, 199.25) * mm, "end": v(671.44, 202.25) * mm});
            skLineSegment(sketch, "E46.27.0.1", {"start": v(695.57, 210.17) * mm, "end": v(685.8, 199.25) * mm});
            skLineSegment(sketch, "E46.27.0.2", {"start": v(691, 224.1) * mm, "end": v(695.57, 210.17) * mm});
            skLineSegment(sketch, "E46.27.0.3", {"start": v(676.64, 227.11) * mm, "end": v(691, 224.1) * mm});
            skLineSegment(sketch, "E46.27.0.4", {"start": v(666.86, 216.18) * mm, "end": v(676.64, 227.11) * mm});
            skLineSegment(sketch, "E46.27.0.5", {"start": v(671.44, 202.25) * mm, "end": v(666.86, 216.18) * mm});
            skLineSegment(sketch, "E46.27.1.0", {"start": v(685.8, 119.25) * mm, "end": v(671.44, 122.25) * mm});
            skLineSegment(sketch, "E46.27.1.1", {"start": v(695.57, 130.17) * mm, "end": v(685.8, 119.25) * mm});
            skLineSegment(sketch, "E46.27.1.2", {"start": v(691, 144.1) * mm, "end": v(695.57, 130.17) * mm});
            skLineSegment(sketch, "E46.27.1.3", {"start": v(676.64, 147.11) * mm, "end": v(691, 144.1) * mm});
            skLineSegment(sketch, "E46.27.1.4", {"start": v(666.86, 136.18) * mm, "end": v(676.64, 147.11) * mm});
            skLineSegment(sketch, "E46.27.1.5", {"start": v(671.44, 122.25) * mm, "end": v(666.86, 136.18) * mm});
            skLineSegment(sketch, "E46.27.2.0", {"start": v(685.8, 39.25) * mm, "end": v(671.44, 42.25) * mm});
            skLineSegment(sketch, "E46.27.2.1", {"start": v(695.57, 50.17) * mm, "end": v(685.8, 39.25) * mm});
            skLineSegment(sketch, "E46.27.2.2", {"start": v(691, 64.1) * mm, "end": v(695.57, 50.17) * mm});
            skLineSegment(sketch, "E46.27.2.3", {"start": v(676.64, 67.11) * mm, "end": v(691, 64.1) * mm});
            skLineSegment(sketch, "E46.27.2.4", {"start": v(666.86, 56.18) * mm, "end": v(676.64, 67.11) * mm});
            skLineSegment(sketch, "E46.27.2.5", {"start": v(671.44, 42.25) * mm, "end": v(666.86, 56.18) * mm});
            skLineSegment(sketch, "E46.27.3.0", {"start": v(685.8, -40.75) * mm, "end": v(671.44, -37.75) * mm});
            skLineSegment(sketch, "E46.27.3.1", {"start": v(695.57, -29.83) * mm, "end": v(685.8, -40.75) * mm});
            skLineSegment(sketch, "E46.27.3.2", {"start": v(691, -15.9) * mm, "end": v(695.57, -29.83) * mm});
            skLineSegment(sketch, "E46.27.3.3", {"start": v(676.64, -12.89) * mm, "end": v(691, -15.9) * mm});
            skLineSegment(sketch, "E46.27.3.4", {"start": v(666.86, -23.82) * mm, "end": v(676.64, -12.89) * mm});
            skLineSegment(sketch, "E46.27.3.5", {"start": v(671.44, -37.75) * mm, "end": v(666.86, -23.82) * mm});
            skLineSegment(sketch, "E46.27.4.0", {"start": v(685.8, -120.75) * mm, "end": v(671.44, -117.75) * mm});
            skLineSegment(sketch, "E46.27.4.1", {"start": v(695.57, -109.83) * mm, "end": v(685.8, -120.75) * mm});
            skLineSegment(sketch, "E46.27.4.2", {"start": v(691, -95.9) * mm, "end": v(695.57, -109.83) * mm});
            skLineSegment(sketch, "E46.27.4.3", {"start": v(676.64, -92.89) * mm, "end": v(691, -95.9) * mm});
            skLineSegment(sketch, "E46.27.4.4", {"start": v(666.86, -103.82) * mm, "end": v(676.64, -92.89) * mm});
            skLineSegment(sketch, "E46.27.4.5", {"start": v(671.44, -117.75) * mm, "end": v(666.86, -103.82) * mm});
            skLineSegment(sketch, "E46.27.5.0", {"start": v(685.8, -200.75) * mm, "end": v(671.44, -197.75) * mm});
            skLineSegment(sketch, "E46.27.5.1", {"start": v(695.57, -189.83) * mm, "end": v(685.8, -200.75) * mm});
            skLineSegment(sketch, "E46.27.5.2", {"start": v(691, -175.9) * mm, "end": v(695.57, -189.83) * mm});
            skLineSegment(sketch, "E46.27.5.3", {"start": v(676.64, -172.89) * mm, "end": v(691, -175.9) * mm});
            skLineSegment(sketch, "E46.27.5.4", {"start": v(666.86, -183.82) * mm, "end": v(676.64, -172.89) * mm});
            skLineSegment(sketch, "E46.27.5.5", {"start": v(671.44, -197.75) * mm, "end": v(666.86, -183.82) * mm});
            skLineSegment(sketch, "E46.28.0.0", {"start": v(765.8, 199.25) * mm, "end": v(751.44, 202.25) * mm});
            skLineSegment(sketch, "E46.28.0.1", {"start": v(775.57, 210.17) * mm, "end": v(765.8, 199.25) * mm});
            skLineSegment(sketch, "E46.28.0.2", {"start": v(771, 224.1) * mm, "end": v(775.57, 210.17) * mm});
            skLineSegment(sketch, "E46.28.0.3", {"start": v(756.64, 227.11) * mm, "end": v(771, 224.1) * mm});
            skLineSegment(sketch, "E46.28.0.4", {"start": v(746.86, 216.18) * mm, "end": v(756.64, 227.11) * mm});
            skLineSegment(sketch, "E46.28.0.5", {"start": v(751.44, 202.25) * mm, "end": v(746.86, 216.18) * mm});
            skLineSegment(sketch, "E46.28.1.0", {"start": v(765.8, 119.25) * mm, "end": v(751.44, 122.25) * mm});
            skLineSegment(sketch, "E46.28.1.1", {"start": v(775.57, 130.17) * mm, "end": v(765.8, 119.25) * mm});
            skLineSegment(sketch, "E46.28.1.2", {"start": v(771, 144.1) * mm, "end": v(775.57, 130.17) * mm});
            skLineSegment(sketch, "E46.28.1.3", {"start": v(756.64, 147.11) * mm, "end": v(771, 144.1) * mm});
            skLineSegment(sketch, "E46.28.1.4", {"start": v(746.86, 136.18) * mm, "end": v(756.64, 147.11) * mm});
            skLineSegment(sketch, "E46.28.1.5", {"start": v(751.44, 122.25) * mm, "end": v(746.86, 136.18) * mm});
            skLineSegment(sketch, "E46.28.2.0", {"start": v(765.8, 39.25) * mm, "end": v(751.44, 42.25) * mm});
            skLineSegment(sketch, "E46.28.2.1", {"start": v(775.57, 50.17) * mm, "end": v(765.8, 39.25) * mm});
            skLineSegment(sketch, "E46.28.2.2", {"start": v(771, 64.1) * mm, "end": v(775.57, 50.17) * mm});
            skLineSegment(sketch, "E46.28.2.3", {"start": v(756.64, 67.11) * mm, "end": v(771, 64.1) * mm});
            skLineSegment(sketch, "E46.28.2.4", {"start": v(746.86, 56.18) * mm, "end": v(756.64, 67.11) * mm});
            skLineSegment(sketch, "E46.28.2.5", {"start": v(751.44, 42.25) * mm, "end": v(746.86, 56.18) * mm});
            skLineSegment(sketch, "E46.28.3.0", {"start": v(765.8, -40.75) * mm, "end": v(751.44, -37.75) * mm});
            skLineSegment(sketch, "E46.28.3.1", {"start": v(775.57, -29.83) * mm, "end": v(765.8, -40.75) * mm});
            skLineSegment(sketch, "E46.28.3.2", {"start": v(771, -15.9) * mm, "end": v(775.57, -29.83) * mm});
            skLineSegment(sketch, "E46.28.3.3", {"start": v(756.64, -12.89) * mm, "end": v(771, -15.9) * mm});
            skLineSegment(sketch, "E46.28.3.4", {"start": v(746.86, -23.82) * mm, "end": v(756.64, -12.89) * mm});
            skLineSegment(sketch, "E46.28.3.5", {"start": v(751.44, -37.75) * mm, "end": v(746.86, -23.82) * mm});
            skLineSegment(sketch, "E46.28.4.0", {"start": v(765.8, -120.75) * mm, "end": v(751.44, -117.75) * mm});
            skLineSegment(sketch, "E46.28.4.1", {"start": v(775.57, -109.83) * mm, "end": v(765.8, -120.75) * mm});
            skLineSegment(sketch, "E46.28.4.2", {"start": v(771, -95.9) * mm, "end": v(775.57, -109.83) * mm});
            skLineSegment(sketch, "E46.28.4.3", {"start": v(756.64, -92.89) * mm, "end": v(771, -95.9) * mm});
            skLineSegment(sketch, "E46.28.4.4", {"start": v(746.86, -103.82) * mm, "end": v(756.64, -92.89) * mm});
            skLineSegment(sketch, "E46.28.4.5", {"start": v(751.44, -117.75) * mm, "end": v(746.86, -103.82) * mm});
            skLineSegment(sketch, "E46.28.5.0", {"start": v(765.8, -200.75) * mm, "end": v(751.44, -197.75) * mm});
            skLineSegment(sketch, "E46.28.5.1", {"start": v(775.57, -189.83) * mm, "end": v(765.8, -200.75) * mm});
            skLineSegment(sketch, "E46.28.5.2", {"start": v(771, -175.9) * mm, "end": v(775.57, -189.83) * mm});
            skLineSegment(sketch, "E46.28.5.3", {"start": v(756.64, -172.89) * mm, "end": v(771, -175.9) * mm});
            skLineSegment(sketch, "E46.28.5.4", {"start": v(746.86, -183.82) * mm, "end": v(756.64, -172.89) * mm});
            skLineSegment(sketch, "E46.28.5.5", {"start": v(751.44, -197.75) * mm, "end": v(746.86, -183.82) * mm});
            skLineSegment(sketch, "E46.29.0.0", {"start": v(845.8, 199.25) * mm, "end": v(831.44, 202.25) * mm});
            skLineSegment(sketch, "E46.29.0.1", {"start": v(855.57, 210.17) * mm, "end": v(845.8, 199.25) * mm});
            skLineSegment(sketch, "E46.29.0.2", {"start": v(851, 224.1) * mm, "end": v(855.57, 210.17) * mm});
            skLineSegment(sketch, "E46.29.0.3", {"start": v(836.64, 227.11) * mm, "end": v(851, 224.1) * mm});
            skLineSegment(sketch, "E46.29.0.4", {"start": v(826.86, 216.18) * mm, "end": v(836.64, 227.11) * mm});
            skLineSegment(sketch, "E46.29.0.5", {"start": v(831.44, 202.25) * mm, "end": v(826.86, 216.18) * mm});
            skLineSegment(sketch, "E46.29.1.0", {"start": v(845.8, 119.25) * mm, "end": v(831.44, 122.25) * mm});
            skLineSegment(sketch, "E46.29.1.1", {"start": v(855.57, 130.17) * mm, "end": v(845.8, 119.25) * mm});
            skLineSegment(sketch, "E46.29.1.2", {"start": v(851, 144.1) * mm, "end": v(855.57, 130.17) * mm});
            skLineSegment(sketch, "E46.29.1.3", {"start": v(836.64, 147.11) * mm, "end": v(851, 144.1) * mm});
            skLineSegment(sketch, "E46.29.1.4", {"start": v(826.86, 136.18) * mm, "end": v(836.64, 147.11) * mm});
            skLineSegment(sketch, "E46.29.1.5", {"start": v(831.44, 122.25) * mm, "end": v(826.86, 136.18) * mm});
            skLineSegment(sketch, "E46.29.2.0", {"start": v(845.8, 39.25) * mm, "end": v(831.44, 42.25) * mm});
            skLineSegment(sketch, "E46.29.2.1", {"start": v(855.57, 50.17) * mm, "end": v(845.8, 39.25) * mm});
            skLineSegment(sketch, "E46.29.2.2", {"start": v(851, 64.1) * mm, "end": v(855.57, 50.17) * mm});
            skLineSegment(sketch, "E46.29.2.3", {"start": v(836.64, 67.11) * mm, "end": v(851, 64.1) * mm});
            skLineSegment(sketch, "E46.29.2.4", {"start": v(826.86, 56.18) * mm, "end": v(836.64, 67.11) * mm});
            skLineSegment(sketch, "E46.29.2.5", {"start": v(831.44, 42.25) * mm, "end": v(826.86, 56.18) * mm});
            skLineSegment(sketch, "E46.29.3.0", {"start": v(845.8, -40.75) * mm, "end": v(831.44, -37.75) * mm});
            skLineSegment(sketch, "E46.29.3.1", {"start": v(855.57, -29.83) * mm, "end": v(845.8, -40.75) * mm});
            skLineSegment(sketch, "E46.29.3.2", {"start": v(851, -15.9) * mm, "end": v(855.57, -29.83) * mm});
            skLineSegment(sketch, "E46.29.3.3", {"start": v(836.64, -12.89) * mm, "end": v(851, -15.9) * mm});
            skLineSegment(sketch, "E46.29.3.4", {"start": v(826.86, -23.82) * mm, "end": v(836.64, -12.89) * mm});
            skLineSegment(sketch, "E46.29.3.5", {"start": v(831.44, -37.75) * mm, "end": v(826.86, -23.82) * mm});
            skLineSegment(sketch, "E46.29.4.0", {"start": v(845.8, -120.75) * mm, "end": v(831.44, -117.75) * mm});
            skLineSegment(sketch, "E46.29.4.1", {"start": v(855.57, -109.83) * mm, "end": v(845.8, -120.75) * mm});
            skLineSegment(sketch, "E46.29.4.2", {"start": v(851, -95.9) * mm, "end": v(855.57, -109.83) * mm});
            skLineSegment(sketch, "E46.29.4.3", {"start": v(836.64, -92.89) * mm, "end": v(851, -95.9) * mm});
            skLineSegment(sketch, "E46.29.4.4", {"start": v(826.86, -103.82) * mm, "end": v(836.64, -92.89) * mm});
            skLineSegment(sketch, "E46.29.4.5", {"start": v(831.44, -117.75) * mm, "end": v(826.86, -103.82) * mm});
            skLineSegment(sketch, "E46.29.5.0", {"start": v(845.8, -200.75) * mm, "end": v(831.44, -197.75) * mm});
            skLineSegment(sketch, "E46.29.5.1", {"start": v(855.57, -189.83) * mm, "end": v(845.8, -200.75) * mm});
            skLineSegment(sketch, "E46.29.5.2", {"start": v(851, -175.9) * mm, "end": v(855.57, -189.83) * mm});
            skLineSegment(sketch, "E46.29.5.3", {"start": v(836.64, -172.89) * mm, "end": v(851, -175.9) * mm});
            skLineSegment(sketch, "E46.29.5.4", {"start": v(826.86, -183.82) * mm, "end": v(836.64, -172.89) * mm});
            skLineSegment(sketch, "E46.29.5.5", {"start": v(831.44, -197.75) * mm, "end": v(826.86, -183.82) * mm});
            skLineSegment(sketch, "E46.30.0.0", {"start": v(925.8, 199.25) * mm, "end": v(911.44, 202.25) * mm});
            skLineSegment(sketch, "E46.30.0.1", {"start": v(935.57, 210.17) * mm, "end": v(925.8, 199.25) * mm});
            skLineSegment(sketch, "E46.30.0.2", {"start": v(931, 224.1) * mm, "end": v(935.57, 210.17) * mm});
            skLineSegment(sketch, "E46.30.0.3", {"start": v(916.64, 227.11) * mm, "end": v(931, 224.1) * mm});
            skLineSegment(sketch, "E46.30.0.4", {"start": v(906.86, 216.18) * mm, "end": v(916.64, 227.11) * mm});
            skLineSegment(sketch, "E46.30.0.5", {"start": v(911.44, 202.25) * mm, "end": v(906.86, 216.18) * mm});
            skLineSegment(sketch, "E46.30.1.0", {"start": v(925.8, 119.25) * mm, "end": v(911.44, 122.25) * mm});
            skLineSegment(sketch, "E46.30.1.1", {"start": v(935.57, 130.17) * mm, "end": v(925.8, 119.25) * mm});
            skLineSegment(sketch, "E46.30.1.2", {"start": v(931, 144.1) * mm, "end": v(935.57, 130.17) * mm});
            skLineSegment(sketch, "E46.30.1.3", {"start": v(916.64, 147.11) * mm, "end": v(931, 144.1) * mm});
            skLineSegment(sketch, "E46.30.1.4", {"start": v(906.86, 136.18) * mm, "end": v(916.64, 147.11) * mm});
            skLineSegment(sketch, "E46.30.1.5", {"start": v(911.44, 122.25) * mm, "end": v(906.86, 136.18) * mm});
            skLineSegment(sketch, "E46.30.2.0", {"start": v(925.8, 39.25) * mm, "end": v(911.44, 42.25) * mm});
            skLineSegment(sketch, "E46.30.2.1", {"start": v(935.57, 50.17) * mm, "end": v(925.8, 39.25) * mm});
            skLineSegment(sketch, "E46.30.2.2", {"start": v(931, 64.1) * mm, "end": v(935.57, 50.17) * mm});
            skLineSegment(sketch, "E46.30.2.3", {"start": v(916.64, 67.11) * mm, "end": v(931, 64.1) * mm});
            skLineSegment(sketch, "E46.30.2.4", {"start": v(906.86, 56.18) * mm, "end": v(916.64, 67.11) * mm});
            skLineSegment(sketch, "E46.30.2.5", {"start": v(911.44, 42.25) * mm, "end": v(906.86, 56.18) * mm});
            skLineSegment(sketch, "E46.30.3.0", {"start": v(925.8, -40.75) * mm, "end": v(911.44, -37.75) * mm});
            skLineSegment(sketch, "E46.30.3.1", {"start": v(935.57, -29.83) * mm, "end": v(925.8, -40.75) * mm});
            skLineSegment(sketch, "E46.30.3.2", {"start": v(931, -15.9) * mm, "end": v(935.57, -29.83) * mm});
            skLineSegment(sketch, "E46.30.3.3", {"start": v(916.64, -12.89) * mm, "end": v(931, -15.9) * mm});
            skLineSegment(sketch, "E46.30.3.4", {"start": v(906.86, -23.82) * mm, "end": v(916.64, -12.89) * mm});
            skLineSegment(sketch, "E46.30.3.5", {"start": v(911.44, -37.75) * mm, "end": v(906.86, -23.82) * mm});
            skLineSegment(sketch, "E46.30.4.0", {"start": v(925.8, -120.75) * mm, "end": v(911.44, -117.75) * mm});
            skLineSegment(sketch, "E46.30.4.1", {"start": v(935.57, -109.83) * mm, "end": v(925.8, -120.75) * mm});
            skLineSegment(sketch, "E46.30.4.2", {"start": v(931, -95.9) * mm, "end": v(935.57, -109.83) * mm});
            skLineSegment(sketch, "E46.30.4.3", {"start": v(916.64, -92.89) * mm, "end": v(931, -95.9) * mm});
            skLineSegment(sketch, "E46.30.4.4", {"start": v(906.86, -103.82) * mm, "end": v(916.64, -92.89) * mm});
            skLineSegment(sketch, "E46.30.4.5", {"start": v(911.44, -117.75) * mm, "end": v(906.86, -103.82) * mm});
            skLineSegment(sketch, "E46.30.5.0", {"start": v(925.8, -200.75) * mm, "end": v(911.44, -197.75) * mm});
            skLineSegment(sketch, "E46.30.5.1", {"start": v(935.57, -189.83) * mm, "end": v(925.8, -200.75) * mm});
            skLineSegment(sketch, "E46.30.5.2", {"start": v(931, -175.9) * mm, "end": v(935.57, -189.83) * mm});
            skLineSegment(sketch, "E46.30.5.3", {"start": v(916.64, -172.89) * mm, "end": v(931, -175.9) * mm});
            skLineSegment(sketch, "E46.30.5.4", {"start": v(906.86, -183.82) * mm, "end": v(916.64, -172.89) * mm});
            skLineSegment(sketch, "E46.30.5.5", {"start": v(911.44, -197.75) * mm, "end": v(906.86, -183.82) * mm});
            skLineSegment(sketch, "E46.31.0.0", {"start": v(1005.8, 199.25) * mm, "end": v(991.44, 202.25) * mm});
            skLineSegment(sketch, "E46.31.0.1", {"start": v(1015.57, 210.17) * mm, "end": v(1005.8, 199.25) * mm});
            skLineSegment(sketch, "E46.31.0.2", {"start": v(1011, 224.1) * mm, "end": v(1015.57, 210.17) * mm});
            skLineSegment(sketch, "E46.31.0.3", {"start": v(996.64, 227.11) * mm, "end": v(1011, 224.1) * mm});
            skLineSegment(sketch, "E46.31.0.4", {"start": v(986.86, 216.18) * mm, "end": v(996.64, 227.11) * mm});
            skLineSegment(sketch, "E46.31.0.5", {"start": v(991.44, 202.25) * mm, "end": v(986.86, 216.18) * mm});
            skLineSegment(sketch, "E46.31.1.0", {"start": v(1005.8, 119.25) * mm, "end": v(991.44, 122.25) * mm});
            skLineSegment(sketch, "E46.31.1.1", {"start": v(1015.57, 130.17) * mm, "end": v(1005.8, 119.25) * mm});
            skLineSegment(sketch, "E46.31.1.2", {"start": v(1011, 144.1) * mm, "end": v(1015.57, 130.17) * mm});
            skLineSegment(sketch, "E46.31.1.3", {"start": v(996.64, 147.11) * mm, "end": v(1011, 144.1) * mm});
            skLineSegment(sketch, "E46.31.1.4", {"start": v(986.86, 136.18) * mm, "end": v(996.64, 147.11) * mm});
            skLineSegment(sketch, "E46.31.1.5", {"start": v(991.44, 122.25) * mm, "end": v(986.86, 136.18) * mm});
            skLineSegment(sketch, "E46.31.2.0", {"start": v(1005.8, 39.25) * mm, "end": v(991.44, 42.25) * mm});
            skLineSegment(sketch, "E46.31.2.1", {"start": v(1015.57, 50.17) * mm, "end": v(1005.8, 39.25) * mm});
            skLineSegment(sketch, "E46.31.2.2", {"start": v(1011, 64.1) * mm, "end": v(1015.57, 50.17) * mm});
            skLineSegment(sketch, "E46.31.2.3", {"start": v(996.64, 67.11) * mm, "end": v(1011, 64.1) * mm});
            skLineSegment(sketch, "E46.31.2.4", {"start": v(986.86, 56.18) * mm, "end": v(996.64, 67.11) * mm});
            skLineSegment(sketch, "E46.31.2.5", {"start": v(991.44, 42.25) * mm, "end": v(986.86, 56.18) * mm});
            skLineSegment(sketch, "E46.31.3.0", {"start": v(1005.8, -40.75) * mm, "end": v(991.44, -37.75) * mm});
            skLineSegment(sketch, "E46.31.3.1", {"start": v(1015.57, -29.83) * mm, "end": v(1005.8, -40.75) * mm});
            skLineSegment(sketch, "E46.31.3.2", {"start": v(1011, -15.9) * mm, "end": v(1015.57, -29.83) * mm});
            skLineSegment(sketch, "E46.31.3.3", {"start": v(996.64, -12.89) * mm, "end": v(1011, -15.9) * mm});
            skLineSegment(sketch, "E46.31.3.4", {"start": v(986.86, -23.82) * mm, "end": v(996.64, -12.89) * mm});
            skLineSegment(sketch, "E46.31.3.5", {"start": v(991.44, -37.75) * mm, "end": v(986.86, -23.82) * mm});
            skLineSegment(sketch, "E46.31.4.0", {"start": v(1005.8, -120.75) * mm, "end": v(991.44, -117.75) * mm});
            skLineSegment(sketch, "E46.31.4.1", {"start": v(1015.57, -109.83) * mm, "end": v(1005.8, -120.75) * mm});
            skLineSegment(sketch, "E46.31.4.2", {"start": v(1011, -95.9) * mm, "end": v(1015.57, -109.83) * mm});
            skLineSegment(sketch, "E46.31.4.3", {"start": v(996.64, -92.89) * mm, "end": v(1011, -95.9) * mm});
            skLineSegment(sketch, "E46.31.4.4", {"start": v(986.86, -103.82) * mm, "end": v(996.64, -92.89) * mm});
            skLineSegment(sketch, "E46.31.4.5", {"start": v(991.44, -117.75) * mm, "end": v(986.86, -103.82) * mm});
            skLineSegment(sketch, "E46.31.5.0", {"start": v(1005.8, -200.75) * mm, "end": v(991.44, -197.75) * mm});
            skLineSegment(sketch, "E46.31.5.1", {"start": v(1015.57, -189.83) * mm, "end": v(1005.8, -200.75) * mm});
            skLineSegment(sketch, "E46.31.5.2", {"start": v(1011, -175.9) * mm, "end": v(1015.57, -189.83) * mm});
            skLineSegment(sketch, "E46.31.5.3", {"start": v(996.64, -172.89) * mm, "end": v(1011, -175.9) * mm});
            skLineSegment(sketch, "E46.31.5.4", {"start": v(986.86, -183.82) * mm, "end": v(996.64, -172.89) * mm});
            skLineSegment(sketch, "E46.31.5.5", {"start": v(991.44, -197.75) * mm, "end": v(986.86, -183.82) * mm});
            skLineSegment(sketch, "E46.32.0.0", {"start": v(1085.8, 199.25) * mm, "end": v(1071.44, 202.25) * mm});
            skLineSegment(sketch, "E46.32.0.1", {"start": v(1095.57, 210.17) * mm, "end": v(1085.8, 199.25) * mm});
            skLineSegment(sketch, "E46.32.0.2", {"start": v(1091, 224.1) * mm, "end": v(1095.57, 210.17) * mm});
            skLineSegment(sketch, "E46.32.0.3", {"start": v(1076.64, 227.11) * mm, "end": v(1091, 224.1) * mm});
            skLineSegment(sketch, "E46.32.0.4", {"start": v(1066.86, 216.18) * mm, "end": v(1076.64, 227.11) * mm});
            skLineSegment(sketch, "E46.32.0.5", {"start": v(1071.44, 202.25) * mm, "end": v(1066.86, 216.18) * mm});
            skLineSegment(sketch, "E46.32.1.0", {"start": v(1085.8, 119.25) * mm, "end": v(1071.44, 122.25) * mm});
            skLineSegment(sketch, "E46.32.1.1", {"start": v(1095.57, 130.17) * mm, "end": v(1085.8, 119.25) * mm});
            skLineSegment(sketch, "E46.32.1.2", {"start": v(1091, 144.1) * mm, "end": v(1095.57, 130.17) * mm});
            skLineSegment(sketch, "E46.32.1.3", {"start": v(1076.64, 147.11) * mm, "end": v(1091, 144.1) * mm});
            skLineSegment(sketch, "E46.32.1.4", {"start": v(1066.86, 136.18) * mm, "end": v(1076.64, 147.11) * mm});
            skLineSegment(sketch, "E46.32.1.5", {"start": v(1071.44, 122.25) * mm, "end": v(1066.86, 136.18) * mm});
            skLineSegment(sketch, "E46.32.2.0", {"start": v(1085.8, 39.25) * mm, "end": v(1071.44, 42.25) * mm});
            skLineSegment(sketch, "E46.32.2.1", {"start": v(1095.57, 50.17) * mm, "end": v(1085.8, 39.25) * mm});
            skLineSegment(sketch, "E46.32.2.2", {"start": v(1091, 64.1) * mm, "end": v(1095.57, 50.17) * mm});
            skLineSegment(sketch, "E46.32.2.3", {"start": v(1076.64, 67.11) * mm, "end": v(1091, 64.1) * mm});
            skLineSegment(sketch, "E46.32.2.4", {"start": v(1066.86, 56.18) * mm, "end": v(1076.64, 67.11) * mm});
            skLineSegment(sketch, "E46.32.2.5", {"start": v(1071.44, 42.25) * mm, "end": v(1066.86, 56.18) * mm});
            skLineSegment(sketch, "E46.32.3.0", {"start": v(1085.8, -40.75) * mm, "end": v(1071.44, -37.75) * mm});
            skLineSegment(sketch, "E46.32.3.1", {"start": v(1095.57, -29.83) * mm, "end": v(1085.8, -40.75) * mm});
            skLineSegment(sketch, "E46.32.3.2", {"start": v(1091, -15.9) * mm, "end": v(1095.57, -29.83) * mm});
            skLineSegment(sketch, "E46.32.3.3", {"start": v(1076.64, -12.89) * mm, "end": v(1091, -15.9) * mm});
            skLineSegment(sketch, "E46.32.3.4", {"start": v(1066.86, -23.82) * mm, "end": v(1076.64, -12.89) * mm});
            skLineSegment(sketch, "E46.32.3.5", {"start": v(1071.44, -37.75) * mm, "end": v(1066.86, -23.82) * mm});
            skLineSegment(sketch, "E46.32.4.0", {"start": v(1085.8, -120.75) * mm, "end": v(1071.44, -117.75) * mm});
            skLineSegment(sketch, "E46.32.4.1", {"start": v(1095.57, -109.83) * mm, "end": v(1085.8, -120.75) * mm});
            skLineSegment(sketch, "E46.32.4.2", {"start": v(1091, -95.9) * mm, "end": v(1095.57, -109.83) * mm});
            skLineSegment(sketch, "E46.32.4.3", {"start": v(1076.64, -92.89) * mm, "end": v(1091, -95.9) * mm});
            skLineSegment(sketch, "E46.32.4.4", {"start": v(1066.86, -103.82) * mm, "end": v(1076.64, -92.89) * mm});
            skLineSegment(sketch, "E46.32.4.5", {"start": v(1071.44, -117.75) * mm, "end": v(1066.86, -103.82) * mm});
            skLineSegment(sketch, "E46.32.5.0", {"start": v(1085.8, -200.75) * mm, "end": v(1071.44, -197.75) * mm});
            skLineSegment(sketch, "E46.32.5.1", {"start": v(1095.57, -189.83) * mm, "end": v(1085.8, -200.75) * mm});
            skLineSegment(sketch, "E46.32.5.2", {"start": v(1091, -175.9) * mm, "end": v(1095.57, -189.83) * mm});
            skLineSegment(sketch, "E46.32.5.3", {"start": v(1076.64, -172.89) * mm, "end": v(1091, -175.9) * mm});
            skLineSegment(sketch, "E46.32.5.4", {"start": v(1066.86, -183.82) * mm, "end": v(1076.64, -172.89) * mm});
            skLineSegment(sketch, "E46.32.5.5", {"start": v(1071.44, -197.75) * mm, "end": v(1066.86, -183.82) * mm});
            skLineSegment(sketch, "E46.33.0.0", {"start": v(1165.8, 199.25) * mm, "end": v(1151.44, 202.25) * mm});
            skLineSegment(sketch, "E46.33.0.1", {"start": v(1175.57, 210.17) * mm, "end": v(1165.8, 199.25) * mm});
            skLineSegment(sketch, "E46.33.0.2", {"start": v(1171, 224.1) * mm, "end": v(1175.57, 210.17) * mm});
            skLineSegment(sketch, "E46.33.0.3", {"start": v(1156.64, 227.11) * mm, "end": v(1171, 224.1) * mm});
            skLineSegment(sketch, "E46.33.0.4", {"start": v(1146.86, 216.18) * mm, "end": v(1156.64, 227.11) * mm});
            skLineSegment(sketch, "E46.33.0.5", {"start": v(1151.44, 202.25) * mm, "end": v(1146.86, 216.18) * mm});
            skLineSegment(sketch, "E46.33.1.0", {"start": v(1165.8, 119.25) * mm, "end": v(1151.44, 122.25) * mm});
            skLineSegment(sketch, "E46.33.1.1", {"start": v(1175.57, 130.17) * mm, "end": v(1165.8, 119.25) * mm});
            skLineSegment(sketch, "E46.33.1.2", {"start": v(1171, 144.1) * mm, "end": v(1175.57, 130.17) * mm});
            skLineSegment(sketch, "E46.33.1.3", {"start": v(1156.64, 147.11) * mm, "end": v(1171, 144.1) * mm});
            skLineSegment(sketch, "E46.33.1.4", {"start": v(1146.86, 136.18) * mm, "end": v(1156.64, 147.11) * mm});
            skLineSegment(sketch, "E46.33.1.5", {"start": v(1151.44, 122.25) * mm, "end": v(1146.86, 136.18) * mm});
            skLineSegment(sketch, "E46.33.2.0", {"start": v(1165.8, 39.25) * mm, "end": v(1151.44, 42.25) * mm});
            skLineSegment(sketch, "E46.33.2.1", {"start": v(1175.57, 50.17) * mm, "end": v(1165.8, 39.25) * mm});
            skLineSegment(sketch, "E46.33.2.2", {"start": v(1171, 64.1) * mm, "end": v(1175.57, 50.17) * mm});
            skLineSegment(sketch, "E46.33.2.3", {"start": v(1156.64, 67.11) * mm, "end": v(1171, 64.1) * mm});
            skLineSegment(sketch, "E46.33.2.4", {"start": v(1146.86, 56.18) * mm, "end": v(1156.64, 67.11) * mm});
            skLineSegment(sketch, "E46.33.2.5", {"start": v(1151.44, 42.25) * mm, "end": v(1146.86, 56.18) * mm});
            skLineSegment(sketch, "E46.33.3.0", {"start": v(1165.8, -40.75) * mm, "end": v(1151.44, -37.75) * mm});
            skLineSegment(sketch, "E46.33.3.1", {"start": v(1175.57, -29.83) * mm, "end": v(1165.8, -40.75) * mm});
            skLineSegment(sketch, "E46.33.3.2", {"start": v(1171, -15.9) * mm, "end": v(1175.57, -29.83) * mm});
            skLineSegment(sketch, "E46.33.3.3", {"start": v(1156.64, -12.89) * mm, "end": v(1171, -15.9) * mm});
            skLineSegment(sketch, "E46.33.3.4", {"start": v(1146.86, -23.82) * mm, "end": v(1156.64, -12.89) * mm});
            skLineSegment(sketch, "E46.33.3.5", {"start": v(1151.44, -37.75) * mm, "end": v(1146.86, -23.82) * mm});
            skLineSegment(sketch, "E46.33.4.0", {"start": v(1165.8, -120.75) * mm, "end": v(1151.44, -117.75) * mm});
            skLineSegment(sketch, "E46.33.4.1", {"start": v(1175.57, -109.83) * mm, "end": v(1165.8, -120.75) * mm});
            skLineSegment(sketch, "E46.33.4.2", {"start": v(1171, -95.9) * mm, "end": v(1175.57, -109.83) * mm});
            skLineSegment(sketch, "E46.33.4.3", {"start": v(1156.64, -92.89) * mm, "end": v(1171, -95.9) * mm});
            skLineSegment(sketch, "E46.33.4.4", {"start": v(1146.86, -103.82) * mm, "end": v(1156.64, -92.89) * mm});
            skLineSegment(sketch, "E46.33.4.5", {"start": v(1151.44, -117.75) * mm, "end": v(1146.86, -103.82) * mm});
            skLineSegment(sketch, "E46.33.5.0", {"start": v(1165.8, -200.75) * mm, "end": v(1151.44, -197.75) * mm});
            skLineSegment(sketch, "E46.33.5.1", {"start": v(1175.57, -189.83) * mm, "end": v(1165.8, -200.75) * mm});
            skLineSegment(sketch, "E46.33.5.2", {"start": v(1171, -175.9) * mm, "end": v(1175.57, -189.83) * mm});
            skLineSegment(sketch, "E46.33.5.3", {"start": v(1156.64, -172.89) * mm, "end": v(1171, -175.9) * mm});
            skLineSegment(sketch, "E46.33.5.4", {"start": v(1146.86, -183.82) * mm, "end": v(1156.64, -172.89) * mm});
            skLineSegment(sketch, "E46.33.5.5", {"start": v(1151.44, -197.75) * mm, "end": v(1146.86, -183.82) * mm});
            skLineSegment(sketch, "E46.34.0.0", {"start": v(1245.8, 199.25) * mm, "end": v(1231.44, 202.25) * mm});
            skLineSegment(sketch, "E46.34.0.1", {"start": v(1255.57, 210.17) * mm, "end": v(1245.8, 199.25) * mm});
            skLineSegment(sketch, "E46.34.0.2", {"start": v(1251, 224.1) * mm, "end": v(1255.57, 210.17) * mm});
            skLineSegment(sketch, "E46.34.0.3", {"start": v(1236.64, 227.11) * mm, "end": v(1251, 224.1) * mm});
            skLineSegment(sketch, "E46.34.0.4", {"start": v(1226.86, 216.18) * mm, "end": v(1236.64, 227.11) * mm});
            skLineSegment(sketch, "E46.34.0.5", {"start": v(1231.44, 202.25) * mm, "end": v(1226.86, 216.18) * mm});
            skLineSegment(sketch, "E46.34.1.0", {"start": v(1245.8, 119.25) * mm, "end": v(1231.44, 122.25) * mm});
            skLineSegment(sketch, "E46.34.1.1", {"start": v(1255.57, 130.17) * mm, "end": v(1245.8, 119.25) * mm});
            skLineSegment(sketch, "E46.34.1.2", {"start": v(1251, 144.1) * mm, "end": v(1255.57, 130.17) * mm});
            skLineSegment(sketch, "E46.34.1.3", {"start": v(1236.64, 147.11) * mm, "end": v(1251, 144.1) * mm});
            skLineSegment(sketch, "E46.34.1.4", {"start": v(1226.86, 136.18) * mm, "end": v(1236.64, 147.11) * mm});
            skLineSegment(sketch, "E46.34.1.5", {"start": v(1231.44, 122.25) * mm, "end": v(1226.86, 136.18) * mm});
            skLineSegment(sketch, "E46.34.2.0", {"start": v(1245.8, 39.25) * mm, "end": v(1231.44, 42.25) * mm});
            skLineSegment(sketch, "E46.34.2.1", {"start": v(1255.57, 50.17) * mm, "end": v(1245.8, 39.25) * mm});
            skLineSegment(sketch, "E46.34.2.2", {"start": v(1251, 64.1) * mm, "end": v(1255.57, 50.17) * mm});
            skLineSegment(sketch, "E46.34.2.3", {"start": v(1236.64, 67.11) * mm, "end": v(1251, 64.1) * mm});
            skLineSegment(sketch, "E46.34.2.4", {"start": v(1226.86, 56.18) * mm, "end": v(1236.64, 67.11) * mm});
            skLineSegment(sketch, "E46.34.2.5", {"start": v(1231.44, 42.25) * mm, "end": v(1226.86, 56.18) * mm});
            skLineSegment(sketch, "E46.34.3.0", {"start": v(1245.8, -40.75) * mm, "end": v(1231.44, -37.75) * mm});
            skLineSegment(sketch, "E46.34.3.1", {"start": v(1255.57, -29.83) * mm, "end": v(1245.8, -40.75) * mm});
            skLineSegment(sketch, "E46.34.3.2", {"start": v(1251, -15.9) * mm, "end": v(1255.57, -29.83) * mm});
            skLineSegment(sketch, "E46.34.3.3", {"start": v(1236.64, -12.89) * mm, "end": v(1251, -15.9) * mm});
            skLineSegment(sketch, "E46.34.3.4", {"start": v(1226.86, -23.82) * mm, "end": v(1236.64, -12.89) * mm});
            skLineSegment(sketch, "E46.34.3.5", {"start": v(1231.44, -37.75) * mm, "end": v(1226.86, -23.82) * mm});
            skLineSegment(sketch, "E46.34.4.0", {"start": v(1245.8, -120.75) * mm, "end": v(1231.44, -117.75) * mm});
            skLineSegment(sketch, "E46.34.4.1", {"start": v(1255.57, -109.83) * mm, "end": v(1245.8, -120.75) * mm});
            skLineSegment(sketch, "E46.34.4.2", {"start": v(1251, -95.9) * mm, "end": v(1255.57, -109.83) * mm});
            skLineSegment(sketch, "E46.34.4.3", {"start": v(1236.64, -92.89) * mm, "end": v(1251, -95.9) * mm});
            skLineSegment(sketch, "E46.34.4.4", {"start": v(1226.86, -103.82) * mm, "end": v(1236.64, -92.89) * mm});
            skLineSegment(sketch, "E46.34.4.5", {"start": v(1231.44, -117.75) * mm, "end": v(1226.86, -103.82) * mm});
            skLineSegment(sketch, "E46.34.5.0", {"start": v(1245.8, -200.75) * mm, "end": v(1231.44, -197.75) * mm});
            skLineSegment(sketch, "E46.34.5.1", {"start": v(1255.57, -189.83) * mm, "end": v(1245.8, -200.75) * mm});
            skLineSegment(sketch, "E46.34.5.2", {"start": v(1251, -175.9) * mm, "end": v(1255.57, -189.83) * mm});
            skLineSegment(sketch, "E46.34.5.3", {"start": v(1236.64, -172.89) * mm, "end": v(1251, -175.9) * mm});
            skLineSegment(sketch, "E46.34.5.4", {"start": v(1226.86, -183.82) * mm, "end": v(1236.64, -172.89) * mm});
            skLineSegment(sketch, "E46.34.5.5", {"start": v(1231.44, -197.75) * mm, "end": v(1226.86, -183.82) * mm});
            skLineSegment(sketch, "E46.35.0.0", {"start": v(1325.8, 199.25) * mm, "end": v(1311.44, 202.25) * mm});
            skLineSegment(sketch, "E46.35.0.1", {"start": v(1335.57, 210.17) * mm, "end": v(1325.8, 199.25) * mm});
            skLineSegment(sketch, "E46.35.0.2", {"start": v(1331, 224.1) * mm, "end": v(1335.57, 210.17) * mm});
            skLineSegment(sketch, "E46.35.0.3", {"start": v(1316.64, 227.11) * mm, "end": v(1331, 224.1) * mm});
            skLineSegment(sketch, "E46.35.0.4", {"start": v(1306.86, 216.18) * mm, "end": v(1316.64, 227.11) * mm});
            skLineSegment(sketch, "E46.35.0.5", {"start": v(1311.44, 202.25) * mm, "end": v(1306.86, 216.18) * mm});
            skLineSegment(sketch, "E46.35.1.0", {"start": v(1325.8, 119.25) * mm, "end": v(1311.44, 122.25) * mm});
            skLineSegment(sketch, "E46.35.1.1", {"start": v(1335.57, 130.17) * mm, "end": v(1325.8, 119.25) * mm});
            skLineSegment(sketch, "E46.35.1.2", {"start": v(1331, 144.1) * mm, "end": v(1335.57, 130.17) * mm});
            skLineSegment(sketch, "E46.35.1.3", {"start": v(1316.64, 147.11) * mm, "end": v(1331, 144.1) * mm});
            skLineSegment(sketch, "E46.35.1.4", {"start": v(1306.86, 136.18) * mm, "end": v(1316.64, 147.11) * mm});
            skLineSegment(sketch, "E46.35.1.5", {"start": v(1311.44, 122.25) * mm, "end": v(1306.86, 136.18) * mm});
            skLineSegment(sketch, "E46.35.2.0", {"start": v(1325.8, 39.25) * mm, "end": v(1311.44, 42.25) * mm});
            skLineSegment(sketch, "E46.35.2.1", {"start": v(1335.57, 50.17) * mm, "end": v(1325.8, 39.25) * mm});
            skLineSegment(sketch, "E46.35.2.2", {"start": v(1331, 64.1) * mm, "end": v(1335.57, 50.17) * mm});
            skLineSegment(sketch, "E46.35.2.3", {"start": v(1316.64, 67.11) * mm, "end": v(1331, 64.1) * mm});
            skLineSegment(sketch, "E46.35.2.4", {"start": v(1306.86, 56.18) * mm, "end": v(1316.64, 67.11) * mm});
            skLineSegment(sketch, "E46.35.2.5", {"start": v(1311.44, 42.25) * mm, "end": v(1306.86, 56.18) * mm});
            skLineSegment(sketch, "E46.35.3.0", {"start": v(1325.8, -40.75) * mm, "end": v(1311.44, -37.75) * mm});
            skLineSegment(sketch, "E46.35.3.1", {"start": v(1335.57, -29.83) * mm, "end": v(1325.8, -40.75) * mm});
            skLineSegment(sketch, "E46.35.3.2", {"start": v(1331, -15.9) * mm, "end": v(1335.57, -29.83) * mm});
            skLineSegment(sketch, "E46.35.3.3", {"start": v(1316.64, -12.89) * mm, "end": v(1331, -15.9) * mm});
            skLineSegment(sketch, "E46.35.3.4", {"start": v(1306.86, -23.82) * mm, "end": v(1316.64, -12.89) * mm});
            skLineSegment(sketch, "E46.35.3.5", {"start": v(1311.44, -37.75) * mm, "end": v(1306.86, -23.82) * mm});
            skLineSegment(sketch, "E46.35.4.0", {"start": v(1325.8, -120.75) * mm, "end": v(1311.44, -117.75) * mm});
            skLineSegment(sketch, "E46.35.4.1", {"start": v(1335.57, -109.83) * mm, "end": v(1325.8, -120.75) * mm});
            skLineSegment(sketch, "E46.35.4.2", {"start": v(1331, -95.9) * mm, "end": v(1335.57, -109.83) * mm});
            skLineSegment(sketch, "E46.35.4.3", {"start": v(1316.64, -92.89) * mm, "end": v(1331, -95.9) * mm});
            skLineSegment(sketch, "E46.35.4.4", {"start": v(1306.86, -103.82) * mm, "end": v(1316.64, -92.89) * mm});
            skLineSegment(sketch, "E46.35.4.5", {"start": v(1311.44, -117.75) * mm, "end": v(1306.86, -103.82) * mm});
            skLineSegment(sketch, "E46.35.5.0", {"start": v(1325.8, -200.75) * mm, "end": v(1311.44, -197.75) * mm});
            skLineSegment(sketch, "E46.35.5.1", {"start": v(1335.57, -189.83) * mm, "end": v(1325.8, -200.75) * mm});
            skLineSegment(sketch, "E46.35.5.2", {"start": v(1331, -175.9) * mm, "end": v(1335.57, -189.83) * mm});
            skLineSegment(sketch, "E46.35.5.3", {"start": v(1316.64, -172.89) * mm, "end": v(1331, -175.9) * mm});
            skLineSegment(sketch, "E46.35.5.4", {"start": v(1306.86, -183.82) * mm, "end": v(1316.64, -172.89) * mm});
            skLineSegment(sketch, "E46.35.5.5", {"start": v(1311.44, -197.75) * mm, "end": v(1306.86, -183.82) * mm});
            skLineSegment(sketch, "E46.36.0.0", {"start": v(1405.8, 199.25) * mm, "end": v(1391.44, 202.25) * mm});
            skLineSegment(sketch, "E46.36.0.1", {"start": v(1415.57, 210.17) * mm, "end": v(1405.8, 199.25) * mm});
            skLineSegment(sketch, "E46.36.0.2", {"start": v(1411, 224.1) * mm, "end": v(1415.57, 210.17) * mm});
            skLineSegment(sketch, "E46.36.0.3", {"start": v(1396.64, 227.11) * mm, "end": v(1411, 224.1) * mm});
            skLineSegment(sketch, "E46.36.0.4", {"start": v(1386.86, 216.18) * mm, "end": v(1396.64, 227.11) * mm});
            skLineSegment(sketch, "E46.36.0.5", {"start": v(1391.44, 202.25) * mm, "end": v(1386.86, 216.18) * mm});
            skLineSegment(sketch, "E46.36.1.0", {"start": v(1405.8, 119.25) * mm, "end": v(1391.44, 122.25) * mm});
            skLineSegment(sketch, "E46.36.1.1", {"start": v(1415.57, 130.17) * mm, "end": v(1405.8, 119.25) * mm});
            skLineSegment(sketch, "E46.36.1.2", {"start": v(1411, 144.1) * mm, "end": v(1415.57, 130.17) * mm});
            skLineSegment(sketch, "E46.36.1.3", {"start": v(1396.64, 147.11) * mm, "end": v(1411, 144.1) * mm});
            skLineSegment(sketch, "E46.36.1.4", {"start": v(1386.86, 136.18) * mm, "end": v(1396.64, 147.11) * mm});
            skLineSegment(sketch, "E46.36.1.5", {"start": v(1391.44, 122.25) * mm, "end": v(1386.86, 136.18) * mm});
            skLineSegment(sketch, "E46.36.2.0", {"start": v(1405.8, 39.25) * mm, "end": v(1391.44, 42.25) * mm});
            skLineSegment(sketch, "E46.36.2.1", {"start": v(1415.57, 50.17) * mm, "end": v(1405.8, 39.25) * mm});
            skLineSegment(sketch, "E46.36.2.2", {"start": v(1411, 64.1) * mm, "end": v(1415.57, 50.17) * mm});
            skLineSegment(sketch, "E46.36.2.3", {"start": v(1396.64, 67.11) * mm, "end": v(1411, 64.1) * mm});
            skLineSegment(sketch, "E46.36.2.4", {"start": v(1386.86, 56.18) * mm, "end": v(1396.64, 67.11) * mm});
            skLineSegment(sketch, "E46.36.2.5", {"start": v(1391.44, 42.25) * mm, "end": v(1386.86, 56.18) * mm});
            skLineSegment(sketch, "E46.36.3.0", {"start": v(1405.8, -40.75) * mm, "end": v(1391.44, -37.75) * mm});
            skLineSegment(sketch, "E46.36.3.1", {"start": v(1415.57, -29.83) * mm, "end": v(1405.8, -40.75) * mm});
            skLineSegment(sketch, "E46.36.3.2", {"start": v(1411, -15.9) * mm, "end": v(1415.57, -29.83) * mm});
            skLineSegment(sketch, "E46.36.3.3", {"start": v(1396.64, -12.89) * mm, "end": v(1411, -15.9) * mm});
            skLineSegment(sketch, "E46.36.3.4", {"start": v(1386.86, -23.82) * mm, "end": v(1396.64, -12.89) * mm});
            skLineSegment(sketch, "E46.36.3.5", {"start": v(1391.44, -37.75) * mm, "end": v(1386.86, -23.82) * mm});
            skLineSegment(sketch, "E46.36.4.0", {"start": v(1405.8, -120.75) * mm, "end": v(1391.44, -117.75) * mm});
            skLineSegment(sketch, "E46.36.4.1", {"start": v(1415.57, -109.83) * mm, "end": v(1405.8, -120.75) * mm});
            skLineSegment(sketch, "E46.36.4.2", {"start": v(1411, -95.9) * mm, "end": v(1415.57, -109.83) * mm});
            skLineSegment(sketch, "E46.36.4.3", {"start": v(1396.64, -92.89) * mm, "end": v(1411, -95.9) * mm});
            skLineSegment(sketch, "E46.36.4.4", {"start": v(1386.86, -103.82) * mm, "end": v(1396.64, -92.89) * mm});
            skLineSegment(sketch, "E46.36.4.5", {"start": v(1391.44, -117.75) * mm, "end": v(1386.86, -103.82) * mm});
            skLineSegment(sketch, "E46.36.5.0", {"start": v(1405.8, -200.75) * mm, "end": v(1391.44, -197.75) * mm});
            skLineSegment(sketch, "E46.36.5.1", {"start": v(1415.57, -189.83) * mm, "end": v(1405.8, -200.75) * mm});
            skLineSegment(sketch, "E46.36.5.2", {"start": v(1411, -175.9) * mm, "end": v(1415.57, -189.83) * mm});
            skLineSegment(sketch, "E46.36.5.3", {"start": v(1396.64, -172.89) * mm, "end": v(1411, -175.9) * mm});
            skLineSegment(sketch, "E46.36.5.4", {"start": v(1386.86, -183.82) * mm, "end": v(1396.64, -172.89) * mm});
            skLineSegment(sketch, "E46.36.5.5", {"start": v(1391.44, -197.75) * mm, "end": v(1386.86, -183.82) * mm});
            skLineSegment(sketch, "E46.37.0.0", {"start": v(1485.8, 199.25) * mm, "end": v(1471.44, 202.25) * mm});
            skLineSegment(sketch, "E46.37.0.1", {"start": v(1495.57, 210.17) * mm, "end": v(1485.8, 199.25) * mm});
            skLineSegment(sketch, "E46.37.0.2", {"start": v(1491, 224.1) * mm, "end": v(1495.57, 210.17) * mm});
            skLineSegment(sketch, "E46.37.0.3", {"start": v(1476.64, 227.11) * mm, "end": v(1491, 224.1) * mm});
            skLineSegment(sketch, "E46.37.0.4", {"start": v(1466.86, 216.18) * mm, "end": v(1476.64, 227.11) * mm});
            skLineSegment(sketch, "E46.37.0.5", {"start": v(1471.44, 202.25) * mm, "end": v(1466.86, 216.18) * mm});
            skLineSegment(sketch, "E46.37.1.0", {"start": v(1485.8, 119.25) * mm, "end": v(1471.44, 122.25) * mm});
            skLineSegment(sketch, "E46.37.1.1", {"start": v(1495.57, 130.17) * mm, "end": v(1485.8, 119.25) * mm});
            skLineSegment(sketch, "E46.37.1.2", {"start": v(1491, 144.1) * mm, "end": v(1495.57, 130.17) * mm});
            skLineSegment(sketch, "E46.37.1.3", {"start": v(1476.64, 147.11) * mm, "end": v(1491, 144.1) * mm});
            skLineSegment(sketch, "E46.37.1.4", {"start": v(1466.86, 136.18) * mm, "end": v(1476.64, 147.11) * mm});
            skLineSegment(sketch, "E46.37.1.5", {"start": v(1471.44, 122.25) * mm, "end": v(1466.86, 136.18) * mm});
            skLineSegment(sketch, "E46.37.2.0", {"start": v(1485.8, 39.25) * mm, "end": v(1471.44, 42.25) * mm});
            skLineSegment(sketch, "E46.37.2.1", {"start": v(1495.57, 50.17) * mm, "end": v(1485.8, 39.25) * mm});
            skLineSegment(sketch, "E46.37.2.2", {"start": v(1491, 64.1) * mm, "end": v(1495.57, 50.17) * mm});
            skLineSegment(sketch, "E46.37.2.3", {"start": v(1476.64, 67.11) * mm, "end": v(1491, 64.1) * mm});
            skLineSegment(sketch, "E46.37.2.4", {"start": v(1466.86, 56.18) * mm, "end": v(1476.64, 67.11) * mm});
            skLineSegment(sketch, "E46.37.2.5", {"start": v(1471.44, 42.25) * mm, "end": v(1466.86, 56.18) * mm});
            skLineSegment(sketch, "E46.37.3.0", {"start": v(1485.8, -40.75) * mm, "end": v(1471.44, -37.75) * mm});
            skLineSegment(sketch, "E46.37.3.1", {"start": v(1495.57, -29.83) * mm, "end": v(1485.8, -40.75) * mm});
            skLineSegment(sketch, "E46.37.3.2", {"start": v(1491, -15.9) * mm, "end": v(1495.57, -29.83) * mm});
            skLineSegment(sketch, "E46.37.3.3", {"start": v(1476.64, -12.89) * mm, "end": v(1491, -15.9) * mm});
            skLineSegment(sketch, "E46.37.3.4", {"start": v(1466.86, -23.82) * mm, "end": v(1476.64, -12.89) * mm});
            skLineSegment(sketch, "E46.37.3.5", {"start": v(1471.44, -37.75) * mm, "end": v(1466.86, -23.82) * mm});
            skLineSegment(sketch, "E46.37.4.0", {"start": v(1485.8, -120.75) * mm, "end": v(1471.44, -117.75) * mm});
            skLineSegment(sketch, "E46.37.4.1", {"start": v(1495.57, -109.83) * mm, "end": v(1485.8, -120.75) * mm});
            skLineSegment(sketch, "E46.37.4.2", {"start": v(1491, -95.9) * mm, "end": v(1495.57, -109.83) * mm});
            skLineSegment(sketch, "E46.37.4.3", {"start": v(1476.64, -92.89) * mm, "end": v(1491, -95.9) * mm});
            skLineSegment(sketch, "E46.37.4.4", {"start": v(1466.86, -103.82) * mm, "end": v(1476.64, -92.89) * mm});
            skLineSegment(sketch, "E46.37.4.5", {"start": v(1471.44, -117.75) * mm, "end": v(1466.86, -103.82) * mm});
            skLineSegment(sketch, "E46.37.5.0", {"start": v(1485.8, -200.75) * mm, "end": v(1471.44, -197.75) * mm});
            skLineSegment(sketch, "E46.37.5.1", {"start": v(1495.57, -189.83) * mm, "end": v(1485.8, -200.75) * mm});
            skLineSegment(sketch, "E46.37.5.2", {"start": v(1491, -175.9) * mm, "end": v(1495.57, -189.83) * mm});
            skLineSegment(sketch, "E46.37.5.3", {"start": v(1476.64, -172.89) * mm, "end": v(1491, -175.9) * mm});
            skLineSegment(sketch, "E46.37.5.4", {"start": v(1466.86, -183.82) * mm, "end": v(1476.64, -172.89) * mm});
            skLineSegment(sketch, "E46.37.5.5", {"start": v(1471.44, -197.75) * mm, "end": v(1466.86, -183.82) * mm});
            skLineSegment(sketch, "E46.direction1", {"start": v(-1488.56, 202.25) * mm, "end": v(-1408.56, 202.25) * mm, "construction": true});
            skLineSegment(sketch, "E46.direction2", {"start": v(-1488.56, 202.25) * mm, "end": v(-1488.56, 122.25) * mm, "construction": true});
            skSolve(sketch);
        }
        {
            var Q0;
            Q0 = qSketchRegion(id + "F9", true);
            var Q1;
            Q1=makeQuery(id+"F1.opExtrude","CAP_FACE",FACE,{"disambiguationData":[OSD([sQuery(id+"F0.wireOp",EDGE,"E2.bottom"),sQuery(id+"F0.wireOp",EDGE,"E2.top"),sQuery(id+"F0.wireOp",EDGE,"E2.left"),sQuery(id+"F0.wireOp",EDGE,"E2.right")])],"isStart":true});
            extrude(context, id + "F10", {"entities" : qUnion([Q0]), "operationType" : NewBodyOperationType.REMOVE, "endBound" : BoundingType.UP_TO_SURFACE, "oppositeDirection" : true, "depth" : 25.4 * mm, "endBoundEntityFace" : qUnion([Q1]), "offsetDistance" : 25.4 * mm});
        }
    });
